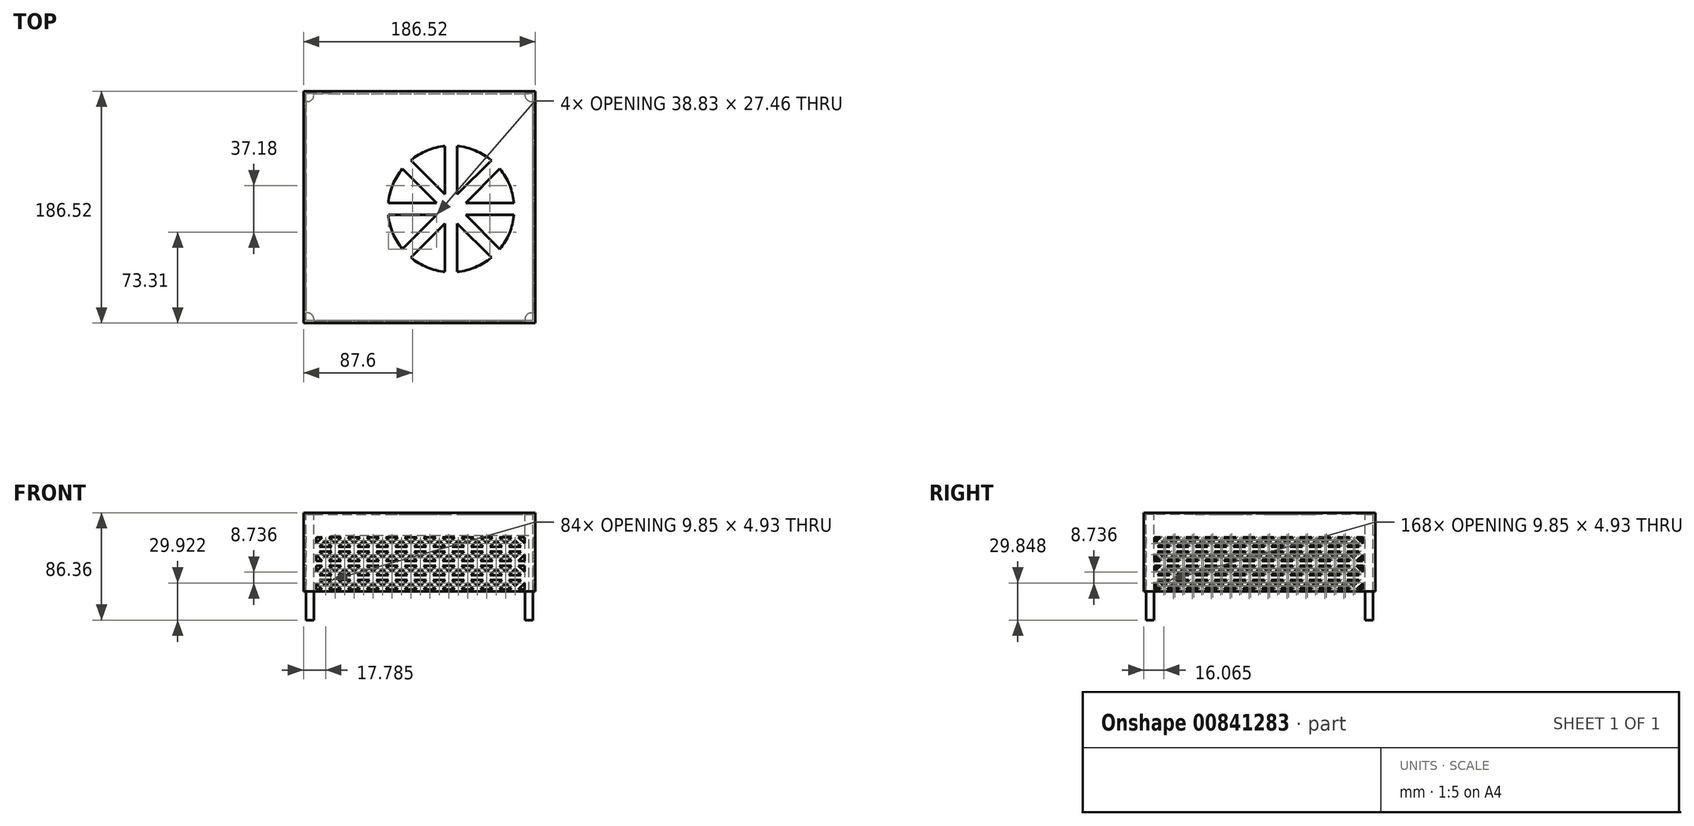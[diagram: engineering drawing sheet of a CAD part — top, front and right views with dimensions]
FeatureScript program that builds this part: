
annotation { "Feature Type Name" : "Feature", "Feature Type Description" : "" }
export const myFeature = defineFeature(function(context is Context, id is Id, definition is map)
    precondition{}
    {
        {
            var Q0;
            Q0=qCreatedBy(makeId("Top.planeOp"),FACE);
            var sketch = newSketch(context, id + "F0", { "sketchPlane" : qUnion([Q0])});
            skLineSegment(sketch, "E0.bottom", {"start": v(-6.35, 10.16) * mm, "end": v(163.65, 10.16) * mm});
            skLineSegment(sketch, "E0.top", {"start": v(-6.35, -159.84) * mm, "end": v(163.65, -159.84) * mm});
            skLineSegment(sketch, "E0.left", {"start": v(-6.35, 10.16) * mm, "end": v(-6.35, -159.84) * mm});
            skLineSegment(sketch, "E0.right", {"start": v(163.65, 10.16) * mm, "end": v(163.65, -159.84) * mm});
            skPoint(sketch, "E1", {"position": v(0, -154.94) * mm});
            skPoint(sketch, "E2", {"position": v(157.48, -22.86) * mm});
            skPoint(sketch, "E3", {"position": v(157.48, -154.94) * mm});
            skCircle(sketch, "E4", {"center": v(0, -154.94) * mm, "radius": 3.18 * mm});
            skCircle(sketch, "E5", {"center": v(0, 0) * mm, "radius": 3.18 * mm});
            skCircle(sketch, "E6", {"center": v(157.48, -22.86) * mm, "radius": 3.18 * mm});
            skCircle(sketch, "E7", {"center": v(157.48, -154.94) * mm, "radius": 3.18 * mm});
            skSolve(sketch);
        }
        {
            var Q0;
            Q0=qCreatedBy(makeId("Top.planeOp"),FACE);
            var sketch = newSketch(context, id + "F1", { "sketchPlane" : qUnion([Q0])});
            skLineSegment(sketch, "E8.0", {"start": v(-12.7, 16.51) * mm, "end": v(170, 16.51) * mm});
            skLineSegment(sketch, "E8.1", {"start": v(-12.7, 16.51) * mm, "end": v(-12.7, -166.2) * mm});
            skLineSegment(sketch, "E8.2", {"start": v(-12.7, -166.2) * mm, "end": v(170, -166.2) * mm});
            skLineSegment(sketch, "E8.3", {"start": v(170, 16.51) * mm, "end": v(170, -166.2) * mm});
            skLineSegment(sketch, "E9.0", {"start": v(-14.6, 18.42) * mm, "end": v(171.9, 18.42) * mm});
            skLineSegment(sketch, "E9.1", {"start": v(-14.6, 18.42) * mm, "end": v(-14.6, -168.1) * mm});
            skLineSegment(sketch, "E9.2", {"start": v(-14.6, -168.1) * mm, "end": v(171.9, -168.1) * mm});
            skLineSegment(sketch, "E9.3", {"start": v(171.9, 18.42) * mm, "end": v(171.9, -168.1) * mm});
            skSolve(sketch);
        }
        {
            var Q0;
            Q0=qSketchRegion(id+"F1",true);
            extrude(context, id + "F2", {"entities" : qUnion([Q0]), "depth" : 86.36 * mm, "offsetDistance" : 25.4 * mm});
        }
        {
            var Q0;
            Q0=qCreatedBy(makeId("Top.planeOp"),FACE);
            var sketch = newSketch(context, id + "F3", { "sketchPlane" : qUnion([Q0])});
            skLineSegment(sketch, "E10.bottom", {"start": v(135.08, -97.79) * mm, "end": v(135.08, 15.24) * mm, "construction": true});
            skLineSegment(sketch, "E10.top", {"start": v(79.2, -18.41) * mm, "end": v(79.2, 0) * mm, "construction": true});
            skLineSegment(sketch, "E10.left", {"start": v(135.08, 15.24) * mm, "end": v(79.2, 15.24) * mm, "construction": true});
            skLineSegment(sketch, "E10.right", {"start": v(135.08, -97.79) * mm, "end": v(79.2, -97.79) * mm, "construction": true});
            skCircle(sketch, "E11", {"center": v(131.27, 10.16) * mm, "radius": 1.27 * mm});
            skCircle(sketch, "E12", {"center": v(131.27, 10.16) * mm, "radius": 3.18 * mm});
            skLineSegment(sketch, "E13", {"start": v(79.2, 15.24) * mm, "end": v(71.07, 15.24) * mm, "construction": true});
            skLineSegment(sketch, "E14", {"start": v(71.07, 15.24) * mm, "end": v(71.07, 0) * mm, "construction": true});
            skLineSegment(sketch, "E15", {"start": v(71.07, 0) * mm, "end": v(79.2, 0) * mm, "construction": true});
            skLineSegment(sketch, "E16", {"start": v(79.2, -18.41) * mm, "end": v(71.07, -18.41) * mm, "construction": true});
            skLineSegment(sketch, "E17", {"start": v(71.07, -18.41) * mm, "end": v(71.07, -50.16) * mm, "construction": true});
            skLineSegment(sketch, "E18", {"start": v(71.07, -50.16) * mm, "end": v(79.2, -50.16) * mm, "construction": true});
            skCircle(sketch, "E19", {"center": v(83, -5.08) * mm, "radius": 3.18 * mm});
            skCircle(sketch, "E20", {"center": v(83, -5.08) * mm, "radius": 1.27 * mm});
            skLineSegment(sketch, "E21.trimOffspring", {"start": v(79.2, -97.79) * mm, "end": v(79.2, -50.16) * mm, "construction": true});
            skLineSegment(sketch, "E22.0", {"start": v(77.93, -17.14) * mm, "end": v(77.93, -1.27) * mm});
            skLineSegment(sketch, "E22.1", {"start": v(77.93, -17.14) * mm, "end": v(69.8, -17.14) * mm});
            skLineSegment(sketch, "E22.4", {"start": v(77.93, -99.06) * mm, "end": v(77.93, -52.7) * mm});
            skLineSegment(sketch, "E22.5", {"start": v(69.8, -1.27) * mm, "end": v(77.93, -1.27) * mm});
            skLineSegment(sketch, "E22.6", {"start": v(69.8, 16.51) * mm, "end": v(69.8, -1.27) * mm});
            skLineSegment(sketch, "E22.8", {"start": v(136.35, 16.51) * mm, "end": v(69.8, 16.51) * mm});
            skLineSegment(sketch, "E22.9", {"start": v(136.35, -99.06) * mm, "end": v(136.35, 16.51) * mm});
            skLineSegment(sketch, "E22.10", {"start": v(136.35, -99.06) * mm, "end": v(77.93, -99.06) * mm});
            skLineSegment(sketch, "E23.bottom", {"start": v(77.93, -99.06) * mm, "end": v(77.93, -91.44) * mm});
            skLineSegment(sketch, "E23.top", {"start": v(85.55, -99.06) * mm, "end": v(85.55, -91.44) * mm});
            skLineSegment(sketch, "E23.left", {"start": v(77.93, -99.06) * mm, "end": v(85.55, -99.06) * mm});
            skLineSegment(sketch, "E23.right", {"start": v(77.93, -91.44) * mm, "end": v(85.55, -91.44) * mm});
            skLineSegment(sketch, "E24.bottom", {"start": v(136.35, -99.06) * mm, "end": v(136.35, -91.44) * mm});
            skLineSegment(sketch, "E24.top", {"start": v(128.73, -99.06) * mm, "end": v(128.73, -91.44) * mm});
            skLineSegment(sketch, "E24.left", {"start": v(136.35, -99.06) * mm, "end": v(128.73, -99.06) * mm});
            skLineSegment(sketch, "E24.right", {"start": v(136.35, -91.44) * mm, "end": v(128.73, -91.44) * mm});
            skLineSegment(sketch, "E25.0", {"start": v(138.25, -100.96) * mm, "end": v(76.02, -100.96) * mm});
            skLineSegment(sketch, "E25.1", {"start": v(138.25, -100.96) * mm, "end": v(138.25, 18.42) * mm});
            skLineSegment(sketch, "E25.2", {"start": v(76.02, -100.96) * mm, "end": v(76.02, -57.78) * mm});
            skLineSegment(sketch, "E25.3", {"start": v(138.25, 18.42) * mm, "end": v(67.9, 18.42) * mm});
            skLineSegment(sketch, "E25.4", {"start": v(67.9, 18.42) * mm, "end": v(67.9, -3.17) * mm});
            skLineSegment(sketch, "E25.5", {"start": v(67.9, -3.17) * mm, "end": v(76.02, -3.17) * mm});
            skLineSegment(sketch, "E25.7", {"start": v(67.9, -15.24) * mm, "end": v(67.9, -24.76) * mm});
            skLineSegment(sketch, "E25.8", {"start": v(76.02, -15.24) * mm, "end": v(67.9, -15.24) * mm});
            skLineSegment(sketch, "E25.9", {"start": v(76.02, -15.24) * mm, "end": v(76.02, -3.17) * mm});
            skLineSegment(sketch, "E26", {"start": v(76.02, -57.78) * mm, "end": v(47.45, -57.78) * mm});
            skLineSegment(sketch, "E27", {"start": v(69.8, -17.14) * mm, "end": v(69.8, -27.94) * mm});
            skCircle(sketch, "E28", {"center": v(51.9, -53.34) * mm, "radius": 1.27 * mm});
            skLineSegment(sketch, "E29", {"start": v(54.43, -52.7) * mm, "end": v(54.43, -27.94) * mm});
            skLineSegment(sketch, "E30", {"start": v(54.43, -52.7) * mm, "end": v(77.93, -52.7) * mm});
            skLineSegment(sketch, "E31", {"start": v(54.43, -27.94) * mm, "end": v(69.8, -27.94) * mm});
            skCircle(sketch, "E32", {"center": v(51.9, -26.67) * mm, "radius": 1.27 * mm});
            skLineSegment(sketch, "E33", {"start": v(47.45, -57.78) * mm, "end": v(47.45, -24.76) * mm});
            skLineSegment(sketch, "E34", {"start": v(47.45, -24.76) * mm, "end": v(67.9, -24.76) * mm});
            skLineSegment(sketch, "E35", {"start": v(54.43, -52.7) * mm, "end": v(54.43, -57.78) * mm});
            skLineSegment(sketch, "E36", {"start": v(54.43, -27.94) * mm, "end": v(54.43, -24.76) * mm});
            skLineSegment(sketch, "E37", {"start": v(136.35, 16.51) * mm, "end": v(138.25, 16.51) * mm});
            skLineSegment(sketch, "E38", {"start": v(69.8, 16.51) * mm, "end": v(67.9, 16.51) * mm});
            skLineSegment(sketch, "E39", {"start": v(67.9, -52.7) * mm, "end": v(67.9, -57.78) * mm});
            skLineSegment(sketch, "E40", {"start": v(67.9, -24.76) * mm, "end": v(69.8, -24.76) * mm});
            skSolve(sketch);
        }
        {
            var Q0;
            Q0=qCreatedBy(makeId("Top.planeOp"),FACE);
            var sketch = newSketch(context, id + "F4", { "sketchPlane" : qUnion([Q0])});
            skLineSegment(sketch, "E41.bottom", {"start": v(5.66, -57.78) * mm, "end": v(76.02, -57.78) * mm});
            skLineSegment(sketch, "E41.top", {"start": v(5.66, -159.84) * mm, "end": v(76.02, -159.84) * mm});
            skLineSegment(sketch, "E41.left", {"start": v(5.66, -57.78) * mm, "end": v(5.66, -159.84) * mm});
            skLineSegment(sketch, "E41.right", {"start": v(76.02, -57.78) * mm, "end": v(76.02, -159.84) * mm});
            skLineSegment(sketch, "E42.0", {"start": v(3.12, -55.24) * mm, "end": v(47.45, -55.24) * mm});
            skLineSegment(sketch, "E42.1", {"start": v(3.12, -55.24) * mm, "end": v(3.12, -105.86) * mm});
            skLineSegment(sketch, "E42.2", {"start": v(3.12, -162.38) * mm, "end": v(10.36, -162.38) * mm});
            skLineSegment(sketch, "E42.3", {"start": v(78.56, -100.96) * mm, "end": v(78.56, -105.86) * mm});
            skLineSegment(sketch, "E43", {"start": v(47.45, -55.24) * mm, "end": v(47.45, -57.78) * mm});
            skLineSegment(sketch, "E44", {"start": v(76.02, -100.96) * mm, "end": v(78.56, -100.96) * mm});
            skLineSegment(sketch, "E45", {"start": v(10.36, -162.38) * mm, "end": v(10.36, -159.84) * mm});
            skLineSegment(sketch, "E46", {"start": v(40.84, -162.38) * mm, "end": v(40.84, -159.84) * mm, "construction": true});
            skLineSegment(sketch, "E47.MirrorCS", {"start": v(71.32, -162.38) * mm, "end": v(71.32, -159.84) * mm});
            skLineSegment(sketch, "E48.trimOffspring", {"start": v(71.32, -162.38) * mm, "end": v(78.56, -162.38) * mm});
            skArc(sketch, "E49", {"start": v(81.74, -112.21) * mm, "mid": v(84.91, -109.04) * mm, "end": v(81.74, -105.86) * mm});
            skLineSegment(sketch, "E50", {"start": v(81.74, -105.86) * mm, "end": v(81.74, -112.21) * mm, "construction": true});
            skLineSegment(sketch, "E51", {"start": v(81.74, -112.21) * mm, "end": v(78.56, -112.21) * mm});
            skLineSegment(sketch, "E52", {"start": v(81.74, -105.86) * mm, "end": v(78.56, -105.86) * mm});
            skLineSegment(sketch, "E53.trimOffspring", {"start": v(78.56, -112.21) * mm, "end": v(78.56, -162.38) * mm});
            skLineSegment(sketch, "E54.MirrorCS", {"start": v(-0.05, -105.86) * mm, "end": v(3.12, -105.86) * mm});
            skLineSegment(sketch, "E55.MirrorCS", {"start": v(-0.05, -112.21) * mm, "end": v(3.12, -112.21) * mm});
            skArc(sketch, "E56.MirrorCS", {"start": v(-0.05, -112.21) * mm, "mid": v(-3.23, -109.04) * mm, "end": v(-0.05, -105.86) * mm});
            skLineSegment(sketch, "E57.trimOffspring", {"start": v(3.12, -112.21) * mm, "end": v(3.12, -162.38) * mm});
            skCircle(sketch, "E58", {"center": v(81.74, -109.04) * mm, "radius": 1.27 * mm});
            skCircle(sketch, "E59", {"center": v(-0.05, -109.04) * mm, "radius": 1.27 * mm});
            skSolve(sketch);
        }
        {
            var Q0;
            Q0=qCreatedBy(makeId("Top.planeOp"),FACE);
            var sketch = newSketch(context, id + "F5", { "sketchPlane" : qUnion([Q0])});
            skLineSegment(sketch, "E60.bottom", {"start": v(-14.6, 18.42) * mm, "end": v(171.9, 18.42) * mm});
            skLineSegment(sketch, "E60.top", {"start": v(-14.6, -168.1) * mm, "end": v(171.9, -168.1) * mm});
            skLineSegment(sketch, "E60.left", {"start": v(-14.6, 18.42) * mm, "end": v(-14.6, -168.1) * mm});
            skLineSegment(sketch, "E60.right", {"start": v(171.9, 18.42) * mm, "end": v(171.9, -168.1) * mm});
            skSolve(sketch);
        }
        {
            var Q0;
            Q0=qSketchRegion(id+"F5",true);
            extrude(context, id + "F6", {"entities" : qUnion([Q0]), "operationType" : NewBodyOperationType.ADD, "oppositeDirection" : true, "depth" : 1.27 * mm, "offsetDistance" : 25.4 * mm});
        }
        {
            var Q0;
            Q0=qCreatedBy(makeId("Top.planeOp"),FACE);
            var sketch = newSketch(context, id + "F7", { "sketchPlane" : qUnion([Q0])});
            skLineSegment(sketch, "E61.bottom", {"start": v(77.93, -91.44) * mm, "end": v(85.55, -91.44) * mm});
            skLineSegment(sketch, "E61.top", {"start": v(77.93, -99.06) * mm, "end": v(85.55, -99.06) * mm});
            skLineSegment(sketch, "E61.left", {"start": v(77.93, -91.44) * mm, "end": v(77.93, -99.06) * mm});
            skLineSegment(sketch, "E61.right", {"start": v(85.55, -91.44) * mm, "end": v(85.55, -99.06) * mm});
            skLineSegment(sketch, "E62.bottom", {"start": v(128.73, -91.44) * mm, "end": v(136.35, -91.44) * mm});
            skLineSegment(sketch, "E62.top", {"start": v(128.73, -99.06) * mm, "end": v(136.35, -99.06) * mm});
            skLineSegment(sketch, "E62.left", {"start": v(128.73, -91.44) * mm, "end": v(128.73, -99.06) * mm});
            skLineSegment(sketch, "E62.right", {"start": v(136.35, -91.44) * mm, "end": v(136.35, -99.06) * mm});
            skCircle(sketch, "E63.0", {"center": v(83, -5.08) * mm, "radius": 3.18 * mm});
            skCircle(sketch, "E63.1", {"center": v(131.27, 10.16) * mm, "radius": 3.18 * mm});
            skCircle(sketch, "E64.0", {"center": v(83, -5.08) * mm, "radius": 1.27 * mm});
            skCircle(sketch, "E64.1", {"center": v(131.27, 10.16) * mm, "radius": 1.27 * mm});
            skLineSegment(sketch, "E65.bottom", {"start": v(47.45, -24.76) * mm, "end": v(54.43, -24.76) * mm});
            skLineSegment(sketch, "E65.top", {"start": v(47.45, -57.78) * mm, "end": v(54.43, -57.78) * mm});
            skLineSegment(sketch, "E65.left", {"start": v(47.45, -24.76) * mm, "end": v(47.45, -57.78) * mm});
            skLineSegment(sketch, "E65.right", {"start": v(54.43, -24.76) * mm, "end": v(54.43, -57.78) * mm});
            skCircle(sketch, "E66.1", {"center": v(51.9, -26.67) * mm, "radius": 1.27 * mm});
            skCircle(sketch, "E66.2", {"center": v(51.9, -53.34) * mm, "radius": 1.27 * mm});
            skSolve(sketch);
        }
        {
            var Q0;
            Q0=qSketchRegion(id+"F7",true);
            extrude(context, id + "F8", {"entities" : qUnion([Q0]), "operationType" : NewBodyOperationType.ADD, "depth" : 3.8 * mm, "offsetDistance" : 25.4 * mm});
        }
        {
            var Q0;
            Q0=qCreatedBy(makeId("Top.planeOp"),FACE);
            var sketch = newSketch(context, id + "F9", { "sketchPlane" : qUnion([Q0])});
            skLineSegment(sketch, "E67.0", {"start": v(67.9, -15.24) * mm, "end": v(67.9, -24.76) * mm});
            skLineSegment(sketch, "E67.1", {"start": v(67.9, -24.76) * mm, "end": v(69.8, -24.76) * mm});
            skLineSegment(sketch, "E67.2", {"start": v(69.8, -17.14) * mm, "end": v(69.8, -24.76) * mm});
            skLineSegment(sketch, "E67.3", {"start": v(76.02, -15.24) * mm, "end": v(67.9, -15.24) * mm});
            skLineSegment(sketch, "E67.4", {"start": v(77.93, -17.14) * mm, "end": v(69.8, -17.14) * mm});
            skLineSegment(sketch, "E67.5", {"start": v(77.93, -17.14) * mm, "end": v(77.93, -1.27) * mm});
            skLineSegment(sketch, "E67.6", {"start": v(76.02, -15.24) * mm, "end": v(76.02, -3.17) * mm});
            skLineSegment(sketch, "E67.7", {"start": v(69.8, -1.27) * mm, "end": v(77.93, -1.27) * mm});
            skLineSegment(sketch, "E67.8", {"start": v(67.9, -3.17) * mm, "end": v(76.02, -3.17) * mm});
            skLineSegment(sketch, "E67.9", {"start": v(67.9, 16.51) * mm, "end": v(67.9, -3.17) * mm});
            skLineSegment(sketch, "E67.10", {"start": v(69.8, 16.51) * mm, "end": v(69.8, -1.27) * mm});
            skLineSegment(sketch, "E67.13", {"start": v(136.35, -99.06) * mm, "end": v(136.35, 16.51) * mm});
            skLineSegment(sketch, "E67.14", {"start": v(138.25, -100.96) * mm, "end": v(138.25, 16.51) * mm});
            skLineSegment(sketch, "E67.15", {"start": v(136.35, -99.06) * mm, "end": v(77.93, -99.06) * mm});
            skLineSegment(sketch, "E67.16", {"start": v(138.25, -100.96) * mm, "end": v(78.56, -100.96) * mm});
            skLineSegment(sketch, "E67.17", {"start": v(78.56, -100.96) * mm, "end": v(78.56, -105.86) * mm});
            skLineSegment(sketch, "E67.18", {"start": v(81.74, -105.86) * mm, "end": v(78.56, -105.86) * mm});
            skArc(sketch, "E67.19", {"start": v(81.74, -112.21) * mm, "mid": v(84.91, -109.04) * mm, "end": v(81.74, -105.86) * mm});
            skLineSegment(sketch, "E67.20.1", {"start": v(76.02, -100.96) * mm, "end": v(76.02, -159.84) * mm});
            skLineSegment(sketch, "E67.20.2", {"start": v(76.02, -159.84) * mm, "end": v(71.32, -159.84) * mm});
            skLineSegment(sketch, "E67.20.3", {"start": v(71.32, -159.84) * mm, "end": v(71.32, -162.38) * mm});
            skLineSegment(sketch, "E67.20.4", {"start": v(71.32, -162.38) * mm, "end": v(78.56, -162.38) * mm});
            skLineSegment(sketch, "E67.20.5", {"start": v(78.56, -162.38) * mm, "end": v(78.56, -112.21) * mm});
            skLineSegment(sketch, "E67.20.6", {"start": v(78.56, -112.21) * mm, "end": v(81.74, -112.21) * mm});
            skArc(sketch, "E67.20.7", {"start": v(81.74, -112.21) * mm, "mid": v(84.91, -109.04) * mm, "end": v(81.74, -105.86) * mm});
            skLineSegment(sketch, "E67.20.8", {"start": v(81.74, -105.86) * mm, "end": v(78.56, -105.86) * mm});
            skLineSegment(sketch, "E67.20.9", {"start": v(78.56, -105.86) * mm, "end": v(78.56, -100.96) * mm});
            skLineSegment(sketch, "E67.21.0", {"start": v(47.45, -57.78) * mm, "end": v(47.45, -55.24) * mm});
            skLineSegment(sketch, "E67.21.1", {"start": v(47.45, -55.24) * mm, "end": v(3.12, -55.24) * mm});
            skLineSegment(sketch, "E67.21.2", {"start": v(3.12, -55.24) * mm, "end": v(3.12, -105.86) * mm});
            skLineSegment(sketch, "E67.21.3", {"start": v(3.12, -105.86) * mm, "end": v(-0.05, -105.86) * mm});
            skArc(sketch, "E67.21.4", {"start": v(-0.05, -105.86) * mm, "mid": v(-3.23, -109.04) * mm, "end": v(-0.05, -112.21) * mm});
            skLineSegment(sketch, "E67.21.5", {"start": v(-0.05, -112.21) * mm, "end": v(3.12, -112.21) * mm});
            skLineSegment(sketch, "E67.21.6", {"start": v(3.12, -112.21) * mm, "end": v(3.12, -162.38) * mm});
            skLineSegment(sketch, "E67.21.7", {"start": v(3.12, -162.38) * mm, "end": v(10.36, -162.38) * mm});
            skLineSegment(sketch, "E67.21.8", {"start": v(10.36, -162.38) * mm, "end": v(10.36, -159.84) * mm});
            skLineSegment(sketch, "E67.21.9", {"start": v(10.36, -159.84) * mm, "end": v(5.66, -159.84) * mm});
            skLineSegment(sketch, "E67.21.10", {"start": v(5.66, -159.84) * mm, "end": v(5.66, -57.78) * mm});
            skLineSegment(sketch, "E67.21.11", {"start": v(5.66, -57.78) * mm, "end": v(47.45, -57.78) * mm});
            skLineSegment(sketch, "E67.22", {"start": v(76.02, -100.96) * mm, "end": v(76.02, -57.78) * mm});
            skLineSegment(sketch, "E67.23", {"start": v(77.93, -99.06) * mm, "end": v(77.93, -52.7) * mm});
            skLineSegment(sketch, "E67.24", {"start": v(67.9, -52.7) * mm, "end": v(77.93, -52.7) * mm});
            skLineSegment(sketch, "E67.25", {"start": v(67.9, -52.7) * mm, "end": v(67.9, -57.78) * mm});
            skLineSegment(sketch, "E67.26", {"start": v(76.02, -57.78) * mm, "end": v(67.9, -57.78) * mm});
            skPoint(sketch, "E68.orphan", {"position": v(69.8, -27.94) * mm});
            skPoint(sketch, "E69.orphan", {"position": v(54.43, -52.7) * mm});
            skPoint(sketch, "E70.orphan", {"position": v(47.45, -57.78) * mm});
            skPoint(sketch, "E71.orphan", {"position": v(76.02, -100.96) * mm});
            skLineSegment(sketch, "E72.0", {"start": v(67.9, 16.51) * mm, "end": v(69.8, 16.51) * mm});
            skPoint(sketch, "E73.orphan", {"position": v(-12.7, 16.51) * mm});
            skPoint(sketch, "E74.orphan", {"position": v(170, 16.51) * mm});
            skPoint(sketch, "E75.orphan", {"position": v(138.25, 18.42) * mm});
            skPoint(sketch, "E76.orphan", {"position": v(67.9, 18.42) * mm});
            skLineSegment(sketch, "E77.trimOffspring", {"start": v(136.35, 16.51) * mm, "end": v(138.25, 16.51) * mm});
            skCircle(sketch, "E78.0", {"center": v(-0.05, -109.04) * mm, "radius": 1.27 * mm});
            skCircle(sketch, "E78.1", {"center": v(81.74, -109.04) * mm, "radius": 1.27 * mm});
            skSolve(sketch);
        }
        {
            var Q0;
            Q0=qSketchRegion(id+"F9",true);
            extrude(context, id + "F10", {"entities" : qUnion([Q0]), "operationType" : NewBodyOperationType.ADD, "depth" : 6.35 * mm, "offsetDistance" : 25.4 * mm});
        }
        {
            var Q0;
            Q0=makeQuery(id+"F6.boolean.opBoolean","MERGE",FACE,{"derivedFrom":[makeQuery(id+"F2.opExtrude","SWEPT_FACE",FACE,{"disambiguationData":[OSD([sQuery(id+"F1.wireOp",EDGE,"E9.0")])]}),makeQuery(id+"F6.opExtrude","SWEPT_FACE",FACE,{"disambiguationData":[OSD([sQuery(id+"F5.wireOp",EDGE,"E60.bottom")])]})]});
            var sketch = newSketch(context, id + "F11", { "sketchPlane" : qUnion([Q0])});
            skCircle(sketch, "E79", {"center": v(-119.2, 12.32) * mm, "radius": 5.08 * mm});
            skCircle(sketch, "E80", {"center": v(-102.56, 11.43) * mm, "radius": 5.4 * mm});
            skCircle(sketch, "E81", {"center": v(-88.09, 12.32) * mm, "radius": 3.18 * mm});
            skCircle(sketch, "E82", {"center": v(-75.9, 10.41) * mm, "radius": 3.81 * mm});
            skLineSegment(sketch, "E83", {"start": v(-54.43, 3.81) * mm, "end": v(-135.08, 3.81) * mm, "construction": true});
            skLineSegment(sketch, "E84", {"start": v(-135.08, 3.81) * mm, "end": v(-135.08, 0) * mm, "construction": true});
            skSolve(sketch);
        }
        {
            var Q0;
            Q0=qSketchRegion(id+"F11",true);
            extrude(context, id + "F12", {"entities" : qUnion([Q0]), "operationType" : NewBodyOperationType.REMOVE, "endBound" : BoundingType.UP_TO_NEXT, "oppositeDirection" : true, "depth" : 25.4 * mm, "offsetDistance" : 25.4 * mm});
        }
        {
            var Q0;
            Q0=makeQuery(id+"F2.opExtrude","SWEPT_FACE",FACE,{"disambiguationData":[OSD([sQuery(id+"F1.wireOp",EDGE,"E8.2")])]});
            var sketch = newSketch(context, id + "F13", { "sketchPlane" : qUnion([Q0])});
            skLineSegment(sketch, "E85.0", {"start": v(-10.36, 6.35) * mm, "end": v(-10.36, 0) * mm});
            skLineSegment(sketch, "E85.1", {"start": v(-71.32, 6.35) * mm, "end": v(-71.32, 0) * mm});
            skLineSegment(sketch, "E86", {"start": v(-10.36, 6.35) * mm, "end": v(-71.32, 6.35) * mm, "construction": true});
            skLineSegment(sketch, "E87", {"start": v(-10.36, 0) * mm, "end": v(-71.32, 0) * mm});
            skLineSegment(sketch, "E88", {"start": v(-10.36, 6.35) * mm, "end": v(-10.36, 19.05) * mm});
            skLineSegment(sketch, "E89", {"start": v(-10.36, 19.05) * mm, "end": v(-71.32, 19.05) * mm});
            skLineSegment(sketch, "E90", {"start": v(-71.32, 19.05) * mm, "end": v(-71.32, 6.35) * mm});
            skLineSegment(sketch, "E91", {"start": v(-16.71, 19.05) * mm, "end": v(-16.71, 0) * mm});
            skLineSegment(sketch, "E92", {"start": v(-17.47, 19.05) * mm, "end": v(-17.47, 0) * mm});
            skLineSegment(sketch, "E93.1.0.0", {"start": v(-28.14, 19.05) * mm, "end": v(-28.14, 0) * mm});
            skLineSegment(sketch, "E93.1.0.1", {"start": v(-28.9, 19.05) * mm, "end": v(-28.9, 0) * mm});
            skLineSegment(sketch, "E93.2.0.0", {"start": v(-39.57, 19.05) * mm, "end": v(-39.57, 0) * mm});
            skLineSegment(sketch, "E93.2.0.1", {"start": v(-40.33, 19.05) * mm, "end": v(-40.33, 0) * mm});
            skLineSegment(sketch, "E93.3.0.0", {"start": v(-51, 19.05) * mm, "end": v(-51, 0) * mm});
            skLineSegment(sketch, "E93.3.0.1", {"start": v(-51.76, 19.05) * mm, "end": v(-51.76, 0) * mm});
            skLineSegment(sketch, "E93.4.0.0", {"start": v(-62.43, 19.05) * mm, "end": v(-62.43, 0) * mm});
            skLineSegment(sketch, "E93.4.0.1", {"start": v(-63.2, 19.05) * mm, "end": v(-63.2, 0) * mm});
            skLineSegment(sketch, "E93.direction1", {"start": v(-17.47, 0) * mm, "end": v(-28.9, 0) * mm, "construction": true});
            skSolve(sketch);
        }
        {
            var Q0;
            {var subQ4=sQuery(id+"F13.wireOp",EDGE,"E85.0");Q0=makeQuery(id+"F13.imprint","IMPRINT",FACE,{"disambiguationData":[TD([[makeQuery(id+"F13.imprint","IMPRINT",EDGE,{"derivedFrom":subQ4}),-1.0]])]});}
            var Q1;
            {var subQ0=sQuery(id+"F13.wireOp",EDGE,"E92");Q1=makeQuery(id+"F13.imprint","IMPRINT",FACE,{"disambiguationData":[TD([[makeQuery(id+"F13.imprint","IMPRINT",EDGE,{"derivedFrom":subQ0}),-1.0]])]});}
            var Q2;
            {var subQ0=sQuery(id+"F13.wireOp",EDGE,"E93.1.0.1");Q2=makeQuery(id+"F13.imprint","IMPRINT",FACE,{"disambiguationData":[TD([[makeQuery(id+"F13.imprint","IMPRINT",EDGE,{"derivedFrom":subQ0}),-1.0]])]});}
            var Q3;
            {var subQ0=sQuery(id+"F13.wireOp",EDGE,"E93.2.0.1");Q3=makeQuery(id+"F13.imprint","IMPRINT",FACE,{"disambiguationData":[TD([[makeQuery(id+"F13.imprint","IMPRINT",EDGE,{"derivedFrom":subQ0}),-1.0]])]});}
            var Q4;
            {var subQ0=sQuery(id+"F13.wireOp",EDGE,"E93.3.0.1");Q4=makeQuery(id+"F13.imprint","IMPRINT",FACE,{"disambiguationData":[TD([[makeQuery(id+"F13.imprint","IMPRINT",EDGE,{"derivedFrom":subQ0}),-1.0]])]});}
            var Q5;
            {var subQ4=sQuery(id+"F13.wireOp",EDGE,"E85.1");Q5=makeQuery(id+"F13.imprint","IMPRINT",FACE,{"disambiguationData":[TD([[makeQuery(id+"F13.imprint","IMPRINT",EDGE,{"derivedFrom":subQ4}),1.0]])]});}
            extrude(context, id + "F14", {"entities" : qUnion([Q0, Q1, Q2, Q3, Q4, Q5]), "operationType" : NewBodyOperationType.REMOVE, "oppositeDirection" : true, "depth" : 2.54 * mm, "offsetDistance" : 25.4 * mm});
        }
        {
            var Q0;
            Q0=makeQuery(id+"F6.boolean.opBoolean","MERGE",FACE,{"derivedFrom":[makeQuery(id+"F2.opExtrude","SWEPT_FACE",FACE,{"disambiguationData":[OSD([sQuery(id+"F1.wireOp",EDGE,"E9.3")])]}),makeQuery(id+"F6.opExtrude","SWEPT_FACE",FACE,{"disambiguationData":[OSD([sQuery(id+"F5.wireOp",EDGE,"E60.right")])]})]});
            var sketch = newSketch(context, id + "F15", { "sketchPlane" : qUnion([Q0])});
            skLineSegment(sketch, "E94.bottom", {"start": v(-149.86, 8.9) * mm, "end": v(-25.4, 8.9) * mm, "construction": true});
            skLineSegment(sketch, "E94.top", {"start": v(-149.86, 21.59) * mm, "end": v(-25.4, 21.59) * mm, "construction": true});
            skLineSegment(sketch, "E94.left", {"start": v(-149.86, 8.9) * mm, "end": v(-149.86, 21.6) * mm, "construction": true});
            skLineSegment(sketch, "E94.right", {"start": v(-25.4, 8.9) * mm, "end": v(-25.4, 21.59) * mm, "construction": true});
            skLineSegment(sketch, "E95", {"start": v(-111.76, 21.6) * mm, "end": v(-111.76, 8.9) * mm, "construction": true});
            skLineSegment(sketch, "E96.bottom", {"start": v(-117.47, 19.37) * mm, "end": v(-133.98, 19.37) * mm});
            skLineSegment(sketch, "E96.top", {"start": v(-117.47, 11.11) * mm, "end": v(-133.98, 11.11) * mm});
            skLineSegment(sketch, "E96.left", {"start": v(-117.47, 19.37) * mm, "end": v(-117.47, 11.11) * mm});
            skLineSegment(sketch, "E96.right", {"start": v(-133.98, 19.37) * mm, "end": v(-133.98, 11.11) * mm});
            skPoint(sketch, "E96.middle", {"position": v(-125.73, 15.24) * mm});
            skPoint(sketch, "E97", {"position": v(-111.76, 15.24) * mm});
            skCircle(sketch, "E98", {"center": v(-141.6, 15.24) * mm, "radius": 1.9 * mm});
            skPoint(sketch, "E98.centerSnap0", {"position": v(-133.98, 15.24) * mm});
            skLineSegment(sketch, "E99.MirrorCS", {"start": v(-106.04, 19.37) * mm, "end": v(-106.04, 11.11) * mm});
            skLineSegment(sketch, "E100.MirrorCS", {"start": v(-106.04, 19.37) * mm, "end": v(-89.53, 19.37) * mm});
            skLineSegment(sketch, "E101.MirrorCS", {"start": v(-89.53, 19.37) * mm, "end": v(-89.53, 11.11) * mm});
            skPoint(sketch, "E102.MirrorP", {"position": v(-89.53, 15.24) * mm});
            skCircle(sketch, "E103.MirrorC", {"center": v(-81.91, 15.24) * mm, "radius": 1.9 * mm});
            skPoint(sketch, "E104.MirrorP", {"position": v(-97.79, 15.24) * mm});
            skLineSegment(sketch, "E105.MirrorCS", {"start": v(-106.04, 11.11) * mm, "end": v(-89.53, 11.11) * mm});
            skLineSegment(sketch, "E106", {"start": v(-54.6, 21.6) * mm, "end": v(-54.6, 8.9) * mm, "construction": true});
            skLineSegment(sketch, "E107.bottom", {"start": v(-46.35, 19.37) * mm, "end": v(-62.86, 19.37) * mm});
            skLineSegment(sketch, "E107.top", {"start": v(-46.35, 11.11) * mm, "end": v(-62.86, 11.11) * mm});
            skLineSegment(sketch, "E107.left", {"start": v(-46.35, 19.37) * mm, "end": v(-46.35, 11.11) * mm});
            skLineSegment(sketch, "E107.right", {"start": v(-62.86, 19.37) * mm, "end": v(-62.86, 11.11) * mm});
            skPoint(sketch, "E107.middle", {"position": v(-54.6, 15.24) * mm});
            skCircle(sketch, "E108", {"center": v(-69.22, 15.24) * mm, "radius": 1.9 * mm});
            skCircle(sketch, "E109.MirrorC", {"center": v(-40, 15.24) * mm, "radius": 1.9 * mm});
            skLineSegment(sketch, "E110", {"start": v(-75.56, 21.59) * mm, "end": v(-75.56, 8.9) * mm, "construction": true});
            skSolve(sketch);
        }
        {
            var Q0;
            Q0=qSketchRegion(id+"F15",true);
            extrude(context, id + "F16", {"entities" : qUnion([Q0]), "operationType" : NewBodyOperationType.REMOVE, "endBound" : BoundingType.UP_TO_NEXT, "oppositeDirection" : true, "depth" : 25.4 * mm, "offsetDistance" : 25.4 * mm});
        }
        {
            var Q0;
            Q0=sQuery(id+"F15.wireOp",EDGE,"E110");
            cPoint(context, id + "F17", {"entities" : qUnion([Q0]), "parameter" : 0.5});
        }
        {
            var Q0;
            Q0=qCreatedBy(makeId("Front.planeOp"),FACE);
            var Q1;
            Q1=qCreatedBy(id+"F17",VERTEX);
            cPlane(context, id + "F18", {"entities" : qUnion([Q0, Q1]), "cplaneType" : CPlaneType.PLANE_POINT, "offset" : 25.4 * mm, "width" : 152.4 * mm, "height" : 152.4 * mm});
        }
        {
            var Q0;
            Q0=qCreatedBy(id+"F18.planeOp",FACE);
            var sketch = newSketch(context, id + "F19", { "sketchPlane" : qUnion([Q0])});
            skLineSegment(sketch, "E111", {"start": v(170, 21.6) * mm, "end": v(157.3, 0) * mm});
            skLineSegment(sketch, "E112", {"start": v(157.3, 0) * mm, "end": v(170, 0) * mm});
            skLineSegment(sketch, "E113", {"start": v(170, 0) * mm, "end": v(170, 21.59) * mm});
            skSolve(sketch);
        }
        {
            var Q0;
            Q0=qSketchRegion(id+"F19",true);
            extrude(context, id + "F20", {"entities" : qUnion([Q0]), "operationType" : NewBodyOperationType.ADD, "endBound" : BoundingType.SYMMETRIC, "depth" : 1.9 * mm, "offsetDistance" : 25.4 * mm});
        }
        {
            var Q0;
            Q0=qCreatedBy(makeId("Top.planeOp"),FACE);
            var sketch = newSketch(context, id + "F21", { "sketchPlane" : qUnion([Q0])});
            skCircle(sketch, "E114.0", {"center": v(0, 0) * mm, "radius": 3.18 * mm});
            skCircle(sketch, "E114.1", {"center": v(157.48, -22.86) * mm, "radius": 3.18 * mm});
            skCircle(sketch, "E114.2", {"center": v(157.48, -154.94) * mm, "radius": 3.18 * mm});
            skCircle(sketch, "E114.3", {"center": v(0, -154.94) * mm, "radius": 3.18 * mm});
            skCircle(sketch, "E115", {"center": v(0, 0) * mm, "radius": 1.27 * mm});
            skCircle(sketch, "E116", {"center": v(157.48, -22.86) * mm, "radius": 1.27 * mm});
            skCircle(sketch, "E117", {"center": v(157.48, -154.94) * mm, "radius": 1.27 * mm});
            skCircle(sketch, "E118", {"center": v(0, -154.94) * mm, "radius": 1.27 * mm});
            skLineSegment(sketch, "E119", {"start": v(160.39, -153.67) * mm, "end": v(170, -153.67) * mm});
            skLineSegment(sketch, "E120.0", {"start": v(170, -21.59) * mm, "end": v(170, -24.13) * mm});
            skLineSegment(sketch, "E120.1", {"start": v(-1.27, -166.2) * mm, "end": v(1.27, -166.2) * mm});
            skLineSegment(sketch, "E120.2", {"start": v(-1.27, 16.51) * mm, "end": v(1.27, 16.51) * mm});
            skLineSegment(sketch, "E120.3", {"start": v(-12.7, 1.27) * mm, "end": v(-12.7, -1.27) * mm});
            skLineSegment(sketch, "E121", {"start": v(156.21, -157.85) * mm, "end": v(156.21, -166.2) * mm});
            skLineSegment(sketch, "E122", {"start": v(158.75, -157.85) * mm, "end": v(158.75, -166.2) * mm});
            skPoint(sketch, "E123.orphan", {"position": v(157.48, -153.67) * mm});
            skLineSegment(sketch, "E124.trimOffspring", {"start": v(160.39, -156.2) * mm, "end": v(170, -156.2) * mm});
            skPoint(sketch, "E125.start.orphan", {"position": v(157.48, -156.2) * mm});
            skPoint(sketch, "E126.orphan", {"position": v(158.75, -154.94) * mm});
            skPoint(sketch, "E127.orphan", {"position": v(156.21, -154.94) * mm});
            skLineSegment(sketch, "E128", {"start": v(-2.9, -153.67) * mm, "end": v(-12.7, -153.67) * mm});
            skLineSegment(sketch, "E129", {"start": v(1.27, -157.85) * mm, "end": v(1.27, -166.2) * mm});
            skPoint(sketch, "E130.orphan", {"position": v(0, -153.67) * mm});
            skLineSegment(sketch, "E131.trimOffspring", {"start": v(-2.9, -156.2) * mm, "end": v(-12.7, -156.2) * mm});
            skLineSegment(sketch, "E132.trimOffspring", {"start": v(-1.27, -157.85) * mm, "end": v(-1.27, -166.2) * mm});
            skPoint(sketch, "E133.start.orphan", {"position": v(0, -156.2) * mm});
            skPoint(sketch, "E134.start.orphan", {"position": v(-1.27, -154.94) * mm});
            skPoint(sketch, "E135.orphan", {"position": v(1.27, -154.94) * mm});
            skLineSegment(sketch, "E136", {"start": v(1.27, 2.9) * mm, "end": v(1.27, 16.51) * mm});
            skLineSegment(sketch, "E137", {"start": v(-1.27, 2.9) * mm, "end": v(-1.27, 16.51) * mm});
            skLineSegment(sketch, "E138", {"start": v(-2.9, -1.27) * mm, "end": v(-12.7, -1.27) * mm});
            skLineSegment(sketch, "E139", {"start": v(-2.9, 1.27) * mm, "end": v(-12.7, 1.27) * mm});
            skPoint(sketch, "E140.orphan", {"position": v(0, 1.27) * mm});
            skPoint(sketch, "E141.orphan", {"position": v(-1.27, 0) * mm});
            skPoint(sketch, "E142.orphan", {"position": v(1.27, 0) * mm});
            skPoint(sketch, "E143.orphan", {"position": v(0, -1.27) * mm});
            skLineSegment(sketch, "E144", {"start": v(160.39, -21.59) * mm, "end": v(170, -21.59) * mm});
            skLineSegment(sketch, "E145", {"start": v(160.39, -24.13) * mm, "end": v(170, -24.13) * mm});
            skPoint(sketch, "E146.orphan", {"position": v(157.48, -21.59) * mm});
            skPoint(sketch, "E147.orphan", {"position": v(157.48, -24.13) * mm});
            skPoint(sketch, "E148.orphan", {"position": v(-12.7, 16.51) * mm});
            skLineSegment(sketch, "E149.trimOffspring", {"start": v(-12.7, -153.67) * mm, "end": v(-12.7, -156.2) * mm});
            skPoint(sketch, "E150.orphan", {"position": v(-12.7, -166.2) * mm});
            skLineSegment(sketch, "E151.trimOffspring", {"start": v(156.21, -166.2) * mm, "end": v(158.75, -166.2) * mm});
            skPoint(sketch, "E152.orphan", {"position": v(170, -166.2) * mm});
            skLineSegment(sketch, "E153.trimOffspring", {"start": v(170, -153.67) * mm, "end": v(170, -156.2) * mm});
            skPoint(sketch, "E154.orphan", {"position": v(170, 16.51) * mm});
            skSolve(sketch);
        }
        {
            var Q0;
            Q0=makeQuery(id+"F21.imprint","IMPRINT",FACE,{"disambiguationData":[TD([[makeQuery(id+"F21.imprint","IMPRINT",EDGE,{"derivedFrom":sQuery(id+"F21.wireOp",EDGE,"E120.2")}),-1.0]])]});
            var Q1;
            Q1=makeQuery(id+"F21.imprint","IMPRINT",FACE,{"disambiguationData":[TD([[makeQuery(id+"F21.imprint","IMPRINT",EDGE,{"derivedFrom":sQuery(id+"F21.wireOp",EDGE,"E120.3")}),1.0]])]});
            var Q2;
            Q2=makeQuery(id+"F21.imprint","IMPRINT",FACE,{"disambiguationData":[TD([[makeQuery(id+"F21.imprint","IMPRINT",EDGE,{"derivedFrom":sQuery(id+"F21.wireOp",EDGE,"E115")}),1.0]])]});
            var Q3;
            Q3=makeQuery(id+"F21.imprint","IMPRINT",FACE,{"disambiguationData":[TD([[makeQuery(id+"F21.imprint","IMPRINT",EDGE,{"derivedFrom":sQuery(id+"F21.wireOp",EDGE,"E116")}),1.0]])]});
            var Q4;
            Q4=makeQuery(id+"F21.imprint","IMPRINT",FACE,{"disambiguationData":[TD([[makeQuery(id+"F21.imprint","IMPRINT",EDGE,{"derivedFrom":sQuery(id+"F21.wireOp",EDGE,"E120.0")}),-1.0]])]});
            var Q5;
            Q5=makeQuery(id+"F21.imprint","IMPRINT",FACE,{"disambiguationData":[TD([[makeQuery(id+"F21.imprint","IMPRINT",EDGE,{"derivedFrom":sQuery(id+"F21.wireOp",EDGE,"E117")}),1.0]])]});
            var Q6;
            {var subQ0=sQuery(id+"F21.wireOp",EDGE,"E119");Q6=makeQuery(id+"F21.imprint","IMPRINT",FACE,{"disambiguationData":[TD([[makeQuery(id+"F21.imprint","IMPRINT",EDGE,{"derivedFrom":subQ0}),-1.0]])]});}
            var Q7;
            {var subQ0=sQuery(id+"F21.wireOp",EDGE,"E121");Q7=makeQuery(id+"F21.imprint","IMPRINT",FACE,{"disambiguationData":[TD([[makeQuery(id+"F21.imprint","IMPRINT",EDGE,{"derivedFrom":subQ0}),1.0]])]});}
            var Q8;
            {var subQ0=sQuery(id+"F21.wireOp",EDGE,"E128");Q8=makeQuery(id+"F21.imprint","IMPRINT",FACE,{"disambiguationData":[TD([[makeQuery(id+"F21.imprint","IMPRINT",EDGE,{"derivedFrom":subQ0}),1.0]])]});}
            var Q9;
            Q9=makeQuery(id+"F21.imprint","IMPRINT",FACE,{"disambiguationData":[TD([[makeQuery(id+"F21.imprint","IMPRINT",EDGE,{"derivedFrom":sQuery(id+"F21.wireOp",EDGE,"E118")}),1.0]])]});
            var Q10;
            Q10=makeQuery(id+"F21.imprint","IMPRINT",FACE,{"disambiguationData":[TD([[makeQuery(id+"F21.imprint","IMPRINT",EDGE,{"derivedFrom":sQuery(id+"F21.wireOp",EDGE,"E120.1")}),1.0]])]});
            extrude(context, id + "F22", {"entities" : qUnion([Q0, Q1, Q2, Q3, Q4, Q5, Q6, Q7, Q8, Q9, Q10]), "operationType" : NewBodyOperationType.ADD, "depth" : 12.7 * mm, "offsetDistance" : 25.4 * mm});
        }
        {
            var Q0;
            Q0=makeQuery(id+"F21.imprint","IMPRINT",FACE,{"disambiguationData":[TD([[makeQuery(id+"F21.imprint","IMPRINT",EDGE,{"derivedFrom":sQuery(id+"F21.wireOp",EDGE,"E115")}),-1.0]])]});
            var Q1;
            Q1=makeQuery(id+"F21.imprint","IMPRINT",FACE,{"disambiguationData":[TD([[makeQuery(id+"F21.imprint","IMPRINT",EDGE,{"derivedFrom":sQuery(id+"F21.wireOp",EDGE,"E116")}),-1.0]])]});
            var Q2;
            Q2=makeQuery(id+"F21.imprint","IMPRINT",FACE,{"disambiguationData":[TD([[makeQuery(id+"F21.imprint","IMPRINT",EDGE,{"derivedFrom":sQuery(id+"F21.wireOp",EDGE,"E118")}),-1.0]])]});
            var Q3;
            Q3=makeQuery(id+"F21.imprint","IMPRINT",FACE,{"disambiguationData":[TD([[makeQuery(id+"F21.imprint","IMPRINT",EDGE,{"derivedFrom":sQuery(id+"F21.wireOp",EDGE,"E117")}),-1.0]])]});
            extrude(context, id + "F23", {"entities" : qUnion([Q0, Q1, Q2, Q3]), "operationType" : NewBodyOperationType.ADD, "depth" : 25.4 * mm, "offsetDistance" : 25.4 * mm});
        }
        {
            var Q0;
            Q0=qCreatedBy(makeId("Front.planeOp"),FACE);
            var sketch = newSketch(context, id + "F24", { "sketchPlane" : qUnion([Q0])});
            skLineSegment(sketch, "E155.bottom", {"start": v(166.9, 68.25) * mm, "end": v(7.52, 68.25) * mm});
            skLineSegment(sketch, "E155.top", {"start": v(166.9, 23.16) * mm, "end": v(7.52, 23.16) * mm});
            skLineSegment(sketch, "E155.left", {"start": v(166.9, 68.25) * mm, "end": v(166.9, 23.16) * mm});
            skLineSegment(sketch, "E155.right", {"start": v(7.52, 68.25) * mm, "end": v(7.52, 23.16) * mm});
            skLineSegment(sketch, "E156", {"start": v(156.74, 68.25) * mm, "end": v(156.74, 23.16) * mm});
            skLineSegment(sketch, "E157", {"start": v(155.98, 68.25) * mm, "end": v(155.98, 23.16) * mm});
            skLineSegment(sketch, "E158.1.0.0", {"start": v(144.04, 68.25) * mm, "end": v(144.04, 23.16) * mm});
            skLineSegment(sketch, "E158.1.0.1", {"start": v(143.28, 68.25) * mm, "end": v(143.28, 23.16) * mm});
            skLineSegment(sketch, "E158.2.0.0", {"start": v(131.34, 68.25) * mm, "end": v(131.34, 23.16) * mm});
            skLineSegment(sketch, "E158.2.0.1", {"start": v(130.58, 68.25) * mm, "end": v(130.58, 23.16) * mm});
            skLineSegment(sketch, "E158.3.0.0", {"start": v(118.64, 68.25) * mm, "end": v(118.64, 23.16) * mm});
            skLineSegment(sketch, "E158.3.0.1", {"start": v(117.88, 68.25) * mm, "end": v(117.88, 23.16) * mm});
            skLineSegment(sketch, "E158.4.0.0", {"start": v(105.94, 68.25) * mm, "end": v(105.94, 23.16) * mm});
            skLineSegment(sketch, "E158.4.0.1", {"start": v(105.18, 68.25) * mm, "end": v(105.18, 23.16) * mm});
            skLineSegment(sketch, "E158.5.0.0", {"start": v(93.24, 68.25) * mm, "end": v(93.24, 23.16) * mm});
            skLineSegment(sketch, "E158.5.0.1", {"start": v(92.48, 68.25) * mm, "end": v(92.48, 23.16) * mm});
            skLineSegment(sketch, "E158.6.0.0", {"start": v(80.54, 68.25) * mm, "end": v(80.54, 23.16) * mm});
            skLineSegment(sketch, "E158.6.0.1", {"start": v(79.78, 68.25) * mm, "end": v(79.78, 23.16) * mm});
            skLineSegment(sketch, "E158.7.0.0", {"start": v(67.84, 68.25) * mm, "end": v(67.84, 23.16) * mm});
            skLineSegment(sketch, "E158.7.0.1", {"start": v(67.08, 68.25) * mm, "end": v(67.08, 23.16) * mm});
            skLineSegment(sketch, "E158.8.0.0", {"start": v(55.14, 68.25) * mm, "end": v(55.14, 23.16) * mm});
            skLineSegment(sketch, "E158.8.0.1", {"start": v(54.38, 68.25) * mm, "end": v(54.38, 23.16) * mm});
            skLineSegment(sketch, "E158.9.0.0", {"start": v(42.44, 68.25) * mm, "end": v(42.44, 23.16) * mm});
            skLineSegment(sketch, "E158.9.0.1", {"start": v(41.68, 68.25) * mm, "end": v(41.68, 23.16) * mm});
            skLineSegment(sketch, "E158.10.0.0", {"start": v(29.74, 68.25) * mm, "end": v(29.74, 23.16) * mm});
            skLineSegment(sketch, "E158.10.0.1", {"start": v(28.98, 68.25) * mm, "end": v(28.98, 23.16) * mm});
            skLineSegment(sketch, "E158.11.0.0", {"start": v(17.04, 68.25) * mm, "end": v(17.04, 23.16) * mm});
            skLineSegment(sketch, "E158.11.0.1", {"start": v(16.28, 68.25) * mm, "end": v(16.28, 23.16) * mm});
            skLineSegment(sketch, "E158.direction1", {"start": v(156.74, 23.16) * mm, "end": v(144.04, 23.16) * mm, "construction": true});
            skSolve(sketch);
        }
        {
            var Q0;
            {var subQ0=sQuery(id+"F24.wireOp",EDGE,"E155.right");Q0=makeQuery(id+"F24.imprint","IMPRINT",FACE,{"disambiguationData":[TD([[makeQuery(id+"F24.imprint","IMPRINT",EDGE,{"derivedFrom":subQ0}),1.0]])]});}
            var Q1;
            {var subQ0=sQuery(id+"F24.wireOp",EDGE,"E158.10.0.1");Q1=makeQuery(id+"F24.imprint","IMPRINT",FACE,{"disambiguationData":[TD([[makeQuery(id+"F24.imprint","IMPRINT",EDGE,{"derivedFrom":subQ0}),-1.0]])]});}
            var Q2;
            {var subQ0=sQuery(id+"F24.wireOp",EDGE,"E158.9.0.1");Q2=makeQuery(id+"F24.imprint","IMPRINT",FACE,{"disambiguationData":[TD([[makeQuery(id+"F24.imprint","IMPRINT",EDGE,{"derivedFrom":subQ0}),-1.0]])]});}
            var Q3;
            {var subQ0=sQuery(id+"F24.wireOp",EDGE,"E158.8.0.1");Q3=makeQuery(id+"F24.imprint","IMPRINT",FACE,{"disambiguationData":[TD([[makeQuery(id+"F24.imprint","IMPRINT",EDGE,{"derivedFrom":subQ0}),-1.0]])]});}
            var Q4;
            {var subQ0=sQuery(id+"F24.wireOp",EDGE,"E158.7.0.1");Q4=makeQuery(id+"F24.imprint","IMPRINT",FACE,{"disambiguationData":[TD([[makeQuery(id+"F24.imprint","IMPRINT",EDGE,{"derivedFrom":subQ0}),-1.0]])]});}
            var Q5;
            {var subQ0=sQuery(id+"F24.wireOp",EDGE,"E158.6.0.1");Q5=makeQuery(id+"F24.imprint","IMPRINT",FACE,{"disambiguationData":[TD([[makeQuery(id+"F24.imprint","IMPRINT",EDGE,{"derivedFrom":subQ0}),-1.0]])]});}
            var Q6;
            {var subQ0=sQuery(id+"F24.wireOp",EDGE,"E158.5.0.1");Q6=makeQuery(id+"F24.imprint","IMPRINT",FACE,{"disambiguationData":[TD([[makeQuery(id+"F24.imprint","IMPRINT",EDGE,{"derivedFrom":subQ0}),-1.0]])]});}
            var Q7;
            {var subQ0=sQuery(id+"F24.wireOp",EDGE,"E158.4.0.1");Q7=makeQuery(id+"F24.imprint","IMPRINT",FACE,{"disambiguationData":[TD([[makeQuery(id+"F24.imprint","IMPRINT",EDGE,{"derivedFrom":subQ0}),-1.0]])]});}
            var Q8;
            {var subQ0=sQuery(id+"F24.wireOp",EDGE,"E158.3.0.1");Q8=makeQuery(id+"F24.imprint","IMPRINT",FACE,{"disambiguationData":[TD([[makeQuery(id+"F24.imprint","IMPRINT",EDGE,{"derivedFrom":subQ0}),-1.0]])]});}
            var Q9;
            {var subQ0=sQuery(id+"F24.wireOp",EDGE,"E158.2.0.1");Q9=makeQuery(id+"F24.imprint","IMPRINT",FACE,{"disambiguationData":[TD([[makeQuery(id+"F24.imprint","IMPRINT",EDGE,{"derivedFrom":subQ0}),-1.0]])]});}
            var Q10;
            {var subQ0=sQuery(id+"F24.wireOp",EDGE,"E158.1.0.1");Q10=makeQuery(id+"F24.imprint","IMPRINT",FACE,{"disambiguationData":[TD([[makeQuery(id+"F24.imprint","IMPRINT",EDGE,{"derivedFrom":subQ0}),-1.0]])]});}
            var Q11;
            {var subQ0=sQuery(id+"F24.wireOp",EDGE,"E157");Q11=makeQuery(id+"F24.imprint","IMPRINT",FACE,{"disambiguationData":[TD([[makeQuery(id+"F24.imprint","IMPRINT",EDGE,{"derivedFrom":subQ0}),-1.0]])]});}
            var Q12;
            {var subQ0=sQuery(id+"F24.wireOp",EDGE,"E155.left");Q12=makeQuery(id+"F24.imprint","IMPRINT",FACE,{"disambiguationData":[TD([[makeQuery(id+"F24.imprint","IMPRINT",EDGE,{"derivedFrom":subQ0}),-1.0]])]});}
            extrude(context, id + "F25", {"entities" : qUnion([Q0, Q1, Q2, Q3, Q4, Q5, Q6, Q7, Q8, Q9, Q10, Q11, Q12]), "operationType" : NewBodyOperationType.REMOVE, "oppositeDirection" : true, "depth" : 25.4 * mm, "offsetDistance" : 25.4 * mm});
        }
        {
            var Q0;
            Q0=makeQuery(id+"F2.opExtrude","SWEPT_FACE",FACE,{"disambiguationData":[OSD([sQuery(id+"F1.wireOp",EDGE,"E8.0")])]});
            var sketch = newSketch(context, id + "F26", { "sketchPlane" : qUnion([Q0])});
            skLineSegment(sketch, "E159", {"start": v(3.18, 1.9) * mm, "end": v(3.18, 9.52) * mm, "construction": true});
            skLineSegment(sketch, "E160", {"start": v(18.42, 9.52) * mm, "end": v(13.49, 9.52) * mm});
            skLineSegment(sketch, "E161", {"start": v(3.17, 1.9) * mm, "end": v(10.8, 9.53) * mm, "construction": true});
            skLineSegment(sketch, "E162", {"start": v(10.8, 9.52) * mm, "end": v(18.42, 1.9) * mm, "construction": true});
            skLineSegment(sketch, "E163", {"start": v(3.18, 1.9) * mm, "end": v(18.42, 1.9) * mm, "construction": true});
            skLineSegment(sketch, "E164.0", {"start": v(10.8, 6.83) * mm, "end": v(15.72, 1.9) * mm});
            skLineSegment(sketch, "E164.1", {"start": v(5.87, 1.9) * mm, "end": v(10.8, 6.83) * mm});
            skLineSegment(sketch, "E165.0", {"start": v(13.49, 9.53) * mm, "end": v(18.42, 4.6) * mm});
            skLineSegment(sketch, "E165.1", {"start": v(3.18, 4.6) * mm, "end": v(8.1, 9.53) * mm});
            skLineSegment(sketch, "E166.trimOffspring", {"start": v(8.1, 9.52) * mm, "end": v(3.17, 9.52) * mm});
            skLineSegment(sketch, "E167", {"start": v(8.1, 9.52) * mm, "end": v(13.49, 9.53) * mm, "construction": true});
            skLineSegment(sketch, "E168", {"start": v(18.42, 1.9) * mm, "end": v(18.42, 4.6) * mm, "construction": true});
            skLineSegment(sketch, "E169", {"start": v(18.42, 4.6) * mm, "end": v(18.42, 9.52) * mm, "construction": true});
            skLineSegment(sketch, "E170", {"start": v(10.8, 9.52) * mm, "end": v(10.8, 1.9) * mm, "construction": true});
            skLineSegment(sketch, "E171", {"start": v(3.17, 11.43) * mm, "end": v(18.42, 11.43) * mm, "construction": true});
            skLineSegment(sketch, "E172", {"start": v(3.18, 0) * mm, "end": v(18.42, 0) * mm, "construction": true});
            skLineSegment(sketch, "E173", {"start": v(18.42, 11.43) * mm, "end": v(18.42, 9.52) * mm, "construction": true});
            skLineSegment(sketch, "E174", {"start": v(18.42, 0) * mm, "end": v(18.42, 1.9) * mm, "construction": true});
            skLineSegment(sketch, "E175", {"start": v(13.26, 4.37) * mm, "end": v(14.6, 5.71) * mm, "construction": true});
            skLineSegment(sketch, "E176", {"start": v(5.87, 1.9) * mm, "end": v(15.72, 1.9) * mm});
            skLineSegment(sketch, "E177", {"start": v(3.18, 4.6) * mm, "end": v(3.18, 9.52) * mm});
            skLineSegment(sketch, "E178.MirrorCS", {"start": v(33.66, 4.6) * mm, "end": v(33.66, 9.52) * mm, "construction": true});
            skLineSegment(sketch, "E179.MirrorCS", {"start": v(28.73, 9.52) * mm, "end": v(33.66, 9.52) * mm});
            skLineSegment(sketch, "E180.MirrorCS", {"start": v(33.66, 4.6) * mm, "end": v(28.73, 9.53) * mm});
            skLineSegment(sketch, "E181.MirrorCS", {"start": v(30.96, 1.9) * mm, "end": v(21.1, 1.9) * mm});
            skLineSegment(sketch, "E182.MirrorCS", {"start": v(30.96, 1.9) * mm, "end": v(26.04, 6.83) * mm});
            skLineSegment(sketch, "E183.MirrorCS", {"start": v(26.04, 6.83) * mm, "end": v(21.1, 1.9) * mm});
            skLineSegment(sketch, "E184.MirrorCS", {"start": v(18.42, 9.52) * mm, "end": v(23.34, 9.52) * mm});
            skLineSegment(sketch, "E185.MirrorCS", {"start": v(23.34, 9.53) * mm, "end": v(18.41, 4.6) * mm});
            skLineSegment(sketch, "E186.MirrorCS", {"start": v(38.58, 9.53) * mm, "end": v(33.66, 9.52) * mm});
            skLineSegment(sketch, "E187.MirrorCS", {"start": v(33.65, 4.6) * mm, "end": v(38.58, 9.53) * mm});
            skLineSegment(sketch, "E188.MirrorCS", {"start": v(36.35, 1.9) * mm, "end": v(46.2, 1.9) * mm});
            skLineSegment(sketch, "E189.MirrorCS", {"start": v(36.35, 1.9) * mm, "end": v(41.27, 6.83) * mm});
            skLineSegment(sketch, "E190.MirrorCS", {"start": v(41.28, 6.83) * mm, "end": v(46.2, 1.9) * mm});
            skLineSegment(sketch, "E191.MirrorCS", {"start": v(43.97, 9.53) * mm, "end": v(48.9, 4.6) * mm});
            skLineSegment(sketch, "E192.MirrorCS", {"start": v(48.9, 9.53) * mm, "end": v(43.97, 9.53) * mm});
            skLineSegment(sketch, "E193", {"start": v(48.9, 9.53) * mm, "end": v(48.9, 4.6) * mm, "construction": true});
            skLineSegment(sketch, "E194.MirrorCS", {"start": v(3.18, 18.26) * mm, "end": v(3.18, 13.34) * mm});
            skLineSegment(sketch, "E195.MirrorCS", {"start": v(8.1, 13.34) * mm, "end": v(3.17, 13.34) * mm});
            skLineSegment(sketch, "E196.MirrorCS", {"start": v(3.17, 18.26) * mm, "end": v(8.1, 13.33) * mm});
            skLineSegment(sketch, "E197.MirrorCS", {"start": v(5.87, 20.95) * mm, "end": v(10.8, 16.03) * mm});
            skLineSegment(sketch, "E198.MirrorCS", {"start": v(10.8, 16.03) * mm, "end": v(15.72, 20.96) * mm});
            skLineSegment(sketch, "E199.MirrorCS", {"start": v(5.87, 20.95) * mm, "end": v(15.72, 20.96) * mm});
            skLineSegment(sketch, "E200.MirrorCS", {"start": v(13.49, 13.33) * mm, "end": v(18.41, 18.26) * mm});
            skLineSegment(sketch, "E201.MirrorCS", {"start": v(18.41, 13.34) * mm, "end": v(13.49, 13.34) * mm});
            skLineSegment(sketch, "E202.MirrorCS", {"start": v(18.41, 13.34) * mm, "end": v(23.34, 13.34) * mm});
            skLineSegment(sketch, "E203.MirrorCS", {"start": v(23.34, 13.33) * mm, "end": v(18.41, 18.26) * mm});
            skLineSegment(sketch, "E204.MirrorCS", {"start": v(26.04, 16.03) * mm, "end": v(21.1, 20.95) * mm});
            skLineSegment(sketch, "E205.MirrorCS", {"start": v(30.96, 20.96) * mm, "end": v(21.1, 20.96) * mm});
            skLineSegment(sketch, "E206.MirrorCS", {"start": v(30.96, 20.95) * mm, "end": v(26.04, 16.03) * mm});
            skLineSegment(sketch, "E207.MirrorCS", {"start": v(33.66, 18.26) * mm, "end": v(28.73, 13.33) * mm});
            skLineSegment(sketch, "E208.MirrorCS", {"start": v(28.73, 13.34) * mm, "end": v(33.66, 13.34) * mm});
            skLineSegment(sketch, "E209.MirrorCS", {"start": v(38.58, 13.34) * mm, "end": v(33.66, 13.34) * mm});
            skLineSegment(sketch, "E210.MirrorCS", {"start": v(33.65, 18.26) * mm, "end": v(38.58, 13.33) * mm});
            skLineSegment(sketch, "E211.MirrorCS", {"start": v(41.28, 16.03) * mm, "end": v(46.2, 20.95) * mm});
            skLineSegment(sketch, "E212.MirrorCS", {"start": v(36.35, 20.95) * mm, "end": v(41.27, 16.03) * mm});
            skLineSegment(sketch, "E213.MirrorCS", {"start": v(36.35, 20.96) * mm, "end": v(46.2, 20.96) * mm});
            skLineSegment(sketch, "E214.MirrorCS", {"start": v(43.97, 13.33) * mm, "end": v(48.9, 18.26) * mm});
            skLineSegment(sketch, "E215.MirrorCS", {"start": v(48.9, 13.34) * mm, "end": v(43.97, 13.34) * mm});
            skLineSegment(sketch, "E216.MirrorCS", {"start": v(48.9, 13.33) * mm, "end": v(48.9, 18.26) * mm, "construction": true});
            skLineSegment(sketch, "E217.MirrorCS", {"start": v(53.82, 9.53) * mm, "end": v(48.9, 4.6) * mm});
            skLineSegment(sketch, "E218.MirrorCS", {"start": v(48.9, 9.53) * mm, "end": v(53.82, 9.53) * mm});
            skLineSegment(sketch, "E219.MirrorCS", {"start": v(48.9, 13.34) * mm, "end": v(53.82, 13.34) * mm});
            skLineSegment(sketch, "E220.MirrorCS", {"start": v(53.82, 13.33) * mm, "end": v(48.9, 18.26) * mm});
            skLineSegment(sketch, "E221.MirrorCS", {"start": v(56.52, 16.03) * mm, "end": v(51.59, 20.96) * mm});
            skLineSegment(sketch, "E222.MirrorCS", {"start": v(61.44, 20.96) * mm, "end": v(51.59, 20.96) * mm});
            skLineSegment(sketch, "E223.MirrorCS", {"start": v(61.44, 20.95) * mm, "end": v(56.52, 16.03) * mm});
            skLineSegment(sketch, "E224.MirrorCS", {"start": v(64.14, 18.26) * mm, "end": v(59.2, 13.33) * mm});
            skLineSegment(sketch, "E225.MirrorCS", {"start": v(59.2, 13.34) * mm, "end": v(64.14, 13.34) * mm});
            skLineSegment(sketch, "E226.MirrorCS", {"start": v(59.2, 9.53) * mm, "end": v(64.14, 9.53) * mm});
            skLineSegment(sketch, "E227.MirrorCS", {"start": v(64.14, 4.6) * mm, "end": v(59.2, 9.53) * mm});
            skLineSegment(sketch, "E228.MirrorCS", {"start": v(56.52, 6.83) * mm, "end": v(51.59, 1.9) * mm});
            skLineSegment(sketch, "E229.MirrorCS", {"start": v(61.44, 1.9) * mm, "end": v(56.52, 6.83) * mm});
            skLineSegment(sketch, "E230.MirrorCS", {"start": v(61.44, 1.9) * mm, "end": v(51.59, 1.9) * mm});
            skLineSegment(sketch, "E231", {"start": v(64.14, 18.26) * mm, "end": v(64.14, 13.34) * mm});
            skLineSegment(sketch, "E232", {"start": v(64.14, 9.53) * mm, "end": v(64.14, 4.6) * mm});
            skLineSegment(sketch, "E233", {"start": v(101.2, 0) * mm, "end": v(101.2, 18.7) * mm, "construction": true});
            skLineSegment(sketch, "E234.MirrorCS", {"start": v(153.5, 9.52) * mm, "end": v(153.5, 4.6) * mm, "construction": true});
            skLineSegment(sketch, "E235.MirrorCS", {"start": v(153.5, 13.34) * mm, "end": v(153.5, 18.26) * mm, "construction": true});
            skLineSegment(sketch, "E236.MirrorCS", {"start": v(168.73, 4.6) * mm, "end": v(168.73, 9.53) * mm, "construction": true});
            skLineSegment(sketch, "E237.MirrorCS", {"start": v(138.25, 4.6) * mm, "end": v(143.18, 9.53) * mm});
            skLineSegment(sketch, "E238.MirrorCS", {"start": v(145.87, 16.03) * mm, "end": v(150.8, 20.95) * mm});
            skLineSegment(sketch, "E239.MirrorCS", {"start": v(138.25, 18.26) * mm, "end": v(138.25, 13.33) * mm});
            skLineSegment(sketch, "E240.MirrorCS", {"start": v(168.73, 18.26) * mm, "end": v(163.8, 13.34) * mm});
            skLineSegment(sketch, "E241.MirrorCS", {"start": v(143.18, 9.53) * mm, "end": v(138.25, 9.53) * mm});
            skLineSegment(sketch, "E242.MirrorCS", {"start": v(153.5, 9.53) * mm, "end": v(148.56, 9.53) * mm});
            skLineSegment(sketch, "E243.MirrorCS", {"start": v(153.5, 13.34) * mm, "end": v(148.56, 13.34) * mm});
            skLineSegment(sketch, "E244.MirrorCS", {"start": v(138.25, 9.53) * mm, "end": v(138.25, 4.6) * mm});
            skLineSegment(sketch, "E245.MirrorCS", {"start": v(158.42, 13.34) * mm, "end": v(153.5, 18.26) * mm});
            skLineSegment(sketch, "E246.MirrorCS", {"start": v(148.56, 9.53) * mm, "end": v(153.5, 4.6) * mm});
            skLineSegment(sketch, "E247.MirrorCS", {"start": v(163.8, 9.53) * mm, "end": v(168.73, 9.53) * mm});
            skLineSegment(sketch, "E248.MirrorCS", {"start": v(163.8, 13.34) * mm, "end": v(168.73, 13.34) * mm});
            skLineSegment(sketch, "E249.MirrorCS", {"start": v(138.25, 18.26) * mm, "end": v(143.18, 13.34) * mm});
            skLineSegment(sketch, "E250.MirrorCS", {"start": v(143.18, 13.34) * mm, "end": v(138.25, 13.34) * mm});
            skLineSegment(sketch, "E251.MirrorCS", {"start": v(148.56, 13.34) * mm, "end": v(153.5, 18.26) * mm});
            skLineSegment(sketch, "E252.MirrorCS", {"start": v(153.5, 9.53) * mm, "end": v(158.42, 9.53) * mm});
            skLineSegment(sketch, "E253.MirrorCS", {"start": v(153.5, 13.34) * mm, "end": v(158.42, 13.34) * mm});
            skLineSegment(sketch, "E254.MirrorCS", {"start": v(140.94, 20.96) * mm, "end": v(145.87, 16.03) * mm});
            skLineSegment(sketch, "E255.MirrorCS", {"start": v(161.11, 16.03) * mm, "end": v(156.18, 20.96) * mm});
            skLineSegment(sketch, "E256.MirrorCS", {"start": v(161.11, 6.83) * mm, "end": v(156.18, 1.9) * mm});
            skLineSegment(sketch, "E257.MirrorCS", {"start": v(145.87, 6.83) * mm, "end": v(150.8, 1.9) * mm});
            skLineSegment(sketch, "E258.MirrorCS", {"start": v(166.04, 1.9) * mm, "end": v(156.18, 1.9) * mm});
            skLineSegment(sketch, "E259.MirrorCS", {"start": v(140.94, 1.9) * mm, "end": v(145.87, 6.83) * mm});
            skLineSegment(sketch, "E260.MirrorCS", {"start": v(140.94, 20.96) * mm, "end": v(150.8, 20.96) * mm});
            skLineSegment(sketch, "E261.MirrorCS", {"start": v(158.42, 9.53) * mm, "end": v(153.5, 4.6) * mm});
            skLineSegment(sketch, "E262.MirrorCS", {"start": v(166.04, 20.96) * mm, "end": v(156.18, 20.96) * mm});
            skLineSegment(sketch, "E263.MirrorCS", {"start": v(168.73, 4.6) * mm, "end": v(163.8, 9.53) * mm});
            skLineSegment(sketch, "E264.MirrorCS", {"start": v(140.94, 1.9) * mm, "end": v(150.8, 1.9) * mm});
            skLineSegment(sketch, "E265.MirrorCS", {"start": v(166.04, 1.9) * mm, "end": v(161.11, 6.83) * mm});
            skLineSegment(sketch, "E266.MirrorCS", {"start": v(166.04, 20.96) * mm, "end": v(161.11, 16.03) * mm});
            skLineSegment(sketch, "E267", {"start": v(161.11, 16.03) * mm, "end": v(161.11, 20.96) * mm});
            skLineSegment(sketch, "E268", {"start": v(168.73, 9.53) * mm, "end": v(168.73, 4.6) * mm});
            skLineSegment(sketch, "E269", {"start": v(168.73, 13.33) * mm, "end": v(168.73, 18.26) * mm});
            skPoint(sketch, "E270.MirrorCS.end.orphan", {"position": v(173.66, 13.33) * mm});
            skPoint(sketch, "E270.MirrorCS.start.orphan", {"position": v(168.73, 18.26) * mm});
            skPoint(sketch, "E271.MirrorCS.end.orphan", {"position": v(168.73, 9.53) * mm});
            skPoint(sketch, "E272.MirrorCS.end.orphan", {"position": v(173.66, 9.53) * mm});
            skLineSegment(sketch, "E273", {"start": v(161.11, 6.83) * mm, "end": v(161.11, 1.9) * mm});
            skSolve(sketch);
        }
        {
            var Q0;
            Q0=qSketchRegion(id+"F26",true);
            extrude(context, id + "F27", {"entities" : qUnion([Q0]), "operationType" : NewBodyOperationType.REMOVE, "endBound" : BoundingType.UP_TO_NEXT, "oppositeDirection" : true, "depth" : 25.4 * mm, "offsetDistance" : 25.4 * mm});
        }
        {
            var Q0;
            Q0=makeQuery(id+"F6.boolean.opBoolean","MERGE",FACE,{"derivedFrom":[makeQuery(id+"F2.opExtrude","SWEPT_FACE",FACE,{"disambiguationData":[OSD([sQuery(id+"F1.wireOp",EDGE,"E9.2")])]}),makeQuery(id+"F6.opExtrude","SWEPT_FACE",FACE,{"disambiguationData":[OSD([sQuery(id+"F5.wireOp",EDGE,"E60.top")])]})]});
            var sketch = newSketch(context, id + "F28", { "sketchPlane" : qUnion([Q0])});
            skLineSegment(sketch, "E274.3", {"start": v(3.17, 18.26) * mm, "end": v(8.1, 13.33) * mm});
            skLineSegment(sketch, "E274.4", {"start": v(3.18, 18.26) * mm, "end": v(3.18, 13.33) * mm, "construction": true});
            skLineSegment(sketch, "E274.5", {"start": v(8.1, 13.34) * mm, "end": v(3.18, 13.34) * mm});
            skLineSegment(sketch, "E274.12", {"start": v(5.87, 1.9) * mm, "end": v(15.72, 1.9) * mm});
            skLineSegment(sketch, "E275.MirrorCS", {"start": v(0.48, 20.95) * mm, "end": v(-4.44, 16.03) * mm});
            skLineSegment(sketch, "E276.MirrorCS", {"start": v(-1.75, 13.34) * mm, "end": v(3.17, 13.34) * mm});
            skLineSegment(sketch, "E277.MirrorCS", {"start": v(3.18, 18.26) * mm, "end": v(-1.75, 13.33) * mm});
            skLineSegment(sketch, "E278", {"start": v(-4.44, 16.03) * mm, "end": v(-4.44, 20.95) * mm});
            skLineSegment(sketch, "E279", {"start": v(-4.44, 20.95) * mm, "end": v(0.48, 20.95) * mm});
            skLineSegment(sketch, "E280.0.1.0", {"start": v(3.17, 41.12) * mm, "end": v(8.1, 36.2) * mm});
            skLineSegment(sketch, "E280.0.1.1", {"start": v(8.1, 36.2) * mm, "end": v(3.18, 36.2) * mm});
            skLineSegment(sketch, "E280.0.1.2", {"start": v(3.18, 41.12) * mm, "end": v(-1.75, 36.2) * mm});
            skLineSegment(sketch, "E280.0.1.3", {"start": v(-1.75, 36.2) * mm, "end": v(3.18, 36.2) * mm});
            skLineSegment(sketch, "E280.0.1.4", {"start": v(-1.75, 32.38) * mm, "end": v(3.17, 32.38) * mm});
            skLineSegment(sketch, "E280.0.1.5", {"start": v(3.18, 27.46) * mm, "end": v(-1.75, 32.39) * mm});
            skLineSegment(sketch, "E280.0.1.6", {"start": v(8.1, 32.38) * mm, "end": v(3.17, 32.38) * mm});
            skLineSegment(sketch, "E280.0.1.7", {"start": v(3.18, 27.46) * mm, "end": v(8.1, 32.39) * mm});
            skLineSegment(sketch, "E280.0.1.8", {"start": v(5.87, 24.77) * mm, "end": v(10.8, 29.7) * mm});
            skLineSegment(sketch, "E280.0.1.9", {"start": v(10.8, 29.7) * mm, "end": v(15.72, 24.76) * mm});
            skLineSegment(sketch, "E280.0.1.10", {"start": v(5.87, 24.76) * mm, "end": v(15.72, 24.76) * mm});
            skLineSegment(sketch, "E280.0.1.11", {"start": v(5.87, 43.81) * mm, "end": v(10.8, 38.89) * mm});
            skLineSegment(sketch, "E280.0.1.12", {"start": v(5.87, 43.81) * mm, "end": v(15.72, 43.81) * mm});
            skLineSegment(sketch, "E280.0.1.13", {"start": v(10.8, 38.89) * mm, "end": v(15.72, 43.81) * mm});
            skLineSegment(sketch, "E280.0.2.0", {"start": v(3.17, 63.98) * mm, "end": v(8.1, 59.05) * mm});
            skLineSegment(sketch, "E280.0.2.1", {"start": v(8.1, 59.05) * mm, "end": v(3.18, 59.05) * mm});
            skLineSegment(sketch, "E280.0.2.2", {"start": v(3.17, 63.98) * mm, "end": v(-1.75, 59.05) * mm});
            skLineSegment(sketch, "E280.0.2.3", {"start": v(-1.75, 59.05) * mm, "end": v(3.18, 59.05) * mm});
            skLineSegment(sketch, "E280.0.2.4", {"start": v(-1.75, 55.24) * mm, "end": v(3.17, 55.24) * mm});
            skLineSegment(sketch, "E280.0.2.5", {"start": v(3.18, 50.32) * mm, "end": v(-1.75, 55.24) * mm});
            skLineSegment(sketch, "E280.0.2.6", {"start": v(8.1, 55.24) * mm, "end": v(3.17, 55.24) * mm});
            skLineSegment(sketch, "E280.0.2.7", {"start": v(3.18, 50.32) * mm, "end": v(8.1, 55.25) * mm});
            skLineSegment(sketch, "E280.0.2.8", {"start": v(5.87, 47.62) * mm, "end": v(10.8, 52.55) * mm});
            skLineSegment(sketch, "E280.0.2.9", {"start": v(10.8, 52.55) * mm, "end": v(15.72, 47.62) * mm});
            skLineSegment(sketch, "E280.0.2.10", {"start": v(5.87, 47.62) * mm, "end": v(15.72, 47.62) * mm});
            skLineSegment(sketch, "E280.0.2.11", {"start": v(5.87, 66.67) * mm, "end": v(10.8, 61.75) * mm});
            skLineSegment(sketch, "E280.0.2.12", {"start": v(5.87, 66.67) * mm, "end": v(15.72, 66.67) * mm});
            skLineSegment(sketch, "E280.0.2.13", {"start": v(10.8, 61.75) * mm, "end": v(15.72, 66.67) * mm});
            skLineSegment(sketch, "E280.1.1.0", {"start": v(18.41, 41.12) * mm, "end": v(23.34, 36.2) * mm});
            skLineSegment(sketch, "E280.1.1.1", {"start": v(23.34, 36.2) * mm, "end": v(18.41, 36.2) * mm});
            skLineSegment(sketch, "E280.1.1.2", {"start": v(18.41, 41.12) * mm, "end": v(13.49, 36.2) * mm});
            skLineSegment(sketch, "E280.1.1.3", {"start": v(13.49, 36.2) * mm, "end": v(18.41, 36.2) * mm});
            skLineSegment(sketch, "E280.1.1.4", {"start": v(13.49, 32.38) * mm, "end": v(18.41, 32.38) * mm});
            skLineSegment(sketch, "E280.1.1.5", {"start": v(18.41, 27.46) * mm, "end": v(13.49, 32.39) * mm});
            skLineSegment(sketch, "E280.1.1.6", {"start": v(23.34, 32.38) * mm, "end": v(18.41, 32.38) * mm});
            skLineSegment(sketch, "E280.1.1.7", {"start": v(18.41, 27.46) * mm, "end": v(23.34, 32.39) * mm});
            skLineSegment(sketch, "E280.1.1.8", {"start": v(21.1, 24.77) * mm, "end": v(26.03, 29.7) * mm});
            skLineSegment(sketch, "E280.1.1.9", {"start": v(26.03, 29.7) * mm, "end": v(30.96, 24.76) * mm});
            skLineSegment(sketch, "E280.1.1.10", {"start": v(21.1, 24.76) * mm, "end": v(30.96, 24.76) * mm});
            skLineSegment(sketch, "E280.1.1.11", {"start": v(21.1, 43.81) * mm, "end": v(26.03, 38.89) * mm});
            skLineSegment(sketch, "E280.1.1.12", {"start": v(21.1, 43.81) * mm, "end": v(30.96, 43.81) * mm});
            skLineSegment(sketch, "E280.1.1.13", {"start": v(26.03, 38.89) * mm, "end": v(30.96, 43.81) * mm});
            skLineSegment(sketch, "E280.1.2.0", {"start": v(18.41, 63.98) * mm, "end": v(23.34, 59.05) * mm});
            skLineSegment(sketch, "E280.1.2.1", {"start": v(23.34, 59.05) * mm, "end": v(18.41, 59.05) * mm});
            skLineSegment(sketch, "E280.1.2.2", {"start": v(18.41, 63.98) * mm, "end": v(13.49, 59.05) * mm});
            skLineSegment(sketch, "E280.1.2.3", {"start": v(13.49, 59.05) * mm, "end": v(18.41, 59.05) * mm});
            skLineSegment(sketch, "E280.1.2.4", {"start": v(13.49, 55.24) * mm, "end": v(18.41, 55.24) * mm});
            skLineSegment(sketch, "E280.1.2.5", {"start": v(18.41, 50.32) * mm, "end": v(13.49, 55.24) * mm});
            skLineSegment(sketch, "E280.1.2.6", {"start": v(23.34, 55.24) * mm, "end": v(18.41, 55.24) * mm});
            skLineSegment(sketch, "E280.1.2.7", {"start": v(18.41, 50.32) * mm, "end": v(23.34, 55.25) * mm});
            skLineSegment(sketch, "E280.1.2.8", {"start": v(21.1, 47.62) * mm, "end": v(26.03, 52.55) * mm});
            skLineSegment(sketch, "E280.1.2.9", {"start": v(26.03, 52.55) * mm, "end": v(30.96, 47.62) * mm});
            skLineSegment(sketch, "E280.1.2.10", {"start": v(21.1, 47.62) * mm, "end": v(30.96, 47.62) * mm});
            skLineSegment(sketch, "E280.1.2.11", {"start": v(21.1, 66.67) * mm, "end": v(26.03, 61.75) * mm});
            skLineSegment(sketch, "E280.1.2.12", {"start": v(21.1, 66.67) * mm, "end": v(30.96, 66.67) * mm});
            skLineSegment(sketch, "E280.1.2.13", {"start": v(26.03, 61.75) * mm, "end": v(30.96, 66.67) * mm});
            skLineSegment(sketch, "E280.2.1.0", {"start": v(33.65, 41.12) * mm, "end": v(38.58, 36.2) * mm});
            skLineSegment(sketch, "E280.2.1.1", {"start": v(38.58, 36.2) * mm, "end": v(33.65, 36.2) * mm});
            skLineSegment(sketch, "E280.2.1.2", {"start": v(33.65, 41.12) * mm, "end": v(28.73, 36.2) * mm});
            skLineSegment(sketch, "E280.2.1.3", {"start": v(28.73, 36.2) * mm, "end": v(33.65, 36.2) * mm});
            skLineSegment(sketch, "E280.2.1.4", {"start": v(28.73, 32.38) * mm, "end": v(33.65, 32.38) * mm});
            skLineSegment(sketch, "E280.2.1.5", {"start": v(33.65, 27.46) * mm, "end": v(28.73, 32.39) * mm});
            skLineSegment(sketch, "E280.2.1.6", {"start": v(38.58, 32.38) * mm, "end": v(33.65, 32.38) * mm});
            skLineSegment(sketch, "E280.2.1.7", {"start": v(33.65, 27.46) * mm, "end": v(38.58, 32.39) * mm});
            skLineSegment(sketch, "E280.2.1.8", {"start": v(36.35, 24.77) * mm, "end": v(41.27, 29.7) * mm});
            skLineSegment(sketch, "E280.2.1.9", {"start": v(41.27, 29.7) * mm, "end": v(46.2, 24.76) * mm});
            skLineSegment(sketch, "E280.2.1.10", {"start": v(36.35, 24.76) * mm, "end": v(46.2, 24.76) * mm});
            skLineSegment(sketch, "E280.2.1.11", {"start": v(36.35, 43.81) * mm, "end": v(41.27, 38.89) * mm});
            skLineSegment(sketch, "E280.2.1.12", {"start": v(36.35, 43.81) * mm, "end": v(46.2, 43.81) * mm});
            skLineSegment(sketch, "E280.2.1.13", {"start": v(41.27, 38.89) * mm, "end": v(46.2, 43.81) * mm});
            skLineSegment(sketch, "E280.2.2.0", {"start": v(33.65, 63.98) * mm, "end": v(38.58, 59.05) * mm});
            skLineSegment(sketch, "E280.2.2.1", {"start": v(38.58, 59.05) * mm, "end": v(33.65, 59.05) * mm});
            skLineSegment(sketch, "E280.2.2.2", {"start": v(33.65, 63.98) * mm, "end": v(28.73, 59.05) * mm});
            skLineSegment(sketch, "E280.2.2.3", {"start": v(28.73, 59.05) * mm, "end": v(33.65, 59.05) * mm});
            skLineSegment(sketch, "E280.2.2.4", {"start": v(28.73, 55.24) * mm, "end": v(33.65, 55.24) * mm});
            skLineSegment(sketch, "E280.2.2.5", {"start": v(33.65, 50.32) * mm, "end": v(28.73, 55.24) * mm});
            skLineSegment(sketch, "E280.2.2.6", {"start": v(38.58, 55.24) * mm, "end": v(33.65, 55.24) * mm});
            skLineSegment(sketch, "E280.2.2.7", {"start": v(33.65, 50.32) * mm, "end": v(38.58, 55.25) * mm});
            skLineSegment(sketch, "E280.2.2.8", {"start": v(36.35, 47.62) * mm, "end": v(41.27, 52.55) * mm});
            skLineSegment(sketch, "E280.2.2.9", {"start": v(41.27, 52.55) * mm, "end": v(46.2, 47.62) * mm});
            skLineSegment(sketch, "E280.2.2.10", {"start": v(36.35, 47.62) * mm, "end": v(46.2, 47.62) * mm});
            skLineSegment(sketch, "E280.2.2.11", {"start": v(36.35, 66.67) * mm, "end": v(41.27, 61.75) * mm});
            skLineSegment(sketch, "E280.2.2.12", {"start": v(36.35, 66.67) * mm, "end": v(46.2, 66.67) * mm});
            skLineSegment(sketch, "E280.2.2.13", {"start": v(41.27, 61.75) * mm, "end": v(46.2, 66.67) * mm});
            skLineSegment(sketch, "E280.3.1.0", {"start": v(48.9, 41.12) * mm, "end": v(53.82, 36.2) * mm});
            skLineSegment(sketch, "E280.3.1.1", {"start": v(53.82, 36.2) * mm, "end": v(48.9, 36.2) * mm});
            skLineSegment(sketch, "E280.3.1.2", {"start": v(48.9, 41.12) * mm, "end": v(43.97, 36.2) * mm});
            skLineSegment(sketch, "E280.3.1.3", {"start": v(43.97, 36.2) * mm, "end": v(48.9, 36.2) * mm});
            skLineSegment(sketch, "E280.3.1.4", {"start": v(43.97, 32.38) * mm, "end": v(48.9, 32.38) * mm});
            skLineSegment(sketch, "E280.3.1.5", {"start": v(48.9, 27.46) * mm, "end": v(43.97, 32.39) * mm});
            skLineSegment(sketch, "E280.3.1.6", {"start": v(53.82, 32.38) * mm, "end": v(48.9, 32.38) * mm});
            skLineSegment(sketch, "E280.3.1.7", {"start": v(48.9, 27.46) * mm, "end": v(53.82, 32.39) * mm});
            skLineSegment(sketch, "E280.3.1.8", {"start": v(51.59, 24.77) * mm, "end": v(56.51, 29.7) * mm});
            skLineSegment(sketch, "E280.3.1.9", {"start": v(56.51, 29.7) * mm, "end": v(61.44, 24.76) * mm});
            skLineSegment(sketch, "E280.3.1.10", {"start": v(51.59, 24.76) * mm, "end": v(61.44, 24.76) * mm});
            skLineSegment(sketch, "E280.3.1.11", {"start": v(51.59, 43.81) * mm, "end": v(56.51, 38.89) * mm});
            skLineSegment(sketch, "E280.3.1.12", {"start": v(51.59, 43.81) * mm, "end": v(61.44, 43.81) * mm});
            skLineSegment(sketch, "E280.3.1.13", {"start": v(56.51, 38.89) * mm, "end": v(61.44, 43.81) * mm});
            skLineSegment(sketch, "E280.3.2.0", {"start": v(48.9, 63.98) * mm, "end": v(53.82, 59.05) * mm});
            skLineSegment(sketch, "E280.3.2.1", {"start": v(53.82, 59.05) * mm, "end": v(48.9, 59.05) * mm});
            skLineSegment(sketch, "E280.3.2.2", {"start": v(48.9, 63.98) * mm, "end": v(43.97, 59.05) * mm});
            skLineSegment(sketch, "E280.3.2.3", {"start": v(43.97, 59.05) * mm, "end": v(48.9, 59.05) * mm});
            skLineSegment(sketch, "E280.3.2.4", {"start": v(43.97, 55.24) * mm, "end": v(48.9, 55.24) * mm});
            skLineSegment(sketch, "E280.3.2.5", {"start": v(48.9, 50.32) * mm, "end": v(43.97, 55.24) * mm});
            skLineSegment(sketch, "E280.3.2.6", {"start": v(53.82, 55.24) * mm, "end": v(48.9, 55.24) * mm});
            skLineSegment(sketch, "E280.3.2.7", {"start": v(48.9, 50.32) * mm, "end": v(53.82, 55.24) * mm});
            skLineSegment(sketch, "E280.3.2.8", {"start": v(51.59, 47.62) * mm, "end": v(56.51, 52.55) * mm});
            skLineSegment(sketch, "E280.3.2.9", {"start": v(56.51, 52.55) * mm, "end": v(61.44, 47.62) * mm});
            skLineSegment(sketch, "E280.3.2.10", {"start": v(51.59, 47.62) * mm, "end": v(61.44, 47.62) * mm});
            skLineSegment(sketch, "E280.3.2.11", {"start": v(51.59, 66.67) * mm, "end": v(56.51, 61.75) * mm});
            skLineSegment(sketch, "E280.3.2.12", {"start": v(51.59, 66.67) * mm, "end": v(61.44, 66.67) * mm});
            skLineSegment(sketch, "E280.3.2.13", {"start": v(56.51, 61.75) * mm, "end": v(61.44, 66.67) * mm});
            skLineSegment(sketch, "E280.4.1.0", {"start": v(64.13, 41.12) * mm, "end": v(69.06, 36.2) * mm});
            skLineSegment(sketch, "E280.4.1.1", {"start": v(69.06, 36.2) * mm, "end": v(64.13, 36.2) * mm});
            skLineSegment(sketch, "E280.4.1.2", {"start": v(64.13, 41.12) * mm, "end": v(59.2, 36.2) * mm});
            skLineSegment(sketch, "E280.4.1.3", {"start": v(59.2, 36.2) * mm, "end": v(64.13, 36.2) * mm});
            skLineSegment(sketch, "E280.4.1.4", {"start": v(59.2, 32.38) * mm, "end": v(64.13, 32.38) * mm});
            skLineSegment(sketch, "E280.4.1.5", {"start": v(64.13, 27.46) * mm, "end": v(59.2, 32.39) * mm});
            skLineSegment(sketch, "E280.4.1.6", {"start": v(69.06, 32.38) * mm, "end": v(64.13, 32.38) * mm});
            skLineSegment(sketch, "E280.4.1.7", {"start": v(64.13, 27.46) * mm, "end": v(69.06, 32.39) * mm});
            skLineSegment(sketch, "E280.4.1.8", {"start": v(66.83, 24.77) * mm, "end": v(71.75, 29.7) * mm});
            skLineSegment(sketch, "E280.4.1.9", {"start": v(71.75, 29.7) * mm, "end": v(76.68, 24.76) * mm});
            skLineSegment(sketch, "E280.4.1.10", {"start": v(66.83, 24.76) * mm, "end": v(76.68, 24.76) * mm});
            skLineSegment(sketch, "E280.4.1.11", {"start": v(66.83, 43.81) * mm, "end": v(71.75, 38.89) * mm});
            skLineSegment(sketch, "E280.4.1.12", {"start": v(66.83, 43.81) * mm, "end": v(76.68, 43.81) * mm});
            skLineSegment(sketch, "E280.4.1.13", {"start": v(71.75, 38.89) * mm, "end": v(76.68, 43.81) * mm});
            skLineSegment(sketch, "E280.4.2.0", {"start": v(64.13, 63.98) * mm, "end": v(69.06, 59.05) * mm});
            skLineSegment(sketch, "E280.4.2.1", {"start": v(69.06, 59.05) * mm, "end": v(64.13, 59.05) * mm});
            skLineSegment(sketch, "E280.4.2.2", {"start": v(64.13, 63.98) * mm, "end": v(59.2, 59.05) * mm});
            skLineSegment(sketch, "E280.4.2.3", {"start": v(59.2, 59.05) * mm, "end": v(64.13, 59.05) * mm});
            skLineSegment(sketch, "E280.4.2.4", {"start": v(59.2, 55.24) * mm, "end": v(64.13, 55.24) * mm});
            skLineSegment(sketch, "E280.4.2.5", {"start": v(64.13, 50.32) * mm, "end": v(59.2, 55.24) * mm});
            skLineSegment(sketch, "E280.4.2.6", {"start": v(69.06, 55.24) * mm, "end": v(64.13, 55.24) * mm});
            skLineSegment(sketch, "E280.4.2.7", {"start": v(64.13, 50.32) * mm, "end": v(69.06, 55.25) * mm});
            skLineSegment(sketch, "E280.4.2.8", {"start": v(66.83, 47.62) * mm, "end": v(71.75, 52.55) * mm});
            skLineSegment(sketch, "E280.4.2.9", {"start": v(71.75, 52.55) * mm, "end": v(76.68, 47.62) * mm});
            skLineSegment(sketch, "E280.4.2.10", {"start": v(66.83, 47.62) * mm, "end": v(76.68, 47.62) * mm});
            skLineSegment(sketch, "E280.4.2.11", {"start": v(66.83, 66.67) * mm, "end": v(71.75, 61.75) * mm});
            skLineSegment(sketch, "E280.4.2.12", {"start": v(66.83, 66.67) * mm, "end": v(76.68, 66.67) * mm});
            skLineSegment(sketch, "E280.4.2.13", {"start": v(71.75, 61.75) * mm, "end": v(76.68, 66.67) * mm});
            skLineSegment(sketch, "E280.5.0.0", {"start": v(79.37, 18.26) * mm, "end": v(84.3, 13.33) * mm});
            skLineSegment(sketch, "E280.5.0.1", {"start": v(84.3, 13.34) * mm, "end": v(79.38, 13.34) * mm});
            skLineSegment(sketch, "E280.5.0.2", {"start": v(79.38, 18.26) * mm, "end": v(74.45, 13.33) * mm});
            skLineSegment(sketch, "E280.5.0.3", {"start": v(74.45, 13.34) * mm, "end": v(79.38, 13.34) * mm});
            skLineSegment(sketch, "E280.5.0.4", {"start": v(74.45, 9.52) * mm, "end": v(79.38, 9.52) * mm});
            skLineSegment(sketch, "E280.5.0.5", {"start": v(79.37, 4.6) * mm, "end": v(74.45, 9.53) * mm});
            skLineSegment(sketch, "E280.5.0.6", {"start": v(84.3, 9.52) * mm, "end": v(79.38, 9.52) * mm});
            skLineSegment(sketch, "E280.5.0.7", {"start": v(79.38, 4.6) * mm, "end": v(84.3, 9.53) * mm});
            skLineSegment(sketch, "E280.5.0.8", {"start": v(82.07, 1.9) * mm, "end": v(87, 6.83) * mm});
            skLineSegment(sketch, "E280.5.0.9", {"start": v(87, 6.83) * mm, "end": v(91.92, 1.9) * mm});
            skLineSegment(sketch, "E280.5.0.10", {"start": v(82.07, 1.9) * mm, "end": v(91.92, 1.9) * mm});
            skLineSegment(sketch, "E280.5.0.11", {"start": v(82.07, 20.95) * mm, "end": v(87, 16.03) * mm});
            skLineSegment(sketch, "E280.5.0.12", {"start": v(82.07, 20.95) * mm, "end": v(91.92, 20.96) * mm});
            skLineSegment(sketch, "E280.5.0.13", {"start": v(87, 16.03) * mm, "end": v(91.92, 20.96) * mm});
            skLineSegment(sketch, "E280.5.1.0", {"start": v(79.37, 41.12) * mm, "end": v(84.3, 36.2) * mm});
            skLineSegment(sketch, "E280.5.1.1", {"start": v(84.3, 36.2) * mm, "end": v(79.37, 36.2) * mm});
            skLineSegment(sketch, "E280.5.1.2", {"start": v(79.37, 41.12) * mm, "end": v(74.45, 36.2) * mm});
            skLineSegment(sketch, "E280.5.1.3", {"start": v(74.45, 36.2) * mm, "end": v(79.37, 36.2) * mm});
            skLineSegment(sketch, "E280.5.1.4", {"start": v(74.45, 32.38) * mm, "end": v(79.37, 32.38) * mm});
            skLineSegment(sketch, "E280.5.1.5", {"start": v(79.37, 27.46) * mm, "end": v(74.45, 32.39) * mm});
            skLineSegment(sketch, "E280.5.1.6", {"start": v(84.3, 32.38) * mm, "end": v(79.37, 32.38) * mm});
            skLineSegment(sketch, "E280.5.1.7", {"start": v(79.37, 27.46) * mm, "end": v(84.3, 32.39) * mm});
            skLineSegment(sketch, "E280.5.1.8", {"start": v(82.07, 24.77) * mm, "end": v(87, 29.7) * mm});
            skLineSegment(sketch, "E280.5.1.9", {"start": v(87, 29.7) * mm, "end": v(91.92, 24.76) * mm});
            skLineSegment(sketch, "E280.5.1.10", {"start": v(82.07, 24.76) * mm, "end": v(91.92, 24.76) * mm});
            skLineSegment(sketch, "E280.5.1.11", {"start": v(82.07, 43.81) * mm, "end": v(87, 38.89) * mm});
            skLineSegment(sketch, "E280.5.1.12", {"start": v(82.07, 43.81) * mm, "end": v(91.92, 43.81) * mm});
            skLineSegment(sketch, "E280.5.1.13", {"start": v(87, 38.89) * mm, "end": v(91.92, 43.81) * mm});
            skLineSegment(sketch, "E280.5.2.0", {"start": v(79.37, 63.98) * mm, "end": v(84.3, 59.05) * mm});
            skLineSegment(sketch, "E280.5.2.1", {"start": v(84.3, 59.05) * mm, "end": v(79.37, 59.05) * mm});
            skLineSegment(sketch, "E280.5.2.2", {"start": v(79.37, 63.98) * mm, "end": v(74.45, 59.05) * mm});
            skLineSegment(sketch, "E280.5.2.3", {"start": v(74.45, 59.05) * mm, "end": v(79.37, 59.05) * mm});
            skLineSegment(sketch, "E280.5.2.4", {"start": v(74.45, 55.24) * mm, "end": v(79.37, 55.24) * mm});
            skLineSegment(sketch, "E280.5.2.5", {"start": v(79.37, 50.32) * mm, "end": v(74.45, 55.24) * mm});
            skLineSegment(sketch, "E280.5.2.6", {"start": v(84.3, 55.24) * mm, "end": v(79.37, 55.24) * mm});
            skLineSegment(sketch, "E280.5.2.7", {"start": v(79.37, 50.32) * mm, "end": v(84.3, 55.25) * mm});
            skLineSegment(sketch, "E280.5.2.8", {"start": v(82.07, 47.62) * mm, "end": v(87, 52.55) * mm});
            skLineSegment(sketch, "E280.5.2.9", {"start": v(87, 52.55) * mm, "end": v(91.92, 47.62) * mm});
            skLineSegment(sketch, "E280.5.2.10", {"start": v(82.07, 47.62) * mm, "end": v(91.92, 47.62) * mm});
            skLineSegment(sketch, "E280.5.2.11", {"start": v(82.07, 66.67) * mm, "end": v(87, 61.75) * mm});
            skLineSegment(sketch, "E280.5.2.12", {"start": v(82.07, 66.67) * mm, "end": v(91.92, 66.67) * mm});
            skLineSegment(sketch, "E280.5.2.13", {"start": v(87, 61.75) * mm, "end": v(91.92, 66.67) * mm});
            skLineSegment(sketch, "E280.6.0.0", {"start": v(94.61, 18.26) * mm, "end": v(99.54, 13.33) * mm});
            skLineSegment(sketch, "E280.6.0.1", {"start": v(99.54, 13.34) * mm, "end": v(94.61, 13.34) * mm});
            skLineSegment(sketch, "E280.6.0.2", {"start": v(94.62, 18.26) * mm, "end": v(89.69, 13.33) * mm});
            skLineSegment(sketch, "E280.6.0.3", {"start": v(89.69, 13.34) * mm, "end": v(94.61, 13.34) * mm});
            skLineSegment(sketch, "E280.6.0.4", {"start": v(89.69, 9.52) * mm, "end": v(94.61, 9.52) * mm});
            skLineSegment(sketch, "E280.6.0.5", {"start": v(94.61, 4.6) * mm, "end": v(89.69, 9.53) * mm});
            skLineSegment(sketch, "E280.6.0.6", {"start": v(99.54, 9.52) * mm, "end": v(94.61, 9.52) * mm});
            skLineSegment(sketch, "E280.6.0.7", {"start": v(94.62, 4.6) * mm, "end": v(99.54, 9.53) * mm});
            skLineSegment(sketch, "E280.6.0.8", {"start": v(97.3, 1.9) * mm, "end": v(102.23, 6.83) * mm});
            skLineSegment(sketch, "E280.6.0.9", {"start": v(102.23, 6.83) * mm, "end": v(107.16, 1.9) * mm});
            skLineSegment(sketch, "E280.6.0.10", {"start": v(97.3, 1.9) * mm, "end": v(107.16, 1.9) * mm});
            skLineSegment(sketch, "E280.6.0.11", {"start": v(97.3, 20.95) * mm, "end": v(102.23, 16.03) * mm});
            skLineSegment(sketch, "E280.6.0.12", {"start": v(97.3, 20.95) * mm, "end": v(107.16, 20.96) * mm});
            skLineSegment(sketch, "E280.6.0.13", {"start": v(102.23, 16.03) * mm, "end": v(107.16, 20.96) * mm});
            skLineSegment(sketch, "E280.6.1.0", {"start": v(94.61, 41.12) * mm, "end": v(99.54, 36.2) * mm});
            skLineSegment(sketch, "E280.6.1.1", {"start": v(99.54, 36.2) * mm, "end": v(94.61, 36.2) * mm});
            skLineSegment(sketch, "E280.6.1.2", {"start": v(94.61, 41.12) * mm, "end": v(89.69, 36.2) * mm});
            skLineSegment(sketch, "E280.6.1.3", {"start": v(89.69, 36.2) * mm, "end": v(94.61, 36.2) * mm});
            skLineSegment(sketch, "E280.6.1.4", {"start": v(89.69, 32.38) * mm, "end": v(94.61, 32.38) * mm});
            skLineSegment(sketch, "E280.6.1.5", {"start": v(94.61, 27.46) * mm, "end": v(89.69, 32.38) * mm});
            skLineSegment(sketch, "E280.6.1.6", {"start": v(99.54, 32.38) * mm, "end": v(94.61, 32.38) * mm});
            skLineSegment(sketch, "E280.6.1.7", {"start": v(94.61, 27.46) * mm, "end": v(99.54, 32.39) * mm});
            skLineSegment(sketch, "E280.6.1.8", {"start": v(97.3, 24.77) * mm, "end": v(102.23, 29.7) * mm});
            skLineSegment(sketch, "E280.6.1.9", {"start": v(102.23, 29.7) * mm, "end": v(107.16, 24.76) * mm});
            skLineSegment(sketch, "E280.6.1.10", {"start": v(97.3, 24.76) * mm, "end": v(107.16, 24.76) * mm});
            skLineSegment(sketch, "E280.6.1.11", {"start": v(97.3, 43.81) * mm, "end": v(102.23, 38.89) * mm});
            skLineSegment(sketch, "E280.6.1.12", {"start": v(97.3, 43.81) * mm, "end": v(107.16, 43.81) * mm});
            skLineSegment(sketch, "E280.6.1.13", {"start": v(102.23, 38.89) * mm, "end": v(107.16, 43.81) * mm});
            skLineSegment(sketch, "E280.6.2.0", {"start": v(94.61, 63.98) * mm, "end": v(99.54, 59.05) * mm});
            skLineSegment(sketch, "E280.6.2.1", {"start": v(99.54, 59.05) * mm, "end": v(94.61, 59.05) * mm});
            skLineSegment(sketch, "E280.6.2.2", {"start": v(94.61, 63.98) * mm, "end": v(89.69, 59.05) * mm});
            skLineSegment(sketch, "E280.6.2.3", {"start": v(89.69, 59.05) * mm, "end": v(94.61, 59.05) * mm});
            skLineSegment(sketch, "E280.6.2.4", {"start": v(89.69, 55.24) * mm, "end": v(94.61, 55.24) * mm});
            skLineSegment(sketch, "E280.6.2.5", {"start": v(94.61, 50.32) * mm, "end": v(89.69, 55.24) * mm});
            skLineSegment(sketch, "E280.6.2.6", {"start": v(99.54, 55.24) * mm, "end": v(94.61, 55.24) * mm});
            skLineSegment(sketch, "E280.6.2.7", {"start": v(94.61, 50.32) * mm, "end": v(99.54, 55.25) * mm});
            skLineSegment(sketch, "E280.6.2.8", {"start": v(97.3, 47.62) * mm, "end": v(102.23, 52.55) * mm});
            skLineSegment(sketch, "E280.6.2.9", {"start": v(102.23, 52.55) * mm, "end": v(107.16, 47.62) * mm});
            skLineSegment(sketch, "E280.6.2.10", {"start": v(97.3, 47.62) * mm, "end": v(107.16, 47.62) * mm});
            skLineSegment(sketch, "E280.6.2.11", {"start": v(97.3, 66.67) * mm, "end": v(102.23, 61.75) * mm});
            skLineSegment(sketch, "E280.6.2.12", {"start": v(97.3, 66.67) * mm, "end": v(107.16, 66.67) * mm});
            skLineSegment(sketch, "E280.6.2.13", {"start": v(102.23, 61.75) * mm, "end": v(107.16, 66.67) * mm});
            skLineSegment(sketch, "E280.7.0.0", {"start": v(109.85, 18.26) * mm, "end": v(114.78, 13.33) * mm});
            skLineSegment(sketch, "E280.7.0.1", {"start": v(114.78, 13.34) * mm, "end": v(109.85, 13.34) * mm});
            skLineSegment(sketch, "E280.7.0.2", {"start": v(109.86, 18.26) * mm, "end": v(104.93, 13.33) * mm});
            skLineSegment(sketch, "E280.7.0.3", {"start": v(104.93, 13.34) * mm, "end": v(109.85, 13.34) * mm});
            skLineSegment(sketch, "E280.7.0.4", {"start": v(104.93, 9.52) * mm, "end": v(109.85, 9.52) * mm});
            skLineSegment(sketch, "E280.7.0.5", {"start": v(109.85, 4.6) * mm, "end": v(104.93, 9.53) * mm});
            skLineSegment(sketch, "E280.7.0.6", {"start": v(114.78, 9.52) * mm, "end": v(109.85, 9.52) * mm});
            skLineSegment(sketch, "E280.7.0.7", {"start": v(109.86, 4.6) * mm, "end": v(114.78, 9.53) * mm});
            skLineSegment(sketch, "E280.7.0.8", {"start": v(112.55, 1.9) * mm, "end": v(117.48, 6.83) * mm});
            skLineSegment(sketch, "E280.7.0.9", {"start": v(117.47, 6.83) * mm, "end": v(122.4, 1.9) * mm});
            skLineSegment(sketch, "E280.7.0.10", {"start": v(112.55, 1.9) * mm, "end": v(122.4, 1.9) * mm});
            skLineSegment(sketch, "E280.7.0.11", {"start": v(112.55, 20.95) * mm, "end": v(117.47, 16.03) * mm});
            skLineSegment(sketch, "E280.7.0.12", {"start": v(112.55, 20.95) * mm, "end": v(122.4, 20.96) * mm});
            skLineSegment(sketch, "E280.7.0.13", {"start": v(117.47, 16.03) * mm, "end": v(122.4, 20.96) * mm});
            skLineSegment(sketch, "E280.7.1.0", {"start": v(109.85, 41.12) * mm, "end": v(114.78, 36.2) * mm});
            skLineSegment(sketch, "E280.7.1.1", {"start": v(114.78, 36.2) * mm, "end": v(109.85, 36.2) * mm});
            skLineSegment(sketch, "E280.7.1.2", {"start": v(109.85, 41.12) * mm, "end": v(104.93, 36.2) * mm});
            skLineSegment(sketch, "E280.7.1.3", {"start": v(104.93, 36.2) * mm, "end": v(109.85, 36.2) * mm});
            skLineSegment(sketch, "E280.7.1.4", {"start": v(104.93, 32.38) * mm, "end": v(109.85, 32.38) * mm});
            skLineSegment(sketch, "E280.7.1.5", {"start": v(109.85, 27.46) * mm, "end": v(104.93, 32.39) * mm});
            skLineSegment(sketch, "E280.7.1.6", {"start": v(114.78, 32.38) * mm, "end": v(109.85, 32.38) * mm});
            skLineSegment(sketch, "E280.7.1.7", {"start": v(109.85, 27.46) * mm, "end": v(114.78, 32.39) * mm});
            skLineSegment(sketch, "E280.7.1.8", {"start": v(112.55, 24.77) * mm, "end": v(117.47, 29.7) * mm});
            skLineSegment(sketch, "E280.7.1.9", {"start": v(117.47, 29.7) * mm, "end": v(122.4, 24.76) * mm});
            skLineSegment(sketch, "E280.7.1.10", {"start": v(112.55, 24.76) * mm, "end": v(122.4, 24.76) * mm});
            skLineSegment(sketch, "E280.7.1.11", {"start": v(112.55, 43.81) * mm, "end": v(117.47, 38.89) * mm});
            skLineSegment(sketch, "E280.7.1.12", {"start": v(112.55, 43.81) * mm, "end": v(122.4, 43.81) * mm});
            skLineSegment(sketch, "E280.7.1.13", {"start": v(117.47, 38.89) * mm, "end": v(122.4, 43.81) * mm});
            skLineSegment(sketch, "E280.7.2.0", {"start": v(109.85, 63.98) * mm, "end": v(114.78, 59.05) * mm});
            skLineSegment(sketch, "E280.7.2.1", {"start": v(114.78, 59.05) * mm, "end": v(109.85, 59.05) * mm});
            skLineSegment(sketch, "E280.7.2.2", {"start": v(109.85, 63.98) * mm, "end": v(104.93, 59.05) * mm});
            skLineSegment(sketch, "E280.7.2.3", {"start": v(104.93, 59.05) * mm, "end": v(109.85, 59.05) * mm});
            skLineSegment(sketch, "E280.7.2.4", {"start": v(104.93, 55.24) * mm, "end": v(109.85, 55.24) * mm});
            skLineSegment(sketch, "E280.7.2.5", {"start": v(109.85, 50.32) * mm, "end": v(104.93, 55.24) * mm});
            skLineSegment(sketch, "E280.7.2.6", {"start": v(114.78, 55.24) * mm, "end": v(109.85, 55.24) * mm});
            skLineSegment(sketch, "E280.7.2.7", {"start": v(109.85, 50.32) * mm, "end": v(114.78, 55.24) * mm});
            skLineSegment(sketch, "E280.7.2.8", {"start": v(112.55, 47.62) * mm, "end": v(117.47, 52.55) * mm});
            skLineSegment(sketch, "E280.7.2.9", {"start": v(117.47, 52.55) * mm, "end": v(122.4, 47.62) * mm});
            skLineSegment(sketch, "E280.7.2.10", {"start": v(112.55, 47.62) * mm, "end": v(122.4, 47.62) * mm});
            skLineSegment(sketch, "E280.7.2.11", {"start": v(112.55, 66.67) * mm, "end": v(117.47, 61.75) * mm});
            skLineSegment(sketch, "E280.7.2.12", {"start": v(112.55, 66.67) * mm, "end": v(122.4, 66.67) * mm});
            skLineSegment(sketch, "E280.7.2.13", {"start": v(117.47, 61.75) * mm, "end": v(122.4, 66.67) * mm});
            skLineSegment(sketch, "E280.8.0.0", {"start": v(125.1, 18.26) * mm, "end": v(130.02, 13.33) * mm});
            skLineSegment(sketch, "E280.8.0.1", {"start": v(130.02, 13.34) * mm, "end": v(125.1, 13.34) * mm});
            skLineSegment(sketch, "E280.8.0.2", {"start": v(125.1, 18.26) * mm, "end": v(120.17, 13.33) * mm});
            skLineSegment(sketch, "E280.8.0.3", {"start": v(120.17, 13.34) * mm, "end": v(125.1, 13.34) * mm});
            skLineSegment(sketch, "E280.8.0.4", {"start": v(120.17, 9.52) * mm, "end": v(125.1, 9.52) * mm});
            skLineSegment(sketch, "E280.8.0.5", {"start": v(125.1, 4.6) * mm, "end": v(120.17, 9.53) * mm});
            skLineSegment(sketch, "E280.8.0.6", {"start": v(130.02, 9.52) * mm, "end": v(125.1, 9.52) * mm});
            skLineSegment(sketch, "E280.8.0.7", {"start": v(125.1, 4.6) * mm, "end": v(130.02, 9.53) * mm});
            skLineSegment(sketch, "E280.8.0.8", {"start": v(127.79, 1.9) * mm, "end": v(132.72, 6.83) * mm});
            skLineSegment(sketch, "E280.8.0.9", {"start": v(132.72, 6.83) * mm, "end": v(137.64, 1.9) * mm});
            skLineSegment(sketch, "E280.8.0.10", {"start": v(127.79, 1.9) * mm, "end": v(137.64, 1.9) * mm});
            skLineSegment(sketch, "E280.8.0.11", {"start": v(127.79, 20.95) * mm, "end": v(132.71, 16.03) * mm});
            skLineSegment(sketch, "E280.8.0.12", {"start": v(127.79, 20.95) * mm, "end": v(137.64, 20.96) * mm});
            skLineSegment(sketch, "E280.8.0.13", {"start": v(132.71, 16.03) * mm, "end": v(137.64, 20.96) * mm});
            skLineSegment(sketch, "E280.8.1.0", {"start": v(125.1, 41.12) * mm, "end": v(130.02, 36.2) * mm});
            skLineSegment(sketch, "E280.8.1.1", {"start": v(130.02, 36.2) * mm, "end": v(125.1, 36.2) * mm});
            skLineSegment(sketch, "E280.8.1.2", {"start": v(125.1, 41.12) * mm, "end": v(120.17, 36.2) * mm});
            skLineSegment(sketch, "E280.8.1.3", {"start": v(120.17, 36.2) * mm, "end": v(125.1, 36.2) * mm});
            skLineSegment(sketch, "E280.8.1.4", {"start": v(120.17, 32.38) * mm, "end": v(125.1, 32.38) * mm});
            skLineSegment(sketch, "E280.8.1.5", {"start": v(125.1, 27.46) * mm, "end": v(120.17, 32.39) * mm});
            skLineSegment(sketch, "E280.8.1.6", {"start": v(130.02, 32.38) * mm, "end": v(125.1, 32.38) * mm});
            skLineSegment(sketch, "E280.8.1.7", {"start": v(125.1, 27.46) * mm, "end": v(130.02, 32.39) * mm});
            skLineSegment(sketch, "E280.8.1.8", {"start": v(127.79, 24.77) * mm, "end": v(132.71, 29.7) * mm});
            skLineSegment(sketch, "E280.8.1.9", {"start": v(132.71, 29.7) * mm, "end": v(137.64, 24.76) * mm});
            skLineSegment(sketch, "E280.8.1.10", {"start": v(127.79, 24.76) * mm, "end": v(137.64, 24.76) * mm});
            skLineSegment(sketch, "E280.8.1.11", {"start": v(127.79, 43.81) * mm, "end": v(132.71, 38.89) * mm});
            skLineSegment(sketch, "E280.8.1.12", {"start": v(127.79, 43.81) * mm, "end": v(137.64, 43.81) * mm});
            skLineSegment(sketch, "E280.8.1.13", {"start": v(132.71, 38.89) * mm, "end": v(137.64, 43.82) * mm});
            skLineSegment(sketch, "E280.8.2.0", {"start": v(125.1, 63.98) * mm, "end": v(130.02, 59.05) * mm});
            skLineSegment(sketch, "E280.8.2.1", {"start": v(130.02, 59.05) * mm, "end": v(125.1, 59.05) * mm});
            skLineSegment(sketch, "E280.8.2.2", {"start": v(125.1, 63.98) * mm, "end": v(120.17, 59.05) * mm});
            skLineSegment(sketch, "E280.8.2.3", {"start": v(120.17, 59.05) * mm, "end": v(125.1, 59.05) * mm});
            skLineSegment(sketch, "E280.8.2.4", {"start": v(120.17, 55.24) * mm, "end": v(125.1, 55.24) * mm});
            skLineSegment(sketch, "E280.8.2.5", {"start": v(125.1, 50.32) * mm, "end": v(120.17, 55.25) * mm});
            skLineSegment(sketch, "E280.8.2.6", {"start": v(130.02, 55.24) * mm, "end": v(125.1, 55.24) * mm});
            skLineSegment(sketch, "E280.8.2.7", {"start": v(125.1, 50.32) * mm, "end": v(130.02, 55.24) * mm});
            skLineSegment(sketch, "E280.8.2.8", {"start": v(127.79, 47.62) * mm, "end": v(132.71, 52.55) * mm});
            skLineSegment(sketch, "E280.8.2.9", {"start": v(132.71, 52.55) * mm, "end": v(137.64, 47.62) * mm});
            skLineSegment(sketch, "E280.8.2.10", {"start": v(127.79, 47.62) * mm, "end": v(137.64, 47.62) * mm});
            skLineSegment(sketch, "E280.8.2.11", {"start": v(127.79, 66.67) * mm, "end": v(132.71, 61.75) * mm});
            skLineSegment(sketch, "E280.8.2.12", {"start": v(127.79, 66.67) * mm, "end": v(137.64, 66.67) * mm});
            skLineSegment(sketch, "E280.8.2.13", {"start": v(132.71, 61.75) * mm, "end": v(137.64, 66.67) * mm});
            skLineSegment(sketch, "E280.9.0.0", {"start": v(140.33, 18.26) * mm, "end": v(145.26, 13.33) * mm});
            skLineSegment(sketch, "E280.9.0.1", {"start": v(145.26, 13.34) * mm, "end": v(140.34, 13.34) * mm});
            skLineSegment(sketch, "E280.9.0.2", {"start": v(140.34, 18.26) * mm, "end": v(135.4, 13.33) * mm});
            skLineSegment(sketch, "E280.9.0.3", {"start": v(135.4, 13.34) * mm, "end": v(140.34, 13.34) * mm});
            skLineSegment(sketch, "E280.9.0.4", {"start": v(135.4, 9.52) * mm, "end": v(140.34, 9.52) * mm});
            skLineSegment(sketch, "E280.9.0.5", {"start": v(140.33, 4.6) * mm, "end": v(135.4, 9.53) * mm});
            skLineSegment(sketch, "E280.9.0.6", {"start": v(145.26, 9.52) * mm, "end": v(140.34, 9.52) * mm});
            skLineSegment(sketch, "E280.9.0.7", {"start": v(140.34, 4.6) * mm, "end": v(145.26, 9.53) * mm});
            skLineSegment(sketch, "E280.9.0.8", {"start": v(143.03, 1.9) * mm, "end": v(147.96, 6.83) * mm});
            skLineSegment(sketch, "E280.9.0.9", {"start": v(147.96, 6.83) * mm, "end": v(152.88, 1.9) * mm});
            skLineSegment(sketch, "E280.9.0.10", {"start": v(143.03, 1.9) * mm, "end": v(152.88, 1.9) * mm});
            skLineSegment(sketch, "E280.9.0.11", {"start": v(143.03, 20.95) * mm, "end": v(147.95, 16.03) * mm});
            skLineSegment(sketch, "E280.9.0.12", {"start": v(143.03, 20.95) * mm, "end": v(152.88, 20.96) * mm});
            skLineSegment(sketch, "E280.9.0.13", {"start": v(147.95, 16.03) * mm, "end": v(152.88, 20.96) * mm});
            skLineSegment(sketch, "E280.9.1.0", {"start": v(140.33, 41.12) * mm, "end": v(145.26, 36.2) * mm});
            skLineSegment(sketch, "E280.9.1.1", {"start": v(145.26, 36.2) * mm, "end": v(140.33, 36.2) * mm});
            skLineSegment(sketch, "E280.9.1.2", {"start": v(140.33, 41.12) * mm, "end": v(135.4, 36.2) * mm});
            skLineSegment(sketch, "E280.9.1.3", {"start": v(135.4, 36.2) * mm, "end": v(140.33, 36.2) * mm});
            skLineSegment(sketch, "E280.9.1.4", {"start": v(135.4, 32.38) * mm, "end": v(140.33, 32.38) * mm});
            skLineSegment(sketch, "E280.9.1.5", {"start": v(140.33, 27.46) * mm, "end": v(135.4, 32.39) * mm});
            skLineSegment(sketch, "E280.9.1.6", {"start": v(145.26, 32.38) * mm, "end": v(140.33, 32.38) * mm});
            skLineSegment(sketch, "E280.9.1.7", {"start": v(140.33, 27.46) * mm, "end": v(145.26, 32.38) * mm});
            skLineSegment(sketch, "E280.9.1.8", {"start": v(143.03, 24.77) * mm, "end": v(147.95, 29.7) * mm});
            skLineSegment(sketch, "E280.9.1.9", {"start": v(147.95, 29.7) * mm, "end": v(152.88, 24.76) * mm});
            skLineSegment(sketch, "E280.9.1.10", {"start": v(143.03, 24.76) * mm, "end": v(152.88, 24.76) * mm});
            skLineSegment(sketch, "E280.9.1.11", {"start": v(143.03, 43.81) * mm, "end": v(147.95, 38.89) * mm});
            skLineSegment(sketch, "E280.9.1.12", {"start": v(143.03, 43.81) * mm, "end": v(152.88, 43.81) * mm});
            skLineSegment(sketch, "E280.9.1.13", {"start": v(147.95, 38.89) * mm, "end": v(152.88, 43.81) * mm});
            skLineSegment(sketch, "E280.9.2.0", {"start": v(140.33, 63.98) * mm, "end": v(145.26, 59.05) * mm});
            skLineSegment(sketch, "E280.9.2.1", {"start": v(145.26, 59.05) * mm, "end": v(140.33, 59.05) * mm});
            skLineSegment(sketch, "E280.9.2.2", {"start": v(140.33, 63.98) * mm, "end": v(135.4, 59.05) * mm});
            skLineSegment(sketch, "E280.9.2.3", {"start": v(135.4, 59.05) * mm, "end": v(140.33, 59.05) * mm});
            skLineSegment(sketch, "E280.9.2.4", {"start": v(135.4, 55.24) * mm, "end": v(140.33, 55.24) * mm});
            skLineSegment(sketch, "E280.9.2.5", {"start": v(140.33, 50.32) * mm, "end": v(135.4, 55.25) * mm});
            skLineSegment(sketch, "E280.9.2.6", {"start": v(145.26, 55.24) * mm, "end": v(140.33, 55.24) * mm});
            skLineSegment(sketch, "E280.9.2.7", {"start": v(140.33, 50.32) * mm, "end": v(145.26, 55.24) * mm});
            skLineSegment(sketch, "E280.9.2.8", {"start": v(143.03, 47.62) * mm, "end": v(147.95, 52.55) * mm});
            skLineSegment(sketch, "E280.9.2.9", {"start": v(147.95, 52.55) * mm, "end": v(152.88, 47.62) * mm});
            skLineSegment(sketch, "E280.9.2.10", {"start": v(143.03, 47.62) * mm, "end": v(152.88, 47.62) * mm});
            skLineSegment(sketch, "E280.9.2.11", {"start": v(143.03, 66.67) * mm, "end": v(147.95, 61.75) * mm});
            skLineSegment(sketch, "E280.9.2.12", {"start": v(143.03, 66.67) * mm, "end": v(152.88, 66.67) * mm});
            skLineSegment(sketch, "E280.9.2.13", {"start": v(147.95, 61.75) * mm, "end": v(152.88, 66.67) * mm});
            skLineSegment(sketch, "E280.10.0.0", {"start": v(155.57, 18.26) * mm, "end": v(160.5, 13.33) * mm});
            skLineSegment(sketch, "E280.10.0.1", {"start": v(160.5, 13.34) * mm, "end": v(155.58, 13.34) * mm});
            skLineSegment(sketch, "E280.10.0.2", {"start": v(155.58, 18.26) * mm, "end": v(150.65, 13.33) * mm});
            skLineSegment(sketch, "E280.10.0.3", {"start": v(150.65, 13.34) * mm, "end": v(155.58, 13.34) * mm});
            skLineSegment(sketch, "E280.10.0.11", {"start": v(158.27, 20.95) * mm, "end": v(163.2, 16.03) * mm});
            skLineSegment(sketch, "E280.10.1.0", {"start": v(155.57, 41.12) * mm, "end": v(160.5, 36.2) * mm});
            skLineSegment(sketch, "E280.10.1.1", {"start": v(160.5, 36.2) * mm, "end": v(155.57, 36.2) * mm});
            skLineSegment(sketch, "E280.10.1.2", {"start": v(155.57, 41.12) * mm, "end": v(150.65, 36.2) * mm});
            skLineSegment(sketch, "E280.10.1.3", {"start": v(150.65, 36.2) * mm, "end": v(155.57, 36.2) * mm});
            skLineSegment(sketch, "E280.10.1.4", {"start": v(150.65, 32.38) * mm, "end": v(155.57, 32.38) * mm});
            skLineSegment(sketch, "E280.10.1.5", {"start": v(155.57, 27.46) * mm, "end": v(150.65, 32.39) * mm});
            skLineSegment(sketch, "E280.10.1.6", {"start": v(160.5, 32.38) * mm, "end": v(155.57, 32.38) * mm});
            skLineSegment(sketch, "E280.10.1.7", {"start": v(155.57, 27.46) * mm, "end": v(160.5, 32.39) * mm});
            skLineSegment(sketch, "E280.10.1.8", {"start": v(158.27, 24.77) * mm, "end": v(163.2, 29.7) * mm});
            skLineSegment(sketch, "E280.10.1.11", {"start": v(158.27, 43.81) * mm, "end": v(163.2, 38.89) * mm});
            skLineSegment(sketch, "E280.10.1.12", {"start": v(158.27, 43.81) * mm, "end": v(163.2, 43.81) * mm});
            skLineSegment(sketch, "E280.10.2.0", {"start": v(155.57, 63.98) * mm, "end": v(160.5, 59.05) * mm});
            skLineSegment(sketch, "E280.10.2.1", {"start": v(160.5, 59.05) * mm, "end": v(155.57, 59.05) * mm});
            skLineSegment(sketch, "E280.10.2.2", {"start": v(155.57, 63.98) * mm, "end": v(150.65, 59.05) * mm});
            skLineSegment(sketch, "E280.10.2.3", {"start": v(150.65, 59.05) * mm, "end": v(155.57, 59.05) * mm});
            skLineSegment(sketch, "E280.10.2.4", {"start": v(150.65, 55.24) * mm, "end": v(155.57, 55.24) * mm});
            skLineSegment(sketch, "E280.10.2.5", {"start": v(155.57, 50.32) * mm, "end": v(150.65, 55.25) * mm});
            skLineSegment(sketch, "E280.10.2.6", {"start": v(160.5, 55.24) * mm, "end": v(155.57, 55.24) * mm});
            skLineSegment(sketch, "E280.10.2.7", {"start": v(155.57, 50.32) * mm, "end": v(160.5, 55.24) * mm});
            skLineSegment(sketch, "E280.10.2.8", {"start": v(158.27, 47.63) * mm, "end": v(163.2, 52.55) * mm});
            skLineSegment(sketch, "E280.10.2.11", {"start": v(158.27, 66.67) * mm, "end": v(163.2, 61.75) * mm});
            skLineSegment(sketch, "E280.10.2.12", {"start": v(158.27, 66.67) * mm, "end": v(163.2, 66.67) * mm});
            skLineSegment(sketch, "E280.direction2", {"start": v(5.87, 1.9) * mm, "end": v(5.87, 24.77) * mm, "construction": true});
            skLineSegment(sketch, "E281", {"start": v(163.2, 52.55) * mm, "end": v(163.2, 47.62) * mm});
            skLineSegment(sketch, "E282", {"start": v(163.2, 43.81) * mm, "end": v(163.2, 38.89) * mm});
            skLineSegment(sketch, "E283", {"start": v(163.2, 61.75) * mm, "end": v(163.2, 66.67) * mm});
            skLineSegment(sketch, "E284", {"start": v(158.27, 47.62) * mm, "end": v(163.2, 47.62) * mm});
            skLineSegment(sketch, "E285", {"start": v(158.27, 24.77) * mm, "end": v(163.2, 24.77) * mm});
            skLineSegment(sketch, "E286", {"start": v(163.2, 24.77) * mm, "end": v(163.2, 29.7) * mm});
            skLineSegment(sketch, "E287", {"start": v(158.27, 20.95) * mm, "end": v(163.2, 20.95) * mm});
            skLineSegment(sketch, "E288", {"start": v(163.2, 20.95) * mm, "end": v(163.2, 16.03) * mm});
            skLineSegment(sketch, "E289.0.1.0", {"start": v(-4.44, 38.89) * mm, "end": v(-4.44, 43.81) * mm});
            skLineSegment(sketch, "E289.0.1.1", {"start": v(-4.44, 43.81) * mm, "end": v(0.48, 43.81) * mm});
            skLineSegment(sketch, "E289.0.1.2", {"start": v(0.48, 43.81) * mm, "end": v(-4.44, 38.89) * mm});
            skLineSegment(sketch, "E289.0.1.3", {"start": v(-4.44, 29.7) * mm, "end": v(-4.44, 24.77) * mm});
            skLineSegment(sketch, "E289.0.1.4", {"start": v(-4.45, 29.7) * mm, "end": v(0.48, 24.77) * mm});
            skLineSegment(sketch, "E289.0.1.5", {"start": v(0.48, 24.77) * mm, "end": v(-4.44, 24.77) * mm});
            skLineSegment(sketch, "E289.0.2.0", {"start": v(-4.44, 61.75) * mm, "end": v(-4.44, 66.67) * mm});
            skLineSegment(sketch, "E289.0.2.1", {"start": v(-4.44, 66.67) * mm, "end": v(0.48, 66.67) * mm});
            skLineSegment(sketch, "E289.0.2.2", {"start": v(0.48, 66.67) * mm, "end": v(-4.44, 61.75) * mm});
            skLineSegment(sketch, "E289.0.2.3", {"start": v(-4.44, 52.55) * mm, "end": v(-4.44, 47.63) * mm});
            skLineSegment(sketch, "E289.0.2.4", {"start": v(-4.45, 52.55) * mm, "end": v(0.48, 47.62) * mm});
            skLineSegment(sketch, "E289.0.2.5", {"start": v(0.48, 47.62) * mm, "end": v(-4.44, 47.62) * mm});
            skSolve(sketch);
        }
        {
            var Q0;
            Q0=qSketchRegion(id+"F28",true);
            extrude(context, id + "F29", {"entities" : qUnion([Q0]), "operationType" : NewBodyOperationType.REMOVE, "oppositeDirection" : true, "depth" : 2.54 * mm, "offsetDistance" : 25.4 * mm});
        }
        {
            var Q0;
            Q0=makeQuery(id+"F6.boolean.opBoolean","MERGE",FACE,{"derivedFrom":[makeQuery(id+"F2.opExtrude","SWEPT_FACE",FACE,{"disambiguationData":[OSD([sQuery(id+"F1.wireOp",EDGE,"E9.3")])]}),makeQuery(id+"F6.opExtrude","SWEPT_FACE",FACE,{"disambiguationData":[OSD([sQuery(id+"F5.wireOp",EDGE,"E60.right")])]})]});
            var sketch = newSketch(context, id + "F30", { "sketchPlane" : qUnion([Q0])});
            skLineSegment(sketch, "E290.0.2.0", {"start": v(-152.04, 63.9) * mm, "end": v(-147.1, 58.98) * mm});
            skLineSegment(sketch, "E290.0.2.2", {"start": v(-152.04, 63.9) * mm, "end": v(-156.96, 58.98) * mm});
            skLineSegment(sketch, "E290.0.2.3", {"start": v(-156.96, 58.98) * mm, "end": v(-147.1, 58.98) * mm});
            skLineSegment(sketch, "E290.0.2.4", {"start": v(-156.96, 55.17) * mm, "end": v(-147.1, 55.17) * mm});
            skLineSegment(sketch, "E290.0.2.5", {"start": v(-152.04, 50.24) * mm, "end": v(-156.96, 55.17) * mm});
            skLineSegment(sketch, "E290.0.2.7", {"start": v(-152.04, 50.24) * mm, "end": v(-147.1, 55.17) * mm});
            skLineSegment(sketch, "E290.0.2.8", {"start": v(-149.34, 47.55) * mm, "end": v(-144.42, 52.48) * mm});
            skLineSegment(sketch, "E290.0.2.9", {"start": v(-144.42, 52.48) * mm, "end": v(-139.49, 47.55) * mm});
            skLineSegment(sketch, "E290.0.2.10", {"start": v(-149.34, 47.55) * mm, "end": v(-139.49, 47.55) * mm});
            skLineSegment(sketch, "E290.0.2.11", {"start": v(-149.34, 66.6) * mm, "end": v(-144.42, 61.67) * mm});
            skLineSegment(sketch, "E290.0.2.12", {"start": v(-149.34, 66.6) * mm, "end": v(-139.49, 66.6) * mm});
            skLineSegment(sketch, "E290.0.2.13", {"start": v(-144.42, 61.67) * mm, "end": v(-139.49, 66.6) * mm});
            skLineSegment(sketch, "E290.1.2.0", {"start": v(-136.8, 63.9) * mm, "end": v(-131.87, 58.98) * mm});
            skLineSegment(sketch, "E290.1.2.2", {"start": v(-136.8, 63.9) * mm, "end": v(-141.72, 58.98) * mm});
            skLineSegment(sketch, "E290.1.2.3", {"start": v(-141.72, 58.98) * mm, "end": v(-131.87, 58.98) * mm});
            skLineSegment(sketch, "E290.1.2.4", {"start": v(-141.72, 55.17) * mm, "end": v(-131.87, 55.17) * mm});
            skLineSegment(sketch, "E290.1.2.5", {"start": v(-136.8, 50.24) * mm, "end": v(-141.72, 55.17) * mm});
            skLineSegment(sketch, "E290.1.2.7", {"start": v(-136.8, 50.24) * mm, "end": v(-131.87, 55.17) * mm});
            skLineSegment(sketch, "E290.1.2.8", {"start": v(-134.1, 47.55) * mm, "end": v(-129.18, 52.48) * mm});
            skLineSegment(sketch, "E290.1.2.9", {"start": v(-129.18, 52.48) * mm, "end": v(-124.25, 47.55) * mm});
            skLineSegment(sketch, "E290.1.2.10", {"start": v(-134.1, 47.55) * mm, "end": v(-124.25, 47.55) * mm});
            skLineSegment(sketch, "E290.1.2.11", {"start": v(-134.1, 66.6) * mm, "end": v(-129.18, 61.67) * mm});
            skLineSegment(sketch, "E290.1.2.12", {"start": v(-134.1, 66.6) * mm, "end": v(-124.25, 66.6) * mm});
            skLineSegment(sketch, "E290.1.2.13", {"start": v(-129.18, 61.67) * mm, "end": v(-124.25, 66.6) * mm});
            skLineSegment(sketch, "E290.2.2.0", {"start": v(-121.56, 63.9) * mm, "end": v(-116.63, 58.98) * mm});
            skLineSegment(sketch, "E290.2.2.2", {"start": v(-121.56, 63.9) * mm, "end": v(-126.48, 58.98) * mm});
            skLineSegment(sketch, "E290.2.2.3", {"start": v(-126.48, 58.98) * mm, "end": v(-116.63, 58.98) * mm});
            skLineSegment(sketch, "E290.2.2.4", {"start": v(-126.48, 55.17) * mm, "end": v(-116.63, 55.17) * mm});
            skLineSegment(sketch, "E290.2.2.5", {"start": v(-121.56, 50.24) * mm, "end": v(-126.48, 55.17) * mm});
            skLineSegment(sketch, "E290.2.2.7", {"start": v(-121.56, 50.24) * mm, "end": v(-116.63, 55.17) * mm});
            skLineSegment(sketch, "E290.2.2.8", {"start": v(-118.86, 47.55) * mm, "end": v(-113.94, 52.48) * mm});
            skLineSegment(sketch, "E290.2.2.9", {"start": v(-113.94, 52.48) * mm, "end": v(-109, 47.55) * mm});
            skLineSegment(sketch, "E290.2.2.10", {"start": v(-118.86, 47.55) * mm, "end": v(-109, 47.55) * mm});
            skLineSegment(sketch, "E290.2.2.11", {"start": v(-118.86, 66.6) * mm, "end": v(-113.94, 61.67) * mm});
            skLineSegment(sketch, "E290.2.2.12", {"start": v(-118.86, 66.6) * mm, "end": v(-109, 66.6) * mm});
            skLineSegment(sketch, "E290.2.2.13", {"start": v(-113.94, 61.67) * mm, "end": v(-109, 66.6) * mm});
            skLineSegment(sketch, "E290.3.2.0", {"start": v(-106.32, 63.9) * mm, "end": v(-101.39, 58.98) * mm});
            skLineSegment(sketch, "E290.3.2.2", {"start": v(-106.32, 63.9) * mm, "end": v(-111.24, 58.98) * mm});
            skLineSegment(sketch, "E290.3.2.3", {"start": v(-111.24, 58.98) * mm, "end": v(-101.39, 58.98) * mm});
            skLineSegment(sketch, "E290.3.2.4", {"start": v(-111.24, 55.17) * mm, "end": v(-101.39, 55.17) * mm});
            skLineSegment(sketch, "E290.3.2.5", {"start": v(-106.32, 50.24) * mm, "end": v(-111.24, 55.17) * mm});
            skLineSegment(sketch, "E290.3.2.7", {"start": v(-106.32, 50.24) * mm, "end": v(-101.39, 55.17) * mm});
            skLineSegment(sketch, "E290.3.2.8", {"start": v(-103.62, 47.55) * mm, "end": v(-98.7, 52.48) * mm});
            skLineSegment(sketch, "E290.3.2.9", {"start": v(-98.7, 52.48) * mm, "end": v(-93.77, 47.55) * mm});
            skLineSegment(sketch, "E290.3.2.10", {"start": v(-103.62, 47.55) * mm, "end": v(-93.77, 47.55) * mm});
            skLineSegment(sketch, "E290.3.2.11", {"start": v(-103.62, 66.6) * mm, "end": v(-98.7, 61.67) * mm});
            skLineSegment(sketch, "E290.3.2.12", {"start": v(-103.62, 66.6) * mm, "end": v(-93.77, 66.6) * mm});
            skLineSegment(sketch, "E290.3.2.13", {"start": v(-98.7, 61.67) * mm, "end": v(-93.77, 66.6) * mm});
            skLineSegment(sketch, "E290.4.2.0", {"start": v(-91.08, 63.9) * mm, "end": v(-86.15, 58.98) * mm});
            skLineSegment(sketch, "E290.4.2.2", {"start": v(-91.08, 63.9) * mm, "end": v(-96, 58.98) * mm});
            skLineSegment(sketch, "E290.4.2.3", {"start": v(-96, 58.98) * mm, "end": v(-86.15, 58.98) * mm});
            skLineSegment(sketch, "E290.4.2.4", {"start": v(-96, 55.17) * mm, "end": v(-86.15, 55.17) * mm});
            skLineSegment(sketch, "E290.4.2.5", {"start": v(-91.08, 50.24) * mm, "end": v(-96, 55.17) * mm});
            skLineSegment(sketch, "E290.4.2.7", {"start": v(-91.08, 50.24) * mm, "end": v(-86.15, 55.17) * mm});
            skLineSegment(sketch, "E290.4.2.8", {"start": v(-88.38, 47.55) * mm, "end": v(-83.46, 52.48) * mm});
            skLineSegment(sketch, "E290.4.2.9", {"start": v(-83.46, 52.48) * mm, "end": v(-78.53, 47.55) * mm});
            skLineSegment(sketch, "E290.4.2.10", {"start": v(-88.38, 47.55) * mm, "end": v(-78.53, 47.55) * mm});
            skLineSegment(sketch, "E290.4.2.11", {"start": v(-88.38, 66.6) * mm, "end": v(-83.46, 61.67) * mm});
            skLineSegment(sketch, "E290.4.2.12", {"start": v(-88.38, 66.6) * mm, "end": v(-78.53, 66.6) * mm});
            skLineSegment(sketch, "E290.4.2.13", {"start": v(-83.46, 61.67) * mm, "end": v(-78.53, 66.6) * mm});
            skLineSegment(sketch, "E290.5.2.0", {"start": v(-75.84, 63.9) * mm, "end": v(-70.9, 58.98) * mm});
            skLineSegment(sketch, "E290.5.2.2", {"start": v(-75.84, 63.9) * mm, "end": v(-80.76, 58.98) * mm});
            skLineSegment(sketch, "E290.5.2.3", {"start": v(-80.76, 58.98) * mm, "end": v(-70.9, 58.98) * mm});
            skLineSegment(sketch, "E290.5.2.4", {"start": v(-80.76, 55.17) * mm, "end": v(-70.9, 55.17) * mm});
            skLineSegment(sketch, "E290.5.2.5", {"start": v(-75.84, 50.24) * mm, "end": v(-80.76, 55.17) * mm});
            skLineSegment(sketch, "E290.5.2.7", {"start": v(-75.84, 50.24) * mm, "end": v(-70.9, 55.17) * mm});
            skLineSegment(sketch, "E290.5.2.8", {"start": v(-73.14, 47.55) * mm, "end": v(-68.22, 52.48) * mm});
            skLineSegment(sketch, "E290.5.2.9", {"start": v(-68.22, 52.48) * mm, "end": v(-63.29, 47.55) * mm});
            skLineSegment(sketch, "E290.5.2.10", {"start": v(-73.14, 47.55) * mm, "end": v(-63.29, 47.55) * mm});
            skLineSegment(sketch, "E290.5.2.11", {"start": v(-73.14, 66.6) * mm, "end": v(-68.22, 61.67) * mm});
            skLineSegment(sketch, "E290.5.2.12", {"start": v(-73.14, 66.6) * mm, "end": v(-63.29, 66.6) * mm});
            skLineSegment(sketch, "E290.5.2.13", {"start": v(-68.22, 61.67) * mm, "end": v(-63.29, 66.6) * mm});
            skLineSegment(sketch, "E290.6.2.0", {"start": v(-60.6, 63.9) * mm, "end": v(-55.67, 58.98) * mm});
            skLineSegment(sketch, "E290.6.2.2", {"start": v(-60.6, 63.9) * mm, "end": v(-65.52, 58.98) * mm});
            skLineSegment(sketch, "E290.6.2.3", {"start": v(-65.52, 58.98) * mm, "end": v(-55.67, 58.98) * mm});
            skLineSegment(sketch, "E290.6.2.4", {"start": v(-65.52, 55.17) * mm, "end": v(-55.67, 55.17) * mm});
            skLineSegment(sketch, "E290.6.2.5", {"start": v(-60.6, 50.24) * mm, "end": v(-65.52, 55.17) * mm});
            skLineSegment(sketch, "E290.6.2.7", {"start": v(-60.6, 50.24) * mm, "end": v(-55.67, 55.17) * mm});
            skLineSegment(sketch, "E290.6.2.8", {"start": v(-57.9, 47.55) * mm, "end": v(-52.98, 52.48) * mm});
            skLineSegment(sketch, "E290.6.2.9", {"start": v(-52.98, 52.48) * mm, "end": v(-48.05, 47.55) * mm});
            skLineSegment(sketch, "E290.6.2.10", {"start": v(-57.9, 47.55) * mm, "end": v(-48.05, 47.55) * mm});
            skLineSegment(sketch, "E290.6.2.11", {"start": v(-57.9, 66.6) * mm, "end": v(-52.98, 61.67) * mm});
            skLineSegment(sketch, "E290.6.2.12", {"start": v(-57.9, 66.6) * mm, "end": v(-48.05, 66.6) * mm});
            skLineSegment(sketch, "E290.6.2.13", {"start": v(-52.98, 61.67) * mm, "end": v(-48.05, 66.6) * mm});
            skLineSegment(sketch, "E290.7.2.0", {"start": v(-45.36, 63.9) * mm, "end": v(-40.43, 58.98) * mm});
            skLineSegment(sketch, "E290.7.2.2", {"start": v(-45.36, 63.9) * mm, "end": v(-50.28, 58.98) * mm});
            skLineSegment(sketch, "E290.7.2.3", {"start": v(-50.28, 58.98) * mm, "end": v(-40.43, 58.98) * mm});
            skLineSegment(sketch, "E290.7.2.4", {"start": v(-50.28, 55.17) * mm, "end": v(-40.43, 55.17) * mm});
            skLineSegment(sketch, "E290.7.2.5", {"start": v(-45.36, 50.24) * mm, "end": v(-50.28, 55.17) * mm});
            skLineSegment(sketch, "E290.7.2.7", {"start": v(-45.36, 50.24) * mm, "end": v(-40.43, 55.17) * mm});
            skLineSegment(sketch, "E290.7.2.8", {"start": v(-42.66, 47.55) * mm, "end": v(-37.74, 52.48) * mm});
            skLineSegment(sketch, "E290.7.2.9", {"start": v(-37.74, 52.48) * mm, "end": v(-32.8, 47.55) * mm});
            skLineSegment(sketch, "E290.7.2.10", {"start": v(-42.66, 47.55) * mm, "end": v(-32.8, 47.55) * mm});
            skLineSegment(sketch, "E290.7.2.11", {"start": v(-42.66, 66.6) * mm, "end": v(-37.74, 61.67) * mm});
            skLineSegment(sketch, "E290.7.2.12", {"start": v(-42.66, 66.6) * mm, "end": v(-32.8, 66.6) * mm});
            skLineSegment(sketch, "E290.7.2.13", {"start": v(-37.74, 61.67) * mm, "end": v(-32.8, 66.6) * mm});
            skLineSegment(sketch, "E290.8.2.0", {"start": v(-30.12, 63.9) * mm, "end": v(-25.19, 58.98) * mm});
            skLineSegment(sketch, "E290.8.2.2", {"start": v(-30.12, 63.9) * mm, "end": v(-35.04, 58.98) * mm});
            skLineSegment(sketch, "E290.8.2.3", {"start": v(-35.04, 58.98) * mm, "end": v(-25.19, 58.98) * mm});
            skLineSegment(sketch, "E290.8.2.4", {"start": v(-35.04, 55.17) * mm, "end": v(-25.19, 55.17) * mm});
            skLineSegment(sketch, "E290.8.2.5", {"start": v(-30.12, 50.24) * mm, "end": v(-35.04, 55.17) * mm});
            skLineSegment(sketch, "E290.8.2.7", {"start": v(-30.12, 50.24) * mm, "end": v(-25.19, 55.17) * mm});
            skLineSegment(sketch, "E290.8.2.8", {"start": v(-27.42, 47.55) * mm, "end": v(-22.5, 52.48) * mm});
            skLineSegment(sketch, "E290.8.2.9", {"start": v(-22.5, 52.48) * mm, "end": v(-17.57, 47.55) * mm});
            skLineSegment(sketch, "E290.8.2.10", {"start": v(-27.42, 47.55) * mm, "end": v(-17.57, 47.55) * mm});
            skLineSegment(sketch, "E290.8.2.11", {"start": v(-27.42, 66.6) * mm, "end": v(-22.5, 61.67) * mm});
            skLineSegment(sketch, "E290.8.2.12", {"start": v(-27.42, 66.6) * mm, "end": v(-17.57, 66.6) * mm});
            skLineSegment(sketch, "E290.8.2.13", {"start": v(-22.5, 61.67) * mm, "end": v(-17.57, 66.6) * mm});
            skLineSegment(sketch, "E290.9.2.0", {"start": v(-14.88, 63.9) * mm, "end": v(-9.95, 58.98) * mm});
            skLineSegment(sketch, "E290.9.2.2", {"start": v(-14.88, 63.9) * mm, "end": v(-19.8, 58.98) * mm});
            skLineSegment(sketch, "E290.9.2.3", {"start": v(-19.8, 58.98) * mm, "end": v(-9.95, 58.98) * mm});
            skLineSegment(sketch, "E290.9.2.4", {"start": v(-19.8, 55.17) * mm, "end": v(-9.95, 55.17) * mm});
            skLineSegment(sketch, "E290.9.2.5", {"start": v(-14.88, 50.24) * mm, "end": v(-19.8, 55.17) * mm});
            skLineSegment(sketch, "E290.9.2.7", {"start": v(-14.88, 50.24) * mm, "end": v(-9.95, 55.17) * mm});
            skLineSegment(sketch, "E290.9.2.8", {"start": v(-12.18, 47.55) * mm, "end": v(-7.26, 52.48) * mm});
            skLineSegment(sketch, "E290.9.2.9", {"start": v(-7.26, 52.48) * mm, "end": v(-2.33, 47.55) * mm});
            skLineSegment(sketch, "E290.9.2.10", {"start": v(-12.18, 47.55) * mm, "end": v(-2.33, 47.55) * mm});
            skLineSegment(sketch, "E290.9.2.11", {"start": v(-12.18, 66.6) * mm, "end": v(-7.26, 61.67) * mm});
            skLineSegment(sketch, "E290.9.2.12", {"start": v(-12.18, 66.6) * mm, "end": v(-2.33, 66.6) * mm});
            skLineSegment(sketch, "E290.9.2.13", {"start": v(-7.26, 61.67) * mm, "end": v(-2.33, 66.6) * mm});
            skLineSegment(sketch, "E290.10.2.0", {"start": v(0.36, 63.9) * mm, "end": v(5.3, 58.98) * mm});
            skLineSegment(sketch, "E290.10.2.2", {"start": v(0.36, 63.9) * mm, "end": v(-4.56, 58.98) * mm});
            skLineSegment(sketch, "E290.10.2.3", {"start": v(-4.56, 58.98) * mm, "end": v(5.3, 58.98) * mm});
            skLineSegment(sketch, "E290.10.2.4", {"start": v(-4.56, 55.17) * mm, "end": v(5.3, 55.17) * mm});
            skLineSegment(sketch, "E290.10.2.5", {"start": v(0.36, 50.24) * mm, "end": v(-4.56, 55.17) * mm});
            skLineSegment(sketch, "E290.10.2.7", {"start": v(0.36, 50.24) * mm, "end": v(5.3, 55.17) * mm});
            skLineSegment(sketch, "E290.10.2.8", {"start": v(3.06, 47.55) * mm, "end": v(7.98, 52.48) * mm});
            skLineSegment(sketch, "E290.10.2.11", {"start": v(3.06, 66.6) * mm, "end": v(7.98, 61.67) * mm});
            skLineSegment(sketch, "E290.10.2.12", {"start": v(3.06, 66.6) * mm, "end": v(7.98, 66.6) * mm});
            skLineSegment(sketch, "E291", {"start": v(7.98, 52.48) * mm, "end": v(7.98, 47.55) * mm});
            skLineSegment(sketch, "E292", {"start": v(7.98, 61.67) * mm, "end": v(7.98, 66.6) * mm});
            skLineSegment(sketch, "E293", {"start": v(3.06, 47.55) * mm, "end": v(7.98, 47.55) * mm});
            skLineSegment(sketch, "E294.0.2.0", {"start": v(-159.66, 61.67) * mm, "end": v(-159.66, 66.6) * mm});
            skLineSegment(sketch, "E294.0.2.1", {"start": v(-159.66, 66.6) * mm, "end": v(-154.73, 66.6) * mm});
            skLineSegment(sketch, "E294.0.2.2", {"start": v(-154.73, 66.6) * mm, "end": v(-159.66, 61.67) * mm});
            skLineSegment(sketch, "E294.0.2.3", {"start": v(-159.66, 52.48) * mm, "end": v(-159.66, 47.55) * mm});
            skLineSegment(sketch, "E294.0.2.4", {"start": v(-159.66, 52.48) * mm, "end": v(-154.73, 47.55) * mm});
            skLineSegment(sketch, "E294.0.2.5", {"start": v(-154.73, 47.55) * mm, "end": v(-159.66, 47.55) * mm});
            skLineSegment(sketch, "E295.0.1.0", {"start": v(-126.48, 36.12) * mm, "end": v(-116.63, 36.12) * mm});
            skLineSegment(sketch, "E295.0.1.1", {"start": v(-113.94, 29.62) * mm, "end": v(-109, 24.7) * mm});
            skLineSegment(sketch, "E295.0.1.2", {"start": v(3.06, 43.74) * mm, "end": v(7.98, 38.81) * mm});
            skLineSegment(sketch, "E295.0.1.3", {"start": v(-121.56, 27.38) * mm, "end": v(-116.63, 32.31) * mm});
            skLineSegment(sketch, "E295.0.1.4", {"start": v(-73.14, 43.74) * mm, "end": v(-63.29, 43.74) * mm});
            skLineSegment(sketch, "E295.0.1.5", {"start": v(-103.62, 24.7) * mm, "end": v(-93.77, 24.7) * mm});
            skLineSegment(sketch, "E295.0.1.6", {"start": v(-30.12, 27.38) * mm, "end": v(-25.19, 32.31) * mm});
            skLineSegment(sketch, "E295.0.1.7", {"start": v(-118.86, 24.7) * mm, "end": v(-113.94, 29.62) * mm});
            skLineSegment(sketch, "E295.0.1.8", {"start": v(-42.66, 43.74) * mm, "end": v(-32.8, 43.74) * mm});
            skLineSegment(sketch, "E295.0.1.9", {"start": v(-129.18, 29.62) * mm, "end": v(-124.25, 24.7) * mm});
            skLineSegment(sketch, "E295.0.1.10", {"start": v(0.36, 27.38) * mm, "end": v(5.3, 32.31) * mm});
            skLineSegment(sketch, "E295.0.1.11", {"start": v(-57.9, 43.74) * mm, "end": v(-52.98, 38.81) * mm});
            skLineSegment(sketch, "E295.0.1.12", {"start": v(-14.88, 27.38) * mm, "end": v(-9.95, 32.31) * mm});
            skLineSegment(sketch, "E295.0.1.13", {"start": v(-88.38, 43.74) * mm, "end": v(-78.53, 43.74) * mm});
            skLineSegment(sketch, "E295.0.1.14", {"start": v(-106.32, 41.05) * mm, "end": v(-101.39, 36.12) * mm});
            skLineSegment(sketch, "E295.0.1.15", {"start": v(-60.6, 41.05) * mm, "end": v(-65.52, 36.12) * mm});
            skLineSegment(sketch, "E295.0.1.16", {"start": v(-156.96, 36.12) * mm, "end": v(-147.1, 36.12) * mm});
            skLineSegment(sketch, "E295.0.1.17", {"start": v(-156.96, 32.31) * mm, "end": v(-147.1, 32.31) * mm});
            skLineSegment(sketch, "E295.0.1.18", {"start": v(-134.1, 24.7) * mm, "end": v(-124.25, 24.7) * mm});
            skLineSegment(sketch, "E295.0.1.19", {"start": v(-144.42, 29.62) * mm, "end": v(-139.49, 24.7) * mm});
            skLineSegment(sketch, "E295.0.1.20", {"start": v(-45.36, 27.38) * mm, "end": v(-40.43, 32.31) * mm});
            skLineSegment(sketch, "E295.0.1.21", {"start": v(-134.1, 43.74) * mm, "end": v(-124.25, 43.74) * mm});
            skLineSegment(sketch, "E295.0.1.22", {"start": v(-45.36, 41.05) * mm, "end": v(-50.28, 36.12) * mm});
            skLineSegment(sketch, "E295.0.1.23", {"start": v(0.36, 27.38) * mm, "end": v(-4.56, 32.31) * mm});
            skLineSegment(sketch, "E295.0.1.24", {"start": v(-103.62, 24.7) * mm, "end": v(-98.7, 29.62) * mm});
            skLineSegment(sketch, "E295.0.1.25", {"start": v(-121.56, 41.05) * mm, "end": v(-126.48, 36.12) * mm});
            skLineSegment(sketch, "E295.0.1.26", {"start": v(-106.32, 27.38) * mm, "end": v(-101.39, 32.31) * mm});
            skLineSegment(sketch, "E295.0.1.27", {"start": v(-35.04, 36.12) * mm, "end": v(-25.19, 36.12) * mm});
            skLineSegment(sketch, "E295.0.1.28", {"start": v(-22.5, 38.81) * mm, "end": v(-17.57, 43.74) * mm});
            skLineSegment(sketch, "E295.0.1.29", {"start": v(-60.6, 27.38) * mm, "end": v(-65.52, 32.31) * mm});
            skLineSegment(sketch, "E295.0.1.30", {"start": v(-30.12, 41.05) * mm, "end": v(-25.19, 36.12) * mm});
            skLineSegment(sketch, "E295.0.1.31", {"start": v(-118.86, 24.7) * mm, "end": v(-109, 24.7) * mm});
            skLineSegment(sketch, "E295.0.1.32", {"start": v(-88.38, 43.74) * mm, "end": v(-83.46, 38.81) * mm});
            skLineSegment(sketch, "E295.0.1.33", {"start": v(-19.8, 36.12) * mm, "end": v(-9.95, 36.12) * mm});
            skLineSegment(sketch, "E295.0.1.34", {"start": v(-106.32, 41.05) * mm, "end": v(-111.24, 36.12) * mm});
            skLineSegment(sketch, "E295.0.1.35", {"start": v(-134.1, 43.74) * mm, "end": v(-129.18, 38.81) * mm});
            skLineSegment(sketch, "E295.0.1.36", {"start": v(-91.08, 27.38) * mm, "end": v(-96, 32.31) * mm});
            skLineSegment(sketch, "E295.0.1.37", {"start": v(-103.62, 43.74) * mm, "end": v(-93.77, 43.74) * mm});
            skLineSegment(sketch, "E295.0.1.38", {"start": v(-75.84, 41.05) * mm, "end": v(-80.76, 36.12) * mm});
            skLineSegment(sketch, "E295.0.1.39", {"start": v(-111.24, 32.31) * mm, "end": v(-101.39, 32.31) * mm});
            skLineSegment(sketch, "E295.0.1.40", {"start": v(-65.52, 36.12) * mm, "end": v(-55.67, 36.12) * mm});
            skLineSegment(sketch, "E295.0.1.41", {"start": v(0.36, 41.05) * mm, "end": v(5.3, 36.12) * mm});
            skLineSegment(sketch, "E295.0.1.42", {"start": v(-19.8, 32.31) * mm, "end": v(-9.95, 32.31) * mm});
            skLineSegment(sketch, "E295.0.1.43", {"start": v(-45.36, 27.38) * mm, "end": v(-50.28, 32.31) * mm});
            skLineSegment(sketch, "E295.0.1.44", {"start": v(-27.42, 24.7) * mm, "end": v(-17.57, 24.7) * mm});
            skLineSegment(sketch, "E295.0.1.45", {"start": v(-57.9, 43.74) * mm, "end": v(-48.05, 43.74) * mm});
            skLineSegment(sketch, "E295.0.1.46", {"start": v(-52.98, 29.62) * mm, "end": v(-48.05, 24.7) * mm});
            skLineSegment(sketch, "E295.0.1.47", {"start": v(-80.76, 32.31) * mm, "end": v(-70.9, 32.31) * mm});
            skLineSegment(sketch, "E295.0.1.48", {"start": v(-14.88, 27.38) * mm, "end": v(-19.8, 32.31) * mm});
            skLineSegment(sketch, "E295.0.1.49", {"start": v(-12.18, 24.7) * mm, "end": v(-2.33, 24.7) * mm});
            skLineSegment(sketch, "E295.0.1.50", {"start": v(0.36, 41.05) * mm, "end": v(-4.56, 36.12) * mm});
            skLineSegment(sketch, "E295.0.1.51", {"start": v(-149.34, 43.74) * mm, "end": v(-144.42, 38.81) * mm});
            skLineSegment(sketch, "E295.0.1.52", {"start": v(-12.18, 43.74) * mm, "end": v(-7.26, 38.81) * mm});
            skLineSegment(sketch, "E295.0.1.53", {"start": v(-30.12, 27.38) * mm, "end": v(-35.04, 32.31) * mm});
            skLineSegment(sketch, "E295.0.1.54", {"start": v(-96, 36.12) * mm, "end": v(-86.15, 36.12) * mm});
            skLineSegment(sketch, "E295.0.1.55", {"start": v(-75.84, 27.38) * mm, "end": v(-70.9, 32.31) * mm});
            skLineSegment(sketch, "E295.0.1.56", {"start": v(-50.28, 32.31) * mm, "end": v(-40.43, 32.31) * mm});
            skLineSegment(sketch, "E295.0.1.57", {"start": v(-7.26, 29.62) * mm, "end": v(-2.33, 24.7) * mm});
            skLineSegment(sketch, "E295.0.1.58", {"start": v(-106.32, 27.38) * mm, "end": v(-111.24, 32.31) * mm});
            skLineSegment(sketch, "E295.0.1.59", {"start": v(-57.9, 24.7) * mm, "end": v(-48.05, 24.7) * mm});
            skLineSegment(sketch, "E295.0.1.60", {"start": v(-52.98, 38.81) * mm, "end": v(-48.05, 43.74) * mm});
            skLineSegment(sketch, "E295.0.1.61", {"start": v(-42.66, 24.7) * mm, "end": v(-32.8, 24.7) * mm});
            skLineSegment(sketch, "E295.0.1.62", {"start": v(-35.04, 32.31) * mm, "end": v(-25.19, 32.31) * mm});
            skLineSegment(sketch, "E295.0.1.63", {"start": v(-12.18, 43.74) * mm, "end": v(-2.33, 43.74) * mm});
            skLineSegment(sketch, "E295.0.1.64", {"start": v(-121.56, 41.05) * mm, "end": v(-116.63, 36.12) * mm});
            skLineSegment(sketch, "E295.0.1.65", {"start": v(-27.42, 24.7) * mm, "end": v(-22.5, 29.62) * mm});
            skLineSegment(sketch, "E295.0.1.66", {"start": v(-73.14, 24.7) * mm, "end": v(-68.22, 29.62) * mm});
            skLineSegment(sketch, "E295.0.1.67", {"start": v(-4.56, 36.12) * mm, "end": v(5.3, 36.12) * mm});
            skLineSegment(sketch, "E295.0.1.68", {"start": v(-83.46, 29.62) * mm, "end": v(-78.53, 24.7) * mm});
            skLineSegment(sketch, "E295.0.1.69", {"start": v(-73.14, 24.7) * mm, "end": v(-63.29, 24.7) * mm});
            skLineSegment(sketch, "E295.0.1.70", {"start": v(-42.66, 24.7) * mm, "end": v(-37.74, 29.62) * mm});
            skLineSegment(sketch, "E295.0.1.71", {"start": v(-27.42, 43.74) * mm, "end": v(-22.5, 38.81) * mm});
            skLineSegment(sketch, "E295.0.1.72", {"start": v(-30.12, 41.05) * mm, "end": v(-35.04, 36.12) * mm});
            skLineSegment(sketch, "E295.0.1.73", {"start": v(-45.36, 41.05) * mm, "end": v(-40.43, 36.12) * mm});
            skLineSegment(sketch, "E295.0.1.74", {"start": v(-91.08, 41.05) * mm, "end": v(-86.15, 36.12) * mm});
            skLineSegment(sketch, "E295.0.1.75", {"start": v(-149.34, 24.7) * mm, "end": v(-139.49, 24.7) * mm});
            skLineSegment(sketch, "E295.0.1.76", {"start": v(-14.88, 41.05) * mm, "end": v(-19.8, 36.12) * mm});
            skLineSegment(sketch, "E295.0.1.77", {"start": v(-98.7, 38.81) * mm, "end": v(-93.77, 43.74) * mm});
            skLineSegment(sketch, "E295.0.1.78", {"start": v(-88.38, 24.7) * mm, "end": v(-78.53, 24.7) * mm});
            skLineSegment(sketch, "E295.0.1.79", {"start": v(3.06, 24.7) * mm, "end": v(7.98, 29.62) * mm});
            skLineSegment(sketch, "E295.0.1.80", {"start": v(-73.14, 43.74) * mm, "end": v(-68.22, 38.81) * mm});
            skLineSegment(sketch, "E295.0.1.81", {"start": v(-152.04, 27.38) * mm, "end": v(-156.96, 32.31) * mm});
            skLineSegment(sketch, "E295.0.1.82", {"start": v(-149.34, 24.7) * mm, "end": v(-144.42, 29.62) * mm});
            skLineSegment(sketch, "E295.0.1.83", {"start": v(-42.66, 43.74) * mm, "end": v(-37.74, 38.81) * mm});
            skLineSegment(sketch, "E295.0.1.84", {"start": v(-118.86, 43.74) * mm, "end": v(-113.94, 38.81) * mm});
            skLineSegment(sketch, "E295.0.1.85", {"start": v(-4.56, 32.31) * mm, "end": v(5.3, 32.31) * mm});
            skLineSegment(sketch, "E295.0.1.86", {"start": v(-50.28, 36.12) * mm, "end": v(-40.43, 36.12) * mm});
            skLineSegment(sketch, "E295.0.1.87", {"start": v(-80.76, 36.12) * mm, "end": v(-70.9, 36.12) * mm});
            skLineSegment(sketch, "E295.0.1.88", {"start": v(-136.8, 41.05) * mm, "end": v(-131.87, 36.12) * mm});
            skLineSegment(sketch, "E295.0.1.89", {"start": v(-98.7, 29.62) * mm, "end": v(-93.77, 24.7) * mm});
            skLineSegment(sketch, "E295.0.1.90", {"start": v(-149.34, 43.74) * mm, "end": v(-139.49, 43.74) * mm});
            skLineSegment(sketch, "E295.0.1.91", {"start": v(-22.5, 29.62) * mm, "end": v(-17.57, 24.7) * mm});
            skLineSegment(sketch, "E295.0.1.92", {"start": v(-88.38, 24.7) * mm, "end": v(-83.46, 29.62) * mm});
            skLineSegment(sketch, "E295.0.1.93", {"start": v(-60.6, 27.38) * mm, "end": v(-55.67, 32.31) * mm});
            skLineSegment(sketch, "E295.0.1.94", {"start": v(-7.26, 38.81) * mm, "end": v(-2.33, 43.74) * mm});
            skLineSegment(sketch, "E295.0.1.95", {"start": v(-134.1, 24.7) * mm, "end": v(-129.18, 29.62) * mm});
            skLineSegment(sketch, "E295.0.1.96", {"start": v(-154.73, 43.74) * mm, "end": v(-159.66, 38.81) * mm});
            skLineSegment(sketch, "E295.0.1.97", {"start": v(-118.86, 43.74) * mm, "end": v(-109, 43.74) * mm});
            skLineSegment(sketch, "E295.0.1.98", {"start": v(-126.48, 32.31) * mm, "end": v(-116.63, 32.31) * mm});
            skLineSegment(sketch, "E295.0.1.99", {"start": v(-37.74, 29.62) * mm, "end": v(-32.8, 24.7) * mm});
            skLineSegment(sketch, "E295.0.1.100", {"start": v(-136.8, 41.05) * mm, "end": v(-141.72, 36.12) * mm});
            skLineSegment(sketch, "E295.0.1.101", {"start": v(-141.72, 36.12) * mm, "end": v(-131.87, 36.12) * mm});
            skLineSegment(sketch, "E295.0.1.102", {"start": v(-152.04, 27.38) * mm, "end": v(-147.1, 32.31) * mm});
            skLineSegment(sketch, "E295.0.1.103", {"start": v(-75.84, 41.05) * mm, "end": v(-70.9, 36.12) * mm});
            skLineSegment(sketch, "E295.0.1.104", {"start": v(-91.08, 27.38) * mm, "end": v(-86.15, 32.31) * mm});
            skLineSegment(sketch, "E295.0.1.105", {"start": v(-91.08, 41.05) * mm, "end": v(-96, 36.12) * mm});
            skLineSegment(sketch, "E295.0.1.106", {"start": v(-144.42, 38.81) * mm, "end": v(-139.49, 43.74) * mm});
            skLineSegment(sketch, "E295.0.1.107", {"start": v(-57.9, 24.7) * mm, "end": v(-52.98, 29.62) * mm});
            skLineSegment(sketch, "E295.0.1.108", {"start": v(-83.46, 38.81) * mm, "end": v(-78.53, 43.74) * mm});
            skLineSegment(sketch, "E295.0.1.109", {"start": v(-121.56, 27.38) * mm, "end": v(-126.48, 32.31) * mm});
            skLineSegment(sketch, "E295.0.1.110", {"start": v(-27.42, 43.74) * mm, "end": v(-17.57, 43.74) * mm});
            skLineSegment(sketch, "E295.0.1.111", {"start": v(-12.18, 24.7) * mm, "end": v(-7.26, 29.62) * mm});
            skLineSegment(sketch, "E295.0.1.112", {"start": v(-14.88, 41.05) * mm, "end": v(-9.95, 36.12) * mm});
            skLineSegment(sketch, "E295.0.1.113", {"start": v(-141.72, 32.31) * mm, "end": v(-131.87, 32.31) * mm});
            skLineSegment(sketch, "E295.0.1.114", {"start": v(-129.18, 38.81) * mm, "end": v(-124.25, 43.74) * mm});
            skLineSegment(sketch, "E295.0.1.115", {"start": v(-68.22, 29.62) * mm, "end": v(-63.29, 24.7) * mm});
            skLineSegment(sketch, "E295.0.1.116", {"start": v(-75.84, 27.38) * mm, "end": v(-80.76, 32.31) * mm});
            skLineSegment(sketch, "E295.0.1.117", {"start": v(-96, 32.31) * mm, "end": v(-86.15, 32.31) * mm});
            skLineSegment(sketch, "E295.0.1.118", {"start": v(-60.6, 41.05) * mm, "end": v(-55.67, 36.12) * mm});
            skLineSegment(sketch, "E295.0.1.119", {"start": v(-37.74, 38.81) * mm, "end": v(-32.8, 43.74) * mm});
            skLineSegment(sketch, "E295.0.1.120", {"start": v(-136.8, 27.38) * mm, "end": v(-141.72, 32.31) * mm});
            skLineSegment(sketch, "E295.0.1.121", {"start": v(-136.8, 27.38) * mm, "end": v(-131.87, 32.31) * mm});
            skLineSegment(sketch, "E295.0.1.122", {"start": v(-111.24, 36.12) * mm, "end": v(-101.39, 36.12) * mm});
            skLineSegment(sketch, "E295.0.1.123", {"start": v(-65.52, 32.31) * mm, "end": v(-55.67, 32.31) * mm});
            skLineSegment(sketch, "E295.0.1.124", {"start": v(-152.04, 41.05) * mm, "end": v(-147.1, 36.12) * mm});
            skLineSegment(sketch, "E295.0.1.125", {"start": v(-152.04, 41.05) * mm, "end": v(-156.96, 36.12) * mm});
            skLineSegment(sketch, "E295.0.1.126", {"start": v(-68.22, 38.81) * mm, "end": v(-63.29, 43.74) * mm});
            skLineSegment(sketch, "E295.0.1.127", {"start": v(-103.62, 43.74) * mm, "end": v(-98.7, 38.81) * mm});
            skLineSegment(sketch, "E295.0.1.128", {"start": v(-113.94, 38.81) * mm, "end": v(-109, 43.74) * mm});
            skLineSegment(sketch, "E295.0.1.129", {"start": v(-159.66, 29.62) * mm, "end": v(-154.73, 24.7) * mm});
            skLineSegment(sketch, "E295.0.1.130", {"start": v(-154.73, 24.7) * mm, "end": v(-159.66, 24.7) * mm});
            skLineSegment(sketch, "E295.0.1.131", {"start": v(7.98, 38.81) * mm, "end": v(7.98, 43.74) * mm});
            skLineSegment(sketch, "E295.0.1.132", {"start": v(7.98, 29.62) * mm, "end": v(7.98, 24.7) * mm});
            skLineSegment(sketch, "E295.0.1.133", {"start": v(3.06, 24.7) * mm, "end": v(7.98, 24.7) * mm});
            skLineSegment(sketch, "E295.0.1.134", {"start": v(-159.66, 29.62) * mm, "end": v(-159.66, 24.7) * mm});
            skLineSegment(sketch, "E295.0.1.135", {"start": v(3.06, 43.74) * mm, "end": v(7.98, 43.74) * mm});
            skLineSegment(sketch, "E295.0.1.136", {"start": v(-159.66, 43.74) * mm, "end": v(-154.73, 43.74) * mm});
            skLineSegment(sketch, "E295.0.1.137", {"start": v(-159.66, 38.81) * mm, "end": v(-159.66, 43.74) * mm});
            skLineSegment(sketch, "E295.0.2.1", {"start": v(-113.94, 6.76) * mm, "end": v(-109, 1.83) * mm});
            skLineSegment(sketch, "E295.0.2.2", {"start": v(3.06, 20.88) * mm, "end": v(7.98, 15.95) * mm});
            skLineSegment(sketch, "E295.0.2.5", {"start": v(-103.62, 1.83) * mm, "end": v(-93.77, 1.83) * mm});
            skLineSegment(sketch, "E295.0.2.7", {"start": v(-118.86, 1.83) * mm, "end": v(-113.94, 6.76) * mm});
            skLineSegment(sketch, "E295.0.2.9", {"start": v(-129.18, 6.76) * mm, "end": v(-124.25, 1.83) * mm});
            skLineSegment(sketch, "E295.0.2.10", {"start": v(0.36, 4.52) * mm, "end": v(5.3, 9.45) * mm});
            skLineSegment(sketch, "E295.0.2.12", {"start": v(-14.88, 4.52) * mm, "end": v(-9.95, 9.45) * mm});
            skLineSegment(sketch, "E295.0.2.18", {"start": v(-134.1, 1.83) * mm, "end": v(-124.25, 1.83) * mm});
            skLineSegment(sketch, "E295.0.2.19", {"start": v(-144.42, 6.76) * mm, "end": v(-139.49, 1.83) * mm});
            skLineSegment(sketch, "E295.0.2.23", {"start": v(0.36, 4.52) * mm, "end": v(-4.56, 9.45) * mm});
            skLineSegment(sketch, "E295.0.2.24", {"start": v(-103.62, 1.83) * mm, "end": v(-98.7, 6.76) * mm});
            skLineSegment(sketch, "E295.0.2.31", {"start": v(-118.86, 1.83) * mm, "end": v(-109, 1.83) * mm});
            skLineSegment(sketch, "E295.0.2.33", {"start": v(-14.88, 13.26) * mm, "end": v(-9.95, 13.26) * mm});
            skLineSegment(sketch, "E295.0.2.41", {"start": v(0.36, 18.19) * mm, "end": v(5.3, 13.26) * mm});
            skLineSegment(sketch, "E295.0.2.42", {"start": v(-14.88, 9.45) * mm, "end": v(-9.95, 9.45) * mm});
            skLineSegment(sketch, "E295.0.2.46", {"start": v(-52.98, 6.76) * mm, "end": v(-48.05, 1.83) * mm});
            skLineSegment(sketch, "E295.0.2.49", {"start": v(-12.18, 1.83) * mm, "end": v(-2.33, 1.83) * mm});
            skLineSegment(sketch, "E295.0.2.50", {"start": v(0.36, 18.19) * mm, "end": v(-4.56, 13.26) * mm});
            skLineSegment(sketch, "E295.0.2.52", {"start": v(-12.18, 20.88) * mm, "end": v(-7.26, 15.95) * mm});
            skLineSegment(sketch, "E295.0.2.57", {"start": v(-7.26, 6.76) * mm, "end": v(-2.33, 1.83) * mm});
            skLineSegment(sketch, "E295.0.2.59", {"start": v(-57.9, 1.83) * mm, "end": v(-48.05, 1.83) * mm});
            skLineSegment(sketch, "E295.0.2.61", {"start": v(-42.66, 1.83) * mm, "end": v(-32.8, 1.83) * mm});
            skLineSegment(sketch, "E295.0.2.63", {"start": v(-12.18, 20.88) * mm, "end": v(-2.33, 20.88) * mm});
            skLineSegment(sketch, "E295.0.2.66", {"start": v(-73.14, 1.83) * mm, "end": v(-68.22, 6.76) * mm});
            skLineSegment(sketch, "E295.0.2.67", {"start": v(-4.56, 13.26) * mm, "end": v(5.3, 13.26) * mm});
            skLineSegment(sketch, "E295.0.2.68", {"start": v(-83.46, 6.76) * mm, "end": v(-78.53, 1.83) * mm});
            skLineSegment(sketch, "E295.0.2.69", {"start": v(-73.14, 1.83) * mm, "end": v(-63.29, 1.83) * mm});
            skLineSegment(sketch, "E295.0.2.70", {"start": v(-42.66, 1.83) * mm, "end": v(-37.74, 6.76) * mm});
            skLineSegment(sketch, "E295.0.2.75", {"start": v(-149.34, 1.83) * mm, "end": v(-139.49, 1.83) * mm});
            skLineSegment(sketch, "E295.0.2.78", {"start": v(-88.38, 1.83) * mm, "end": v(-78.53, 1.83) * mm});
            skLineSegment(sketch, "E295.0.2.79", {"start": v(3.06, 1.83) * mm, "end": v(7.98, 6.76) * mm});
            skLineSegment(sketch, "E295.0.2.82", {"start": v(-149.34, 1.83) * mm, "end": v(-144.42, 6.76) * mm});
            skLineSegment(sketch, "E295.0.2.85", {"start": v(-4.56, 9.45) * mm, "end": v(5.3, 9.45) * mm});
            skLineSegment(sketch, "E295.0.2.89", {"start": v(-98.7, 6.76) * mm, "end": v(-93.77, 1.83) * mm});
            skLineSegment(sketch, "E295.0.2.92", {"start": v(-88.38, 1.83) * mm, "end": v(-83.46, 6.76) * mm});
            skLineSegment(sketch, "E295.0.2.94", {"start": v(-7.26, 15.95) * mm, "end": v(-2.33, 20.88) * mm});
            skLineSegment(sketch, "E295.0.2.95", {"start": v(-134.1, 1.83) * mm, "end": v(-129.18, 6.76) * mm});
            skLineSegment(sketch, "E295.0.2.99", {"start": v(-37.74, 6.76) * mm, "end": v(-32.8, 1.83) * mm});
            skLineSegment(sketch, "E295.0.2.107", {"start": v(-57.9, 1.83) * mm, "end": v(-52.98, 6.76) * mm});
            skLineSegment(sketch, "E295.0.2.111", {"start": v(-12.18, 1.83) * mm, "end": v(-7.26, 6.76) * mm});
            skLineSegment(sketch, "E295.0.2.112", {"start": v(-14.88, 18.19) * mm, "end": v(-9.95, 13.26) * mm});
            skLineSegment(sketch, "E295.0.2.115", {"start": v(-68.22, 6.76) * mm, "end": v(-63.29, 1.83) * mm});
            skLineSegment(sketch, "E295.0.2.131", {"start": v(7.98, 15.95) * mm, "end": v(7.98, 20.88) * mm});
            skLineSegment(sketch, "E295.0.2.132", {"start": v(7.98, 6.76) * mm, "end": v(7.98, 1.83) * mm});
            skLineSegment(sketch, "E295.0.2.133", {"start": v(3.06, 1.83) * mm, "end": v(7.98, 1.83) * mm});
            skLineSegment(sketch, "E295.0.2.135", {"start": v(3.06, 20.88) * mm, "end": v(7.98, 20.88) * mm});
            skLineSegment(sketch, "E295.direction1", {"start": v(-159.66, 47.55) * mm, "end": v(-134.26, 47.55) * mm, "construction": true});
            skLineSegment(sketch, "E295.direction2", {"start": v(-159.66, 47.55) * mm, "end": v(-159.66, 24.7) * mm, "construction": true});
            skLineSegment(sketch, "E296", {"start": v(-14.88, 18.19) * mm, "end": v(-14.88, 13.26) * mm});
            skLineSegment(sketch, "E297", {"start": v(-14.88, 9.45) * mm, "end": v(-14.88, 4.52) * mm});
            skSolve(sketch);
        }
        {
            var Q0;
            Q0=qSketchRegion(id+"F30",true);
            extrude(context, id + "F31", {"entities" : qUnion([Q0]), "operationType" : NewBodyOperationType.REMOVE, "oppositeDirection" : true, "depth" : 2.54 * mm, "offsetDistance" : 25.4 * mm});
        }
        {
            var Q0;
            Q0=makeQuery(id+"F6.boolean.opBoolean","MERGE",FACE,{"derivedFrom":[makeQuery(id+"F2.opExtrude","SWEPT_FACE",FACE,{"disambiguationData":[OSD([sQuery(id+"F1.wireOp",EDGE,"E9.1")])]}),makeQuery(id+"F6.opExtrude","SWEPT_FACE",FACE,{"disambiguationData":[OSD([sQuery(id+"F5.wireOp",EDGE,"E60.left")])]})]});
            var sketch = newSketch(context, id + "F32", { "sketchPlane" : qUnion([Q0])});
            skLineSegment(sketch, "E298.0.2.0", {"start": v(-1.8, 64.62) * mm, "end": v(3.13, 59.69) * mm});
            skLineSegment(sketch, "E298.0.2.2", {"start": v(-1.8, 64.62) * mm, "end": v(-6.73, 59.69) * mm});
            skLineSegment(sketch, "E298.0.2.3", {"start": v(-6.73, 59.69) * mm, "end": v(3.13, 59.69) * mm});
            skLineSegment(sketch, "E298.0.2.4", {"start": v(-6.73, 55.88) * mm, "end": v(3.13, 55.88) * mm});
            skLineSegment(sketch, "E298.0.2.5", {"start": v(-1.8, 50.95) * mm, "end": v(-6.73, 55.88) * mm});
            skLineSegment(sketch, "E298.0.2.7", {"start": v(-1.8, 50.95) * mm, "end": v(3.13, 55.88) * mm});
            skLineSegment(sketch, "E298.0.2.8", {"start": v(0.9, 48.26) * mm, "end": v(5.82, 53.19) * mm});
            skLineSegment(sketch, "E298.0.2.9", {"start": v(5.82, 53.19) * mm, "end": v(10.75, 48.26) * mm});
            skLineSegment(sketch, "E298.0.2.10", {"start": v(0.9, 48.26) * mm, "end": v(10.75, 48.26) * mm});
            skLineSegment(sketch, "E298.0.2.11", {"start": v(0.9, 67.3) * mm, "end": v(5.82, 62.38) * mm});
            skLineSegment(sketch, "E298.0.2.12", {"start": v(0.9, 67.3) * mm, "end": v(10.75, 67.3) * mm});
            skLineSegment(sketch, "E298.0.2.13", {"start": v(5.82, 62.38) * mm, "end": v(10.75, 67.3) * mm});
            skLineSegment(sketch, "E298.1.2.0", {"start": v(13.44, 64.62) * mm, "end": v(18.37, 59.69) * mm});
            skLineSegment(sketch, "E298.1.2.2", {"start": v(13.44, 64.62) * mm, "end": v(8.51, 59.69) * mm});
            skLineSegment(sketch, "E298.1.2.3", {"start": v(8.51, 59.69) * mm, "end": v(18.37, 59.69) * mm});
            skLineSegment(sketch, "E298.1.2.4", {"start": v(8.51, 55.88) * mm, "end": v(18.37, 55.88) * mm});
            skLineSegment(sketch, "E298.1.2.5", {"start": v(13.44, 50.95) * mm, "end": v(8.51, 55.88) * mm});
            skLineSegment(sketch, "E298.1.2.7", {"start": v(13.44, 50.95) * mm, "end": v(18.37, 55.88) * mm});
            skLineSegment(sketch, "E298.1.2.8", {"start": v(16.13, 48.26) * mm, "end": v(21.06, 53.19) * mm});
            skLineSegment(sketch, "E298.1.2.9", {"start": v(21.06, 53.19) * mm, "end": v(25.99, 48.26) * mm});
            skLineSegment(sketch, "E298.1.2.10", {"start": v(16.13, 48.26) * mm, "end": v(25.99, 48.26) * mm});
            skLineSegment(sketch, "E298.1.2.11", {"start": v(16.13, 67.3) * mm, "end": v(21.06, 62.38) * mm});
            skLineSegment(sketch, "E298.1.2.12", {"start": v(16.13, 67.3) * mm, "end": v(25.99, 67.3) * mm});
            skLineSegment(sketch, "E298.1.2.13", {"start": v(21.06, 62.38) * mm, "end": v(25.99, 67.3) * mm});
            skLineSegment(sketch, "E298.2.2.0", {"start": v(28.68, 64.62) * mm, "end": v(33.6, 59.69) * mm});
            skLineSegment(sketch, "E298.2.2.2", {"start": v(28.68, 64.62) * mm, "end": v(23.75, 59.69) * mm});
            skLineSegment(sketch, "E298.2.2.3", {"start": v(23.75, 59.69) * mm, "end": v(33.6, 59.69) * mm});
            skLineSegment(sketch, "E298.2.2.4", {"start": v(23.75, 55.88) * mm, "end": v(33.6, 55.88) * mm});
            skLineSegment(sketch, "E298.2.2.5", {"start": v(28.68, 50.95) * mm, "end": v(23.75, 55.88) * mm});
            skLineSegment(sketch, "E298.2.2.7", {"start": v(28.68, 50.95) * mm, "end": v(33.6, 55.88) * mm});
            skLineSegment(sketch, "E298.2.2.8", {"start": v(31.37, 48.26) * mm, "end": v(36.3, 53.19) * mm});
            skLineSegment(sketch, "E298.2.2.9", {"start": v(36.3, 53.19) * mm, "end": v(41.23, 48.26) * mm});
            skLineSegment(sketch, "E298.2.2.10", {"start": v(31.37, 48.26) * mm, "end": v(41.23, 48.26) * mm});
            skLineSegment(sketch, "E298.2.2.11", {"start": v(31.37, 67.3) * mm, "end": v(36.3, 62.38) * mm});
            skLineSegment(sketch, "E298.2.2.12", {"start": v(31.37, 67.3) * mm, "end": v(41.23, 67.3) * mm});
            skLineSegment(sketch, "E298.2.2.13", {"start": v(36.3, 62.38) * mm, "end": v(41.23, 67.3) * mm});
            skLineSegment(sketch, "E298.3.2.0", {"start": v(43.92, 64.62) * mm, "end": v(48.85, 59.69) * mm});
            skLineSegment(sketch, "E298.3.2.2", {"start": v(43.92, 64.62) * mm, "end": v(39, 59.69) * mm});
            skLineSegment(sketch, "E298.3.2.3", {"start": v(39, 59.69) * mm, "end": v(48.85, 59.69) * mm});
            skLineSegment(sketch, "E298.3.2.4", {"start": v(39, 55.88) * mm, "end": v(48.85, 55.88) * mm});
            skLineSegment(sketch, "E298.3.2.5", {"start": v(43.92, 50.95) * mm, "end": v(39, 55.88) * mm});
            skLineSegment(sketch, "E298.3.2.7", {"start": v(43.92, 50.95) * mm, "end": v(48.85, 55.88) * mm});
            skLineSegment(sketch, "E298.3.2.8", {"start": v(46.61, 48.26) * mm, "end": v(51.54, 53.19) * mm});
            skLineSegment(sketch, "E298.3.2.9", {"start": v(51.54, 53.19) * mm, "end": v(56.47, 48.26) * mm});
            skLineSegment(sketch, "E298.3.2.10", {"start": v(46.61, 48.26) * mm, "end": v(56.47, 48.26) * mm});
            skLineSegment(sketch, "E298.3.2.11", {"start": v(46.61, 67.3) * mm, "end": v(51.54, 62.38) * mm});
            skLineSegment(sketch, "E298.3.2.12", {"start": v(46.61, 67.3) * mm, "end": v(56.47, 67.3) * mm});
            skLineSegment(sketch, "E298.3.2.13", {"start": v(51.54, 62.38) * mm, "end": v(56.47, 67.3) * mm});
            skLineSegment(sketch, "E298.4.2.0", {"start": v(59.16, 64.62) * mm, "end": v(64.09, 59.69) * mm});
            skLineSegment(sketch, "E298.4.2.2", {"start": v(59.16, 64.62) * mm, "end": v(54.23, 59.69) * mm});
            skLineSegment(sketch, "E298.4.2.3", {"start": v(54.23, 59.69) * mm, "end": v(64.09, 59.69) * mm});
            skLineSegment(sketch, "E298.4.2.4", {"start": v(54.23, 55.88) * mm, "end": v(64.09, 55.88) * mm});
            skLineSegment(sketch, "E298.4.2.5", {"start": v(59.16, 50.95) * mm, "end": v(54.23, 55.88) * mm});
            skLineSegment(sketch, "E298.4.2.7", {"start": v(59.16, 50.95) * mm, "end": v(64.09, 55.88) * mm});
            skLineSegment(sketch, "E298.4.2.8", {"start": v(61.85, 48.26) * mm, "end": v(66.78, 53.19) * mm});
            skLineSegment(sketch, "E298.4.2.9", {"start": v(66.78, 53.19) * mm, "end": v(71.7, 48.26) * mm});
            skLineSegment(sketch, "E298.4.2.10", {"start": v(61.85, 48.26) * mm, "end": v(71.7, 48.26) * mm});
            skLineSegment(sketch, "E298.4.2.11", {"start": v(61.85, 67.3) * mm, "end": v(66.78, 62.38) * mm});
            skLineSegment(sketch, "E298.4.2.12", {"start": v(61.85, 67.3) * mm, "end": v(71.7, 67.3) * mm});
            skLineSegment(sketch, "E298.4.2.13", {"start": v(66.78, 62.38) * mm, "end": v(71.7, 67.3) * mm});
            skLineSegment(sketch, "E298.5.2.0", {"start": v(74.4, 64.62) * mm, "end": v(79.33, 59.69) * mm});
            skLineSegment(sketch, "E298.5.2.2", {"start": v(74.4, 64.62) * mm, "end": v(69.47, 59.69) * mm});
            skLineSegment(sketch, "E298.5.2.3", {"start": v(69.47, 59.69) * mm, "end": v(79.33, 59.69) * mm});
            skLineSegment(sketch, "E298.5.2.4", {"start": v(69.47, 55.88) * mm, "end": v(79.33, 55.88) * mm});
            skLineSegment(sketch, "E298.5.2.5", {"start": v(74.4, 50.95) * mm, "end": v(69.47, 55.88) * mm});
            skLineSegment(sketch, "E298.5.2.7", {"start": v(74.4, 50.95) * mm, "end": v(79.33, 55.88) * mm});
            skLineSegment(sketch, "E298.5.2.8", {"start": v(77.1, 48.26) * mm, "end": v(82.02, 53.19) * mm});
            skLineSegment(sketch, "E298.5.2.9", {"start": v(82.02, 53.19) * mm, "end": v(86.95, 48.26) * mm});
            skLineSegment(sketch, "E298.5.2.10", {"start": v(77.1, 48.26) * mm, "end": v(86.95, 48.26) * mm});
            skLineSegment(sketch, "E298.5.2.11", {"start": v(77.1, 67.3) * mm, "end": v(82.02, 62.38) * mm});
            skLineSegment(sketch, "E298.5.2.12", {"start": v(77.1, 67.3) * mm, "end": v(86.95, 67.3) * mm});
            skLineSegment(sketch, "E298.5.2.13", {"start": v(82.02, 62.38) * mm, "end": v(86.95, 67.3) * mm});
            skLineSegment(sketch, "E298.6.2.0", {"start": v(89.64, 64.62) * mm, "end": v(94.57, 59.69) * mm});
            skLineSegment(sketch, "E298.6.2.2", {"start": v(89.64, 64.62) * mm, "end": v(84.71, 59.69) * mm});
            skLineSegment(sketch, "E298.6.2.3", {"start": v(84.71, 59.69) * mm, "end": v(94.57, 59.69) * mm});
            skLineSegment(sketch, "E298.6.2.4", {"start": v(84.71, 55.88) * mm, "end": v(94.57, 55.88) * mm});
            skLineSegment(sketch, "E298.6.2.5", {"start": v(89.64, 50.95) * mm, "end": v(84.71, 55.88) * mm});
            skLineSegment(sketch, "E298.6.2.7", {"start": v(89.64, 50.95) * mm, "end": v(94.57, 55.88) * mm});
            skLineSegment(sketch, "E298.6.2.8", {"start": v(92.33, 48.26) * mm, "end": v(97.26, 53.19) * mm});
            skLineSegment(sketch, "E298.6.2.9", {"start": v(97.26, 53.19) * mm, "end": v(102.19, 48.26) * mm});
            skLineSegment(sketch, "E298.6.2.10", {"start": v(92.33, 48.26) * mm, "end": v(102.19, 48.26) * mm});
            skLineSegment(sketch, "E298.6.2.11", {"start": v(92.33, 67.3) * mm, "end": v(97.26, 62.38) * mm});
            skLineSegment(sketch, "E298.6.2.12", {"start": v(92.33, 67.3) * mm, "end": v(102.19, 67.3) * mm});
            skLineSegment(sketch, "E298.6.2.13", {"start": v(97.26, 62.38) * mm, "end": v(102.19, 67.3) * mm});
            skLineSegment(sketch, "E298.7.2.0", {"start": v(104.88, 64.62) * mm, "end": v(109.8, 59.69) * mm});
            skLineSegment(sketch, "E298.7.2.2", {"start": v(104.88, 64.62) * mm, "end": v(99.95, 59.69) * mm});
            skLineSegment(sketch, "E298.7.2.3", {"start": v(99.95, 59.69) * mm, "end": v(109.8, 59.69) * mm});
            skLineSegment(sketch, "E298.7.2.4", {"start": v(99.95, 55.88) * mm, "end": v(109.8, 55.88) * mm});
            skLineSegment(sketch, "E298.7.2.5", {"start": v(104.88, 50.95) * mm, "end": v(99.95, 55.88) * mm});
            skLineSegment(sketch, "E298.7.2.7", {"start": v(104.88, 50.95) * mm, "end": v(109.8, 55.88) * mm});
            skLineSegment(sketch, "E298.7.2.8", {"start": v(107.57, 48.26) * mm, "end": v(112.5, 53.19) * mm});
            skLineSegment(sketch, "E298.7.2.9", {"start": v(112.5, 53.19) * mm, "end": v(117.43, 48.26) * mm});
            skLineSegment(sketch, "E298.7.2.10", {"start": v(107.57, 48.26) * mm, "end": v(117.43, 48.26) * mm});
            skLineSegment(sketch, "E298.7.2.11", {"start": v(107.57, 67.3) * mm, "end": v(112.5, 62.38) * mm});
            skLineSegment(sketch, "E298.7.2.12", {"start": v(107.57, 67.3) * mm, "end": v(117.43, 67.3) * mm});
            skLineSegment(sketch, "E298.7.2.13", {"start": v(112.5, 62.38) * mm, "end": v(117.43, 67.3) * mm});
            skLineSegment(sketch, "E298.8.2.0", {"start": v(120.12, 64.62) * mm, "end": v(125.05, 59.69) * mm});
            skLineSegment(sketch, "E298.8.2.2", {"start": v(120.12, 64.62) * mm, "end": v(115.2, 59.69) * mm});
            skLineSegment(sketch, "E298.8.2.3", {"start": v(115.2, 59.69) * mm, "end": v(125.05, 59.69) * mm});
            skLineSegment(sketch, "E298.8.2.4", {"start": v(115.2, 55.88) * mm, "end": v(125.05, 55.88) * mm});
            skLineSegment(sketch, "E298.8.2.5", {"start": v(120.12, 50.95) * mm, "end": v(115.2, 55.88) * mm});
            skLineSegment(sketch, "E298.8.2.7", {"start": v(120.12, 50.95) * mm, "end": v(125.05, 55.88) * mm});
            skLineSegment(sketch, "E298.8.2.8", {"start": v(122.81, 48.26) * mm, "end": v(127.74, 53.19) * mm});
            skLineSegment(sketch, "E298.8.2.9", {"start": v(127.74, 53.19) * mm, "end": v(132.67, 48.26) * mm});
            skLineSegment(sketch, "E298.8.2.10", {"start": v(122.81, 48.26) * mm, "end": v(132.67, 48.26) * mm});
            skLineSegment(sketch, "E298.8.2.11", {"start": v(122.81, 67.3) * mm, "end": v(127.74, 62.38) * mm});
            skLineSegment(sketch, "E298.8.2.12", {"start": v(122.81, 67.3) * mm, "end": v(132.67, 67.3) * mm});
            skLineSegment(sketch, "E298.8.2.13", {"start": v(127.74, 62.38) * mm, "end": v(132.67, 67.3) * mm});
            skLineSegment(sketch, "E298.9.2.0", {"start": v(135.36, 64.62) * mm, "end": v(140.29, 59.69) * mm});
            skLineSegment(sketch, "E298.9.2.2", {"start": v(135.36, 64.62) * mm, "end": v(130.43, 59.69) * mm});
            skLineSegment(sketch, "E298.9.2.3", {"start": v(130.43, 59.69) * mm, "end": v(140.29, 59.69) * mm});
            skLineSegment(sketch, "E298.9.2.4", {"start": v(130.43, 55.88) * mm, "end": v(140.29, 55.88) * mm});
            skLineSegment(sketch, "E298.9.2.5", {"start": v(135.36, 50.95) * mm, "end": v(130.43, 55.88) * mm});
            skLineSegment(sketch, "E298.9.2.7", {"start": v(135.36, 50.95) * mm, "end": v(140.29, 55.88) * mm});
            skLineSegment(sketch, "E298.9.2.8", {"start": v(138.05, 48.26) * mm, "end": v(142.98, 53.19) * mm});
            skLineSegment(sketch, "E298.9.2.9", {"start": v(142.98, 53.19) * mm, "end": v(147.9, 48.26) * mm});
            skLineSegment(sketch, "E298.9.2.10", {"start": v(138.05, 48.26) * mm, "end": v(147.9, 48.26) * mm});
            skLineSegment(sketch, "E298.9.2.11", {"start": v(138.05, 67.3) * mm, "end": v(142.98, 62.38) * mm});
            skLineSegment(sketch, "E298.9.2.12", {"start": v(138.05, 67.3) * mm, "end": v(147.9, 67.3) * mm});
            skLineSegment(sketch, "E298.9.2.13", {"start": v(142.98, 62.38) * mm, "end": v(147.9, 67.3) * mm});
            skLineSegment(sketch, "E298.10.2.0", {"start": v(150.6, 64.62) * mm, "end": v(155.53, 59.69) * mm});
            skLineSegment(sketch, "E298.10.2.2", {"start": v(150.6, 64.62) * mm, "end": v(145.67, 59.69) * mm});
            skLineSegment(sketch, "E298.10.2.3", {"start": v(145.67, 59.69) * mm, "end": v(155.53, 59.69) * mm});
            skLineSegment(sketch, "E298.10.2.4", {"start": v(145.67, 55.88) * mm, "end": v(155.53, 55.88) * mm});
            skLineSegment(sketch, "E298.10.2.5", {"start": v(150.6, 50.95) * mm, "end": v(145.67, 55.88) * mm});
            skLineSegment(sketch, "E298.10.2.7", {"start": v(150.6, 50.95) * mm, "end": v(155.53, 55.88) * mm});
            skLineSegment(sketch, "E298.10.2.8", {"start": v(153.3, 48.26) * mm, "end": v(158.22, 53.19) * mm});
            skLineSegment(sketch, "E298.10.2.11", {"start": v(153.3, 67.3) * mm, "end": v(158.22, 62.38) * mm});
            skLineSegment(sketch, "E298.10.2.12", {"start": v(153.3, 67.3) * mm, "end": v(158.22, 67.3) * mm});
            skLineSegment(sketch, "E299", {"start": v(158.22, 53.19) * mm, "end": v(158.22, 48.26) * mm});
            skLineSegment(sketch, "E300", {"start": v(158.22, 62.38) * mm, "end": v(158.22, 67.3) * mm});
            skLineSegment(sketch, "E301", {"start": v(153.3, 48.26) * mm, "end": v(158.22, 48.26) * mm});
            skLineSegment(sketch, "E302.0.2.0", {"start": v(-9.42, 62.38) * mm, "end": v(-9.42, 67.3) * mm});
            skLineSegment(sketch, "E302.0.2.1", {"start": v(-9.42, 67.3) * mm, "end": v(-4.5, 67.3) * mm});
            skLineSegment(sketch, "E302.0.2.2", {"start": v(-4.5, 67.3) * mm, "end": v(-9.42, 62.38) * mm});
            skLineSegment(sketch, "E302.0.2.3", {"start": v(-9.42, 53.19) * mm, "end": v(-9.42, 48.26) * mm});
            skLineSegment(sketch, "E302.0.2.4", {"start": v(-9.42, 53.19) * mm, "end": v(-4.5, 48.26) * mm});
            skLineSegment(sketch, "E302.0.2.5", {"start": v(-4.5, 48.26) * mm, "end": v(-9.42, 48.26) * mm});
            skLineSegment(sketch, "E303.0.1.0", {"start": v(23.75, 36.83) * mm, "end": v(33.6, 36.83) * mm});
            skLineSegment(sketch, "E303.0.1.1", {"start": v(36.3, 30.33) * mm, "end": v(41.23, 25.4) * mm});
            skLineSegment(sketch, "E303.0.1.2", {"start": v(153.3, 44.45) * mm, "end": v(158.22, 39.52) * mm});
            skLineSegment(sketch, "E303.0.1.3", {"start": v(28.68, 28.1) * mm, "end": v(33.6, 33.02) * mm});
            skLineSegment(sketch, "E303.0.1.4", {"start": v(77.1, 44.45) * mm, "end": v(86.95, 44.45) * mm});
            skLineSegment(sketch, "E303.0.1.5", {"start": v(46.61, 25.4) * mm, "end": v(56.47, 25.4) * mm});
            skLineSegment(sketch, "E303.0.1.6", {"start": v(120.12, 28.1) * mm, "end": v(125.05, 33.02) * mm});
            skLineSegment(sketch, "E303.0.1.7", {"start": v(31.37, 25.4) * mm, "end": v(36.3, 30.33) * mm});
            skLineSegment(sketch, "E303.0.1.8", {"start": v(107.57, 44.45) * mm, "end": v(117.43, 44.45) * mm});
            skLineSegment(sketch, "E303.0.1.9", {"start": v(21.06, 30.33) * mm, "end": v(25.99, 25.4) * mm});
            skLineSegment(sketch, "E303.0.1.10", {"start": v(150.6, 28.1) * mm, "end": v(155.53, 33.02) * mm});
            skLineSegment(sketch, "E303.0.1.11", {"start": v(92.33, 44.45) * mm, "end": v(97.26, 39.52) * mm});
            skLineSegment(sketch, "E303.0.1.12", {"start": v(135.36, 28.1) * mm, "end": v(140.29, 33.02) * mm});
            skLineSegment(sketch, "E303.0.1.13", {"start": v(61.85, 44.45) * mm, "end": v(71.7, 44.45) * mm});
            skLineSegment(sketch, "E303.0.1.14", {"start": v(43.92, 41.76) * mm, "end": v(48.85, 36.83) * mm});
            skLineSegment(sketch, "E303.0.1.15", {"start": v(89.64, 41.76) * mm, "end": v(84.71, 36.83) * mm});
            skLineSegment(sketch, "E303.0.1.16", {"start": v(-6.73, 36.83) * mm, "end": v(3.13, 36.83) * mm});
            skLineSegment(sketch, "E303.0.1.17", {"start": v(-6.73, 33.02) * mm, "end": v(3.13, 33.02) * mm});
            skLineSegment(sketch, "E303.0.1.18", {"start": v(16.13, 25.4) * mm, "end": v(25.99, 25.4) * mm});
            skLineSegment(sketch, "E303.0.1.19", {"start": v(5.82, 30.33) * mm, "end": v(10.75, 25.4) * mm});
            skLineSegment(sketch, "E303.0.1.20", {"start": v(104.88, 28.1) * mm, "end": v(109.8, 33.02) * mm});
            skLineSegment(sketch, "E303.0.1.21", {"start": v(16.13, 44.45) * mm, "end": v(25.99, 44.45) * mm});
            skLineSegment(sketch, "E303.0.1.22", {"start": v(104.88, 41.76) * mm, "end": v(99.95, 36.83) * mm});
            skLineSegment(sketch, "E303.0.1.23", {"start": v(150.6, 28.1) * mm, "end": v(145.67, 33.02) * mm});
            skLineSegment(sketch, "E303.0.1.24", {"start": v(46.61, 25.4) * mm, "end": v(51.54, 30.33) * mm});
            skLineSegment(sketch, "E303.0.1.25", {"start": v(28.68, 41.76) * mm, "end": v(23.75, 36.83) * mm});
            skLineSegment(sketch, "E303.0.1.26", {"start": v(43.92, 28.1) * mm, "end": v(48.85, 33.02) * mm});
            skLineSegment(sketch, "E303.0.1.27", {"start": v(115.2, 36.83) * mm, "end": v(125.05, 36.83) * mm});
            skLineSegment(sketch, "E303.0.1.28", {"start": v(127.74, 39.52) * mm, "end": v(132.67, 44.45) * mm});
            skLineSegment(sketch, "E303.0.1.29", {"start": v(89.64, 28.1) * mm, "end": v(84.71, 33.02) * mm});
            skLineSegment(sketch, "E303.0.1.30", {"start": v(120.12, 41.76) * mm, "end": v(125.05, 36.83) * mm});
            skLineSegment(sketch, "E303.0.1.31", {"start": v(31.37, 25.4) * mm, "end": v(41.23, 25.4) * mm});
            skLineSegment(sketch, "E303.0.1.32", {"start": v(61.85, 44.45) * mm, "end": v(66.78, 39.52) * mm});
            skLineSegment(sketch, "E303.0.1.33", {"start": v(130.43, 36.83) * mm, "end": v(140.29, 36.83) * mm});
            skLineSegment(sketch, "E303.0.1.34", {"start": v(43.92, 41.76) * mm, "end": v(39, 36.83) * mm});
            skLineSegment(sketch, "E303.0.1.35", {"start": v(16.13, 44.45) * mm, "end": v(21.06, 39.52) * mm});
            skLineSegment(sketch, "E303.0.1.36", {"start": v(59.16, 28.1) * mm, "end": v(54.23, 33.02) * mm});
            skLineSegment(sketch, "E303.0.1.37", {"start": v(46.61, 44.45) * mm, "end": v(56.47, 44.45) * mm});
            skLineSegment(sketch, "E303.0.1.38", {"start": v(74.4, 41.76) * mm, "end": v(69.47, 36.83) * mm});
            skLineSegment(sketch, "E303.0.1.39", {"start": v(39, 33.02) * mm, "end": v(48.85, 33.02) * mm});
            skLineSegment(sketch, "E303.0.1.40", {"start": v(84.71, 36.83) * mm, "end": v(94.57, 36.83) * mm});
            skLineSegment(sketch, "E303.0.1.41", {"start": v(150.6, 41.76) * mm, "end": v(155.53, 36.83) * mm});
            skLineSegment(sketch, "E303.0.1.42", {"start": v(130.43, 33.02) * mm, "end": v(140.29, 33.02) * mm});
            skLineSegment(sketch, "E303.0.1.43", {"start": v(104.88, 28.1) * mm, "end": v(99.95, 33.02) * mm});
            skLineSegment(sketch, "E303.0.1.44", {"start": v(122.81, 25.4) * mm, "end": v(132.67, 25.4) * mm});
            skLineSegment(sketch, "E303.0.1.45", {"start": v(92.33, 44.45) * mm, "end": v(102.19, 44.45) * mm});
            skLineSegment(sketch, "E303.0.1.46", {"start": v(97.26, 30.33) * mm, "end": v(102.19, 25.4) * mm});
            skLineSegment(sketch, "E303.0.1.47", {"start": v(69.47, 33.02) * mm, "end": v(79.33, 33.02) * mm});
            skLineSegment(sketch, "E303.0.1.48", {"start": v(135.36, 28.1) * mm, "end": v(130.43, 33.02) * mm});
            skLineSegment(sketch, "E303.0.1.49", {"start": v(138.05, 25.4) * mm, "end": v(147.9, 25.4) * mm});
            skLineSegment(sketch, "E303.0.1.50", {"start": v(150.6, 41.76) * mm, "end": v(145.67, 36.83) * mm});
            skLineSegment(sketch, "E303.0.1.51", {"start": v(0.9, 44.45) * mm, "end": v(5.82, 39.52) * mm});
            skLineSegment(sketch, "E303.0.1.52", {"start": v(138.05, 44.45) * mm, "end": v(142.98, 39.52) * mm});
            skLineSegment(sketch, "E303.0.1.53", {"start": v(120.12, 28.1) * mm, "end": v(115.2, 33.02) * mm});
            skLineSegment(sketch, "E303.0.1.54", {"start": v(54.23, 36.83) * mm, "end": v(64.09, 36.83) * mm});
            skLineSegment(sketch, "E303.0.1.55", {"start": v(74.4, 28.1) * mm, "end": v(79.33, 33.02) * mm});
            skLineSegment(sketch, "E303.0.1.56", {"start": v(99.95, 33.02) * mm, "end": v(109.8, 33.02) * mm});
            skLineSegment(sketch, "E303.0.1.57", {"start": v(142.98, 30.33) * mm, "end": v(147.9, 25.4) * mm});
            skLineSegment(sketch, "E303.0.1.58", {"start": v(43.92, 28.1) * mm, "end": v(39, 33.02) * mm});
            skLineSegment(sketch, "E303.0.1.59", {"start": v(92.33, 25.4) * mm, "end": v(102.19, 25.4) * mm});
            skLineSegment(sketch, "E303.0.1.60", {"start": v(97.26, 39.52) * mm, "end": v(102.19, 44.45) * mm});
            skLineSegment(sketch, "E303.0.1.61", {"start": v(107.57, 25.4) * mm, "end": v(117.43, 25.4) * mm});
            skLineSegment(sketch, "E303.0.1.62", {"start": v(115.2, 33.02) * mm, "end": v(125.05, 33.02) * mm});
            skLineSegment(sketch, "E303.0.1.63", {"start": v(138.05, 44.45) * mm, "end": v(147.9, 44.45) * mm});
            skLineSegment(sketch, "E303.0.1.64", {"start": v(28.68, 41.76) * mm, "end": v(33.6, 36.83) * mm});
            skLineSegment(sketch, "E303.0.1.65", {"start": v(122.81, 25.4) * mm, "end": v(127.74, 30.33) * mm});
            skLineSegment(sketch, "E303.0.1.66", {"start": v(77.1, 25.4) * mm, "end": v(82.02, 30.33) * mm});
            skLineSegment(sketch, "E303.0.1.67", {"start": v(145.67, 36.83) * mm, "end": v(155.53, 36.83) * mm});
            skLineSegment(sketch, "E303.0.1.68", {"start": v(66.78, 30.33) * mm, "end": v(71.7, 25.4) * mm});
            skLineSegment(sketch, "E303.0.1.69", {"start": v(77.1, 25.4) * mm, "end": v(86.95, 25.4) * mm});
            skLineSegment(sketch, "E303.0.1.70", {"start": v(107.57, 25.4) * mm, "end": v(112.5, 30.33) * mm});
            skLineSegment(sketch, "E303.0.1.71", {"start": v(122.81, 44.45) * mm, "end": v(127.74, 39.52) * mm});
            skLineSegment(sketch, "E303.0.1.72", {"start": v(120.12, 41.76) * mm, "end": v(115.2, 36.83) * mm});
            skLineSegment(sketch, "E303.0.1.73", {"start": v(104.88, 41.76) * mm, "end": v(109.8, 36.83) * mm});
            skLineSegment(sketch, "E303.0.1.74", {"start": v(59.16, 41.76) * mm, "end": v(64.09, 36.83) * mm});
            skLineSegment(sketch, "E303.0.1.75", {"start": v(0.9, 25.4) * mm, "end": v(10.75, 25.4) * mm});
            skLineSegment(sketch, "E303.0.1.76", {"start": v(135.36, 41.76) * mm, "end": v(130.43, 36.83) * mm});
            skLineSegment(sketch, "E303.0.1.77", {"start": v(51.54, 39.52) * mm, "end": v(56.47, 44.45) * mm});
            skLineSegment(sketch, "E303.0.1.78", {"start": v(61.85, 25.4) * mm, "end": v(71.7, 25.4) * mm});
            skLineSegment(sketch, "E303.0.1.79", {"start": v(153.3, 25.4) * mm, "end": v(158.22, 30.33) * mm});
            skLineSegment(sketch, "E303.0.1.80", {"start": v(77.1, 44.45) * mm, "end": v(82.02, 39.52) * mm});
            skLineSegment(sketch, "E303.0.1.81", {"start": v(-1.8, 28.1) * mm, "end": v(-6.73, 33.02) * mm});
            skLineSegment(sketch, "E303.0.1.82", {"start": v(0.9, 25.4) * mm, "end": v(5.82, 30.33) * mm});
            skLineSegment(sketch, "E303.0.1.83", {"start": v(107.57, 44.45) * mm, "end": v(112.5, 39.52) * mm});
            skLineSegment(sketch, "E303.0.1.84", {"start": v(31.37, 44.45) * mm, "end": v(36.3, 39.52) * mm});
            skLineSegment(sketch, "E303.0.1.85", {"start": v(145.67, 33.02) * mm, "end": v(155.53, 33.02) * mm});
            skLineSegment(sketch, "E303.0.1.86", {"start": v(99.95, 36.83) * mm, "end": v(109.8, 36.83) * mm});
            skLineSegment(sketch, "E303.0.1.87", {"start": v(69.47, 36.83) * mm, "end": v(79.33, 36.83) * mm});
            skLineSegment(sketch, "E303.0.1.88", {"start": v(13.44, 41.76) * mm, "end": v(18.37, 36.83) * mm});
            skLineSegment(sketch, "E303.0.1.89", {"start": v(51.54, 30.33) * mm, "end": v(56.47, 25.4) * mm});
            skLineSegment(sketch, "E303.0.1.90", {"start": v(0.9, 44.45) * mm, "end": v(10.75, 44.45) * mm});
            skLineSegment(sketch, "E303.0.1.91", {"start": v(127.74, 30.33) * mm, "end": v(132.67, 25.4) * mm});
            skLineSegment(sketch, "E303.0.1.92", {"start": v(61.85, 25.4) * mm, "end": v(66.78, 30.33) * mm});
            skLineSegment(sketch, "E303.0.1.93", {"start": v(89.64, 28.1) * mm, "end": v(94.57, 33.02) * mm});
            skLineSegment(sketch, "E303.0.1.94", {"start": v(142.98, 39.52) * mm, "end": v(147.9, 44.45) * mm});
            skLineSegment(sketch, "E303.0.1.95", {"start": v(16.13, 25.4) * mm, "end": v(21.06, 30.33) * mm});
            skLineSegment(sketch, "E303.0.1.96", {"start": v(-4.5, 44.45) * mm, "end": v(-9.42, 39.52) * mm});
            skLineSegment(sketch, "E303.0.1.97", {"start": v(31.37, 44.45) * mm, "end": v(41.23, 44.45) * mm});
            skLineSegment(sketch, "E303.0.1.98", {"start": v(23.75, 33.02) * mm, "end": v(33.6, 33.02) * mm});
            skLineSegment(sketch, "E303.0.1.99", {"start": v(112.5, 30.33) * mm, "end": v(117.43, 25.4) * mm});
            skLineSegment(sketch, "E303.0.1.100", {"start": v(13.44, 41.76) * mm, "end": v(8.51, 36.83) * mm});
            skLineSegment(sketch, "E303.0.1.101", {"start": v(8.51, 36.83) * mm, "end": v(18.37, 36.83) * mm});
            skLineSegment(sketch, "E303.0.1.102", {"start": v(-1.8, 28.1) * mm, "end": v(3.13, 33.02) * mm});
            skLineSegment(sketch, "E303.0.1.103", {"start": v(74.4, 41.76) * mm, "end": v(79.33, 36.83) * mm});
            skLineSegment(sketch, "E303.0.1.104", {"start": v(59.16, 28.1) * mm, "end": v(64.09, 33.02) * mm});
            skLineSegment(sketch, "E303.0.1.105", {"start": v(59.16, 41.76) * mm, "end": v(54.23, 36.83) * mm});
            skLineSegment(sketch, "E303.0.1.106", {"start": v(5.82, 39.52) * mm, "end": v(10.75, 44.45) * mm});
            skLineSegment(sketch, "E303.0.1.107", {"start": v(92.33, 25.4) * mm, "end": v(97.26, 30.33) * mm});
            skLineSegment(sketch, "E303.0.1.108", {"start": v(66.78, 39.52) * mm, "end": v(71.7, 44.45) * mm});
            skLineSegment(sketch, "E303.0.1.109", {"start": v(28.68, 28.1) * mm, "end": v(23.75, 33.02) * mm});
            skLineSegment(sketch, "E303.0.1.110", {"start": v(122.81, 44.45) * mm, "end": v(132.67, 44.45) * mm});
            skLineSegment(sketch, "E303.0.1.111", {"start": v(138.05, 25.4) * mm, "end": v(142.98, 30.33) * mm});
            skLineSegment(sketch, "E303.0.1.112", {"start": v(135.36, 41.76) * mm, "end": v(140.29, 36.83) * mm});
            skLineSegment(sketch, "E303.0.1.113", {"start": v(8.51, 33.02) * mm, "end": v(18.37, 33.02) * mm});
            skLineSegment(sketch, "E303.0.1.114", {"start": v(21.06, 39.52) * mm, "end": v(25.99, 44.45) * mm});
            skLineSegment(sketch, "E303.0.1.115", {"start": v(82.02, 30.33) * mm, "end": v(86.95, 25.4) * mm});
            skLineSegment(sketch, "E303.0.1.116", {"start": v(74.4, 28.1) * mm, "end": v(69.47, 33.02) * mm});
            skLineSegment(sketch, "E303.0.1.117", {"start": v(54.23, 33.02) * mm, "end": v(64.09, 33.02) * mm});
            skLineSegment(sketch, "E303.0.1.118", {"start": v(89.64, 41.76) * mm, "end": v(94.57, 36.83) * mm});
            skLineSegment(sketch, "E303.0.1.119", {"start": v(112.5, 39.52) * mm, "end": v(117.43, 44.45) * mm});
            skLineSegment(sketch, "E303.0.1.120", {"start": v(13.44, 28.1) * mm, "end": v(8.51, 33.02) * mm});
            skLineSegment(sketch, "E303.0.1.121", {"start": v(13.44, 28.1) * mm, "end": v(18.37, 33.02) * mm});
            skLineSegment(sketch, "E303.0.1.122", {"start": v(39, 36.83) * mm, "end": v(48.85, 36.83) * mm});
            skLineSegment(sketch, "E303.0.1.123", {"start": v(84.71, 33.02) * mm, "end": v(94.57, 33.02) * mm});
            skLineSegment(sketch, "E303.0.1.124", {"start": v(-1.8, 41.76) * mm, "end": v(3.13, 36.83) * mm});
            skLineSegment(sketch, "E303.0.1.125", {"start": v(-1.8, 41.76) * mm, "end": v(-6.73, 36.83) * mm});
            skLineSegment(sketch, "E303.0.1.126", {"start": v(82.02, 39.52) * mm, "end": v(86.95, 44.45) * mm});
            skLineSegment(sketch, "E303.0.1.127", {"start": v(46.61, 44.45) * mm, "end": v(51.54, 39.52) * mm});
            skLineSegment(sketch, "E303.0.1.128", {"start": v(36.3, 39.52) * mm, "end": v(41.23, 44.45) * mm});
            skLineSegment(sketch, "E303.0.1.129", {"start": v(-9.42, 30.33) * mm, "end": v(-4.5, 25.4) * mm});
            skLineSegment(sketch, "E303.0.1.130", {"start": v(-4.5, 25.4) * mm, "end": v(-9.42, 25.4) * mm});
            skLineSegment(sketch, "E303.0.1.131", {"start": v(158.22, 39.52) * mm, "end": v(158.22, 44.45) * mm});
            skLineSegment(sketch, "E303.0.1.132", {"start": v(158.22, 30.33) * mm, "end": v(158.22, 25.4) * mm});
            skLineSegment(sketch, "E303.0.1.133", {"start": v(153.3, 25.4) * mm, "end": v(158.22, 25.4) * mm});
            skLineSegment(sketch, "E303.0.1.134", {"start": v(-9.42, 30.33) * mm, "end": v(-9.42, 25.4) * mm});
            skLineSegment(sketch, "E303.0.1.135", {"start": v(153.3, 44.45) * mm, "end": v(158.22, 44.45) * mm});
            skLineSegment(sketch, "E303.0.1.136", {"start": v(-9.42, 44.45) * mm, "end": v(-4.5, 44.45) * mm});
            skLineSegment(sketch, "E303.0.1.137", {"start": v(-9.42, 39.52) * mm, "end": v(-9.42, 44.45) * mm});
            skLineSegment(sketch, "E303.0.2.0", {"start": v(23.75, 13.97) * mm, "end": v(33.6, 13.97) * mm});
            skLineSegment(sketch, "E303.0.2.1", {"start": v(36.3, 7.47) * mm, "end": v(41.23, 2.54) * mm});
            skLineSegment(sketch, "E303.0.2.2", {"start": v(153.3, 21.59) * mm, "end": v(158.22, 16.66) * mm});
            skLineSegment(sketch, "E303.0.2.3", {"start": v(28.68, 5.23) * mm, "end": v(33.6, 10.16) * mm});
            skLineSegment(sketch, "E303.0.2.4", {"start": v(77.1, 21.59) * mm, "end": v(86.95, 21.59) * mm});
            skLineSegment(sketch, "E303.0.2.5", {"start": v(46.61, 2.54) * mm, "end": v(56.47, 2.54) * mm});
            skLineSegment(sketch, "E303.0.2.6", {"start": v(120.12, 5.23) * mm, "end": v(125.05, 10.16) * mm});
            skLineSegment(sketch, "E303.0.2.7", {"start": v(31.37, 2.54) * mm, "end": v(36.3, 7.47) * mm});
            skLineSegment(sketch, "E303.0.2.8", {"start": v(107.57, 21.59) * mm, "end": v(117.43, 21.59) * mm});
            skLineSegment(sketch, "E303.0.2.9", {"start": v(21.06, 7.47) * mm, "end": v(25.99, 2.54) * mm});
            skLineSegment(sketch, "E303.0.2.11", {"start": v(92.33, 21.59) * mm, "end": v(97.26, 16.66) * mm});
            skLineSegment(sketch, "E303.0.2.12", {"start": v(135.36, 5.23) * mm, "end": v(140.29, 10.16) * mm});
            skLineSegment(sketch, "E303.0.2.13", {"start": v(61.85, 21.59) * mm, "end": v(71.7, 21.59) * mm});
            skLineSegment(sketch, "E303.0.2.14", {"start": v(43.92, 18.9) * mm, "end": v(48.85, 13.97) * mm});
            skLineSegment(sketch, "E303.0.2.15", {"start": v(89.64, 18.9) * mm, "end": v(84.71, 13.97) * mm});
            skLineSegment(sketch, "E303.0.2.16", {"start": v(-6.73, 13.97) * mm, "end": v(3.13, 13.97) * mm});
            skLineSegment(sketch, "E303.0.2.17", {"start": v(-6.73, 10.16) * mm, "end": v(-1.8, 10.16) * mm});
            skLineSegment(sketch, "E303.0.2.18", {"start": v(16.13, 2.54) * mm, "end": v(25.99, 2.54) * mm});
            skLineSegment(sketch, "E303.0.2.19", {"start": v(5.82, 7.47) * mm, "end": v(10.75, 2.54) * mm});
            skLineSegment(sketch, "E303.0.2.20", {"start": v(104.88, 5.23) * mm, "end": v(109.8, 10.16) * mm});
            skLineSegment(sketch, "E303.0.2.21", {"start": v(16.13, 21.59) * mm, "end": v(25.99, 21.59) * mm});
            skLineSegment(sketch, "E303.0.2.22", {"start": v(104.88, 18.9) * mm, "end": v(99.95, 13.97) * mm});
            skLineSegment(sketch, "E303.0.2.23", {"start": v(150.6, 5.23) * mm, "end": v(145.67, 10.16) * mm});
            skLineSegment(sketch, "E303.0.2.24", {"start": v(46.61, 2.54) * mm, "end": v(51.54, 7.47) * mm});
            skLineSegment(sketch, "E303.0.2.25", {"start": v(28.68, 18.9) * mm, "end": v(23.75, 13.97) * mm});
            skLineSegment(sketch, "E303.0.2.26", {"start": v(43.92, 5.23) * mm, "end": v(48.85, 10.16) * mm});
            skLineSegment(sketch, "E303.0.2.27", {"start": v(115.2, 13.97) * mm, "end": v(125.05, 13.97) * mm});
            skLineSegment(sketch, "E303.0.2.28", {"start": v(127.74, 16.66) * mm, "end": v(132.67, 21.59) * mm});
            skLineSegment(sketch, "E303.0.2.29", {"start": v(89.64, 5.23) * mm, "end": v(84.71, 10.16) * mm});
            skLineSegment(sketch, "E303.0.2.30", {"start": v(120.12, 18.9) * mm, "end": v(125.05, 13.97) * mm});
            skLineSegment(sketch, "E303.0.2.31", {"start": v(31.37, 2.54) * mm, "end": v(41.23, 2.54) * mm});
            skLineSegment(sketch, "E303.0.2.32", {"start": v(61.85, 21.59) * mm, "end": v(66.78, 16.66) * mm});
            skLineSegment(sketch, "E303.0.2.33", {"start": v(130.43, 13.97) * mm, "end": v(140.29, 13.97) * mm});
            skLineSegment(sketch, "E303.0.2.34", {"start": v(43.92, 18.9) * mm, "end": v(39, 13.97) * mm});
            skLineSegment(sketch, "E303.0.2.35", {"start": v(16.13, 21.59) * mm, "end": v(21.06, 16.66) * mm});
            skLineSegment(sketch, "E303.0.2.36", {"start": v(59.16, 5.23) * mm, "end": v(54.23, 10.16) * mm});
            skLineSegment(sketch, "E303.0.2.37", {"start": v(46.61, 21.59) * mm, "end": v(56.47, 21.59) * mm});
            skLineSegment(sketch, "E303.0.2.38", {"start": v(74.4, 18.9) * mm, "end": v(69.47, 13.97) * mm});
            skLineSegment(sketch, "E303.0.2.39", {"start": v(39, 10.16) * mm, "end": v(48.85, 10.16) * mm});
            skLineSegment(sketch, "E303.0.2.40", {"start": v(84.71, 13.97) * mm, "end": v(94.57, 13.97) * mm});
            skLineSegment(sketch, "E303.0.2.41", {"start": v(150.6, 18.9) * mm, "end": v(155.53, 13.97) * mm});
            skLineSegment(sketch, "E303.0.2.42", {"start": v(130.43, 10.16) * mm, "end": v(140.29, 10.16) * mm});
            skLineSegment(sketch, "E303.0.2.43", {"start": v(104.88, 5.23) * mm, "end": v(99.95, 10.16) * mm});
            skLineSegment(sketch, "E303.0.2.44", {"start": v(122.81, 2.54) * mm, "end": v(132.67, 2.54) * mm});
            skLineSegment(sketch, "E303.0.2.45", {"start": v(92.33, 21.59) * mm, "end": v(102.19, 21.59) * mm});
            skLineSegment(sketch, "E303.0.2.46", {"start": v(97.26, 7.47) * mm, "end": v(102.19, 2.54) * mm});
            skLineSegment(sketch, "E303.0.2.47", {"start": v(69.47, 10.16) * mm, "end": v(79.33, 10.16) * mm});
            skLineSegment(sketch, "E303.0.2.48", {"start": v(135.36, 5.23) * mm, "end": v(130.43, 10.16) * mm});
            skLineSegment(sketch, "E303.0.2.49", {"start": v(138.05, 2.54) * mm, "end": v(147.9, 2.54) * mm});
            skLineSegment(sketch, "E303.0.2.50", {"start": v(150.6, 18.9) * mm, "end": v(145.67, 13.97) * mm});
            skLineSegment(sketch, "E303.0.2.51", {"start": v(0.9, 21.59) * mm, "end": v(5.82, 16.66) * mm});
            skLineSegment(sketch, "E303.0.2.52", {"start": v(138.05, 21.59) * mm, "end": v(142.98, 16.66) * mm});
            skLineSegment(sketch, "E303.0.2.53", {"start": v(120.12, 5.23) * mm, "end": v(115.2, 10.16) * mm});
            skLineSegment(sketch, "E303.0.2.54", {"start": v(54.23, 13.97) * mm, "end": v(64.09, 13.97) * mm});
            skLineSegment(sketch, "E303.0.2.55", {"start": v(74.4, 5.23) * mm, "end": v(79.33, 10.16) * mm});
            skLineSegment(sketch, "E303.0.2.56", {"start": v(99.95, 10.16) * mm, "end": v(109.8, 10.16) * mm});
            skLineSegment(sketch, "E303.0.2.57", {"start": v(142.98, 7.47) * mm, "end": v(147.9, 2.54) * mm});
            skLineSegment(sketch, "E303.0.2.58", {"start": v(43.92, 5.23) * mm, "end": v(39, 10.16) * mm});
            skLineSegment(sketch, "E303.0.2.59", {"start": v(92.33, 2.54) * mm, "end": v(102.19, 2.54) * mm});
            skLineSegment(sketch, "E303.0.2.60", {"start": v(97.26, 16.66) * mm, "end": v(102.19, 21.59) * mm});
            skLineSegment(sketch, "E303.0.2.61", {"start": v(107.57, 2.54) * mm, "end": v(117.43, 2.54) * mm});
            skLineSegment(sketch, "E303.0.2.62", {"start": v(115.2, 10.16) * mm, "end": v(125.05, 10.16) * mm});
            skLineSegment(sketch, "E303.0.2.63", {"start": v(138.05, 21.59) * mm, "end": v(147.9, 21.59) * mm});
            skLineSegment(sketch, "E303.0.2.64", {"start": v(28.68, 18.9) * mm, "end": v(33.6, 13.97) * mm});
            skLineSegment(sketch, "E303.0.2.65", {"start": v(122.81, 2.54) * mm, "end": v(127.74, 7.47) * mm});
            skLineSegment(sketch, "E303.0.2.66", {"start": v(77.1, 2.54) * mm, "end": v(82.02, 7.47) * mm});
            skLineSegment(sketch, "E303.0.2.67", {"start": v(145.67, 13.97) * mm, "end": v(155.53, 13.97) * mm});
            skLineSegment(sketch, "E303.0.2.68", {"start": v(66.78, 7.47) * mm, "end": v(71.7, 2.54) * mm});
            skLineSegment(sketch, "E303.0.2.69", {"start": v(77.1, 2.54) * mm, "end": v(86.95, 2.54) * mm});
            skLineSegment(sketch, "E303.0.2.70", {"start": v(107.57, 2.54) * mm, "end": v(112.5, 7.47) * mm});
            skLineSegment(sketch, "E303.0.2.71", {"start": v(122.81, 21.59) * mm, "end": v(127.74, 16.66) * mm});
            skLineSegment(sketch, "E303.0.2.72", {"start": v(120.12, 18.9) * mm, "end": v(115.2, 13.97) * mm});
            skLineSegment(sketch, "E303.0.2.73", {"start": v(104.88, 18.9) * mm, "end": v(109.8, 13.97) * mm});
            skLineSegment(sketch, "E303.0.2.74", {"start": v(59.16, 18.9) * mm, "end": v(64.09, 13.97) * mm});
            skLineSegment(sketch, "E303.0.2.75", {"start": v(5.82, 2.54) * mm, "end": v(10.75, 2.54) * mm});
            skLineSegment(sketch, "E303.0.2.76", {"start": v(135.36, 18.9) * mm, "end": v(130.43, 13.97) * mm});
            skLineSegment(sketch, "E303.0.2.77", {"start": v(51.54, 16.66) * mm, "end": v(56.47, 21.59) * mm});
            skLineSegment(sketch, "E303.0.2.78", {"start": v(61.85, 2.54) * mm, "end": v(71.7, 2.54) * mm});
            skLineSegment(sketch, "E303.0.2.80", {"start": v(77.1, 21.59) * mm, "end": v(82.02, 16.66) * mm});
            skLineSegment(sketch, "E303.0.2.81", {"start": v(-1.8, 5.23) * mm, "end": v(-6.73, 10.16) * mm});
            skLineSegment(sketch, "E303.0.2.83", {"start": v(107.57, 21.59) * mm, "end": v(112.5, 16.66) * mm});
            skLineSegment(sketch, "E303.0.2.84", {"start": v(31.37, 21.59) * mm, "end": v(36.3, 16.66) * mm});
            skLineSegment(sketch, "E303.0.2.85", {"start": v(145.67, 10.16) * mm, "end": v(150.6, 10.16) * mm});
            skLineSegment(sketch, "E303.0.2.86", {"start": v(99.95, 13.97) * mm, "end": v(109.8, 13.97) * mm});
            skLineSegment(sketch, "E303.0.2.87", {"start": v(69.47, 13.97) * mm, "end": v(79.33, 13.97) * mm});
            skLineSegment(sketch, "E303.0.2.88", {"start": v(13.44, 18.9) * mm, "end": v(18.37, 13.97) * mm});
            skLineSegment(sketch, "E303.0.2.89", {"start": v(51.54, 7.47) * mm, "end": v(56.47, 2.54) * mm});
            skLineSegment(sketch, "E303.0.2.90", {"start": v(0.9, 21.59) * mm, "end": v(10.75, 21.59) * mm});
            skLineSegment(sketch, "E303.0.2.91", {"start": v(127.74, 7.47) * mm, "end": v(132.67, 2.54) * mm});
            skLineSegment(sketch, "E303.0.2.92", {"start": v(61.85, 2.54) * mm, "end": v(66.78, 7.47) * mm});
            skLineSegment(sketch, "E303.0.2.93", {"start": v(89.64, 5.23) * mm, "end": v(94.57, 10.16) * mm});
            skLineSegment(sketch, "E303.0.2.94", {"start": v(142.98, 16.66) * mm, "end": v(147.9, 21.59) * mm});
            skLineSegment(sketch, "E303.0.2.95", {"start": v(16.13, 2.54) * mm, "end": v(21.06, 7.47) * mm});
            skLineSegment(sketch, "E303.0.2.96", {"start": v(-4.5, 21.59) * mm, "end": v(-9.42, 16.66) * mm});
            skLineSegment(sketch, "E303.0.2.97", {"start": v(31.37, 21.59) * mm, "end": v(41.23, 21.59) * mm});
            skLineSegment(sketch, "E303.0.2.98", {"start": v(23.75, 10.16) * mm, "end": v(33.6, 10.16) * mm});
            skLineSegment(sketch, "E303.0.2.99", {"start": v(112.5, 7.47) * mm, "end": v(117.43, 2.54) * mm});
            skLineSegment(sketch, "E303.0.2.100", {"start": v(13.44, 18.9) * mm, "end": v(8.51, 13.97) * mm});
            skLineSegment(sketch, "E303.0.2.101", {"start": v(8.51, 13.97) * mm, "end": v(18.37, 13.97) * mm});
            skLineSegment(sketch, "E303.0.2.103", {"start": v(74.4, 18.9) * mm, "end": v(79.33, 13.97) * mm});
            skLineSegment(sketch, "E303.0.2.104", {"start": v(59.16, 5.23) * mm, "end": v(64.09, 10.16) * mm});
            skLineSegment(sketch, "E303.0.2.105", {"start": v(59.16, 18.9) * mm, "end": v(54.23, 13.97) * mm});
            skLineSegment(sketch, "E303.0.2.106", {"start": v(5.82, 16.66) * mm, "end": v(10.75, 21.59) * mm});
            skLineSegment(sketch, "E303.0.2.107", {"start": v(92.33, 2.54) * mm, "end": v(97.26, 7.47) * mm});
            skLineSegment(sketch, "E303.0.2.108", {"start": v(66.78, 16.66) * mm, "end": v(71.7, 21.59) * mm});
            skLineSegment(sketch, "E303.0.2.109", {"start": v(28.68, 5.23) * mm, "end": v(23.75, 10.16) * mm});
            skLineSegment(sketch, "E303.0.2.110", {"start": v(122.81, 21.59) * mm, "end": v(132.67, 21.59) * mm});
            skLineSegment(sketch, "E303.0.2.111", {"start": v(138.05, 2.54) * mm, "end": v(142.98, 7.47) * mm});
            skLineSegment(sketch, "E303.0.2.112", {"start": v(135.36, 18.9) * mm, "end": v(140.29, 13.97) * mm});
            skLineSegment(sketch, "E303.0.2.113", {"start": v(8.51, 10.16) * mm, "end": v(18.37, 10.16) * mm});
            skLineSegment(sketch, "E303.0.2.114", {"start": v(21.06, 16.66) * mm, "end": v(25.99, 21.59) * mm});
            skLineSegment(sketch, "E303.0.2.115", {"start": v(82.02, 7.47) * mm, "end": v(86.95, 2.54) * mm});
            skLineSegment(sketch, "E303.0.2.116", {"start": v(74.4, 5.23) * mm, "end": v(69.47, 10.16) * mm});
            skLineSegment(sketch, "E303.0.2.117", {"start": v(54.23, 10.16) * mm, "end": v(64.09, 10.16) * mm});
            skLineSegment(sketch, "E303.0.2.118", {"start": v(89.64, 18.9) * mm, "end": v(94.57, 13.97) * mm});
            skLineSegment(sketch, "E303.0.2.119", {"start": v(112.5, 16.66) * mm, "end": v(117.43, 21.59) * mm});
            skLineSegment(sketch, "E303.0.2.120", {"start": v(13.44, 5.23) * mm, "end": v(8.51, 10.16) * mm});
            skLineSegment(sketch, "E303.0.2.121", {"start": v(13.44, 5.23) * mm, "end": v(18.37, 10.16) * mm});
            skLineSegment(sketch, "E303.0.2.122", {"start": v(39, 13.97) * mm, "end": v(48.85, 13.97) * mm});
            skLineSegment(sketch, "E303.0.2.123", {"start": v(84.71, 10.16) * mm, "end": v(94.57, 10.16) * mm});
            skLineSegment(sketch, "E303.0.2.124", {"start": v(-1.8, 18.9) * mm, "end": v(3.13, 13.97) * mm});
            skLineSegment(sketch, "E303.0.2.125", {"start": v(-1.8, 18.9) * mm, "end": v(-6.73, 13.97) * mm});
            skLineSegment(sketch, "E303.0.2.126", {"start": v(82.02, 16.66) * mm, "end": v(86.95, 21.59) * mm});
            skLineSegment(sketch, "E303.0.2.127", {"start": v(46.61, 21.59) * mm, "end": v(51.54, 16.66) * mm});
            skLineSegment(sketch, "E303.0.2.128", {"start": v(36.3, 16.66) * mm, "end": v(41.23, 21.59) * mm});
            skLineSegment(sketch, "E303.0.2.129", {"start": v(-9.42, 7.47) * mm, "end": v(-4.5, 2.54) * mm});
            skLineSegment(sketch, "E303.0.2.130", {"start": v(-4.5, 2.54) * mm, "end": v(-9.42, 2.54) * mm});
            skLineSegment(sketch, "E303.0.2.131", {"start": v(158.22, 16.66) * mm, "end": v(158.22, 21.59) * mm});
            skLineSegment(sketch, "E303.0.2.134", {"start": v(-9.42, 7.47) * mm, "end": v(-9.42, 2.54) * mm});
            skLineSegment(sketch, "E303.0.2.135", {"start": v(153.3, 21.59) * mm, "end": v(158.22, 21.59) * mm});
            skLineSegment(sketch, "E303.0.2.136", {"start": v(-9.42, 21.59) * mm, "end": v(-4.5, 21.59) * mm});
            skLineSegment(sketch, "E303.0.2.137", {"start": v(-9.42, 16.66) * mm, "end": v(-9.42, 21.59) * mm});
            skLineSegment(sketch, "E303.direction1", {"start": v(-9.42, 48.26) * mm, "end": v(15.98, 48.26) * mm, "construction": true});
            skLineSegment(sketch, "E303.direction2", {"start": v(-9.42, 48.26) * mm, "end": v(-9.42, 25.4) * mm, "construction": true});
            skLineSegment(sketch, "E304", {"start": v(-1.8, 5.23) * mm, "end": v(-1.8, 10.16) * mm});
            skLineSegment(sketch, "E305", {"start": v(5.82, 7.47) * mm, "end": v(5.82, 2.54) * mm});
            skLineSegment(sketch, "E306", {"start": v(150.6, 5.23) * mm, "end": v(150.6, 10.16) * mm});
            skSolve(sketch);
        }
        {
            var Q0;
            Q0=qSketchRegion(id+"F32",true);
            extrude(context, id + "F33", {"entities" : qUnion([Q0]), "operationType" : NewBodyOperationType.REMOVE, "oppositeDirection" : true, "depth" : 2.54 * mm, "offsetDistance" : 25.4 * mm});
        }
        {
            var Q0;
            Q0=makeQuery(id+"F2.opExtrude","CAP_FACE",FACE,{"disambiguationData":[OSD([sQuery(id+"F1.wireOp",EDGE,"E8.0"),sQuery(id+"F1.wireOp",EDGE,"E8.1"),sQuery(id+"F1.wireOp",EDGE,"E8.2"),sQuery(id+"F1.wireOp",EDGE,"E8.3"),sQuery(id+"F1.wireOp",EDGE,"E9.0"),sQuery(id+"F1.wireOp",EDGE,"E9.1"),sQuery(id+"F1.wireOp",EDGE,"E9.2"),sQuery(id+"F1.wireOp",EDGE,"E9.3")])],"isStart":false});
            cPlane(context, id + "F34", {"entities" : qUnion([Q0]), "cplaneType" : CPlaneType.OFFSET, "offset" : 1.27 * mm, "oppositeDirection" : true, "width" : 152.4 * mm, "height" : 152.4 * mm});
        }
        {
            var Q0;
            Q0=makeQuery(id+"F6.boolean.opBoolean","MERGE",FACE,{"derivedFrom":[makeQuery(id+"F2.opExtrude","SWEPT_FACE",FACE,{"disambiguationData":[OSD([sQuery(id+"F1.wireOp",EDGE,"E9.0")])]}),makeQuery(id+"F6.opExtrude","SWEPT_FACE",FACE,{"disambiguationData":[OSD([sQuery(id+"F5.wireOp",EDGE,"E60.bottom")])]})]});
            var sketch = newSketch(context, id + "F35", { "sketchPlane" : qUnion([Q0])});
            skLineSegment(sketch, "E307.bottom", {"start": v(-171.9, -1.27) * mm, "end": v(14.6, -1.27) * mm});
            skLineSegment(sketch, "E307.top", {"start": v(-171.9, 23.16) * mm, "end": v(14.6, 23.16) * mm});
            skLineSegment(sketch, "E307.left", {"start": v(-171.9, -1.27) * mm, "end": v(-171.9, 23.16) * mm});
            skLineSegment(sketch, "E307.right", {"start": v(14.6, -1.27) * mm, "end": v(14.6, 23.16) * mm});
            skSolve(sketch);
        }
        {
            var Q0;
            Q0 = qSketchRegion(id + "F35", true);
            extrude(context, id + "F36", {"entities" : qUnion([Q0]), "operationType" : NewBodyOperationType.REMOVE, "endBound" : BoundingType.THROUGH_ALL, "oppositeDirection" : true, "depth" : 25.4 * mm, "offsetDistance" : 25.4 * mm});
        }
        {
            var Q0;
            Q0=makeQuery(id+"F6.boolean.opBoolean","MERGE",FACE,{"derivedFrom":[makeQuery(id+"F2.opExtrude","SWEPT_FACE",FACE,{"disambiguationData":[OSD([sQuery(id+"F1.wireOp",EDGE,"E9.0")])]}),makeQuery(id+"F6.opExtrude","SWEPT_FACE",FACE,{"disambiguationData":[OSD([sQuery(id+"F5.wireOp",EDGE,"E60.bottom")])]})]});
            var sketch = newSketch(context, id + "F37", { "sketchPlane" : qUnion([Q0])});
            skLineSegment(sketch, "E308.bottom", {"start": v(-166.9, 68.25) * mm, "end": v(-7.52, 68.25) * mm});
            skLineSegment(sketch, "E308.top", {"start": v(-166.9, 23.16) * mm, "end": v(-7.52, 23.16) * mm});
            skLineSegment(sketch, "E308.left", {"start": v(-166.9, 68.25) * mm, "end": v(-166.9, 23.16) * mm});
            skLineSegment(sketch, "E308.right", {"start": v(-7.52, 68.25) * mm, "end": v(-7.52, 23.16) * mm});
            skSolve(sketch);
        }
        {
            var Q0;
            Q0 = qSketchRegion(id + "F37", true);
            extrude(context, id + "F38", {"entities" : qUnion([Q0]), "operationType" : NewBodyOperationType.REMOVE, "oppositeDirection" : true, "depth" : 25.4 * mm, "offsetDistance" : 25.4 * mm});
        }
        {
            var Q0;
            Q0=makeQuery(id+"F2.opExtrude","CAP_FACE",FACE,{"disambiguationData":[OSD([sQuery(id+"F1.wireOp",EDGE,"E8.0"),sQuery(id+"F1.wireOp",EDGE,"E8.1"),sQuery(id+"F1.wireOp",EDGE,"E8.2"),sQuery(id+"F1.wireOp",EDGE,"E8.3"),sQuery(id+"F1.wireOp",EDGE,"E9.0"),sQuery(id+"F1.wireOp",EDGE,"E9.1"),sQuery(id+"F1.wireOp",EDGE,"E9.2"),sQuery(id+"F1.wireOp",EDGE,"E9.3")])],"isStart":false});
            var sketch = newSketch(context, id + "F39", { "sketchPlane" : qUnion([Q0])});
            skLineSegment(sketch, "E309.0", {"start": v(-12.7, 16.51) * mm, "end": v(170, 16.51) * mm});
            skLineSegment(sketch, "E310.0", {"start": v(-12.7, 16.51) * mm, "end": v(-12.7, -166.2) * mm});
            skLineSegment(sketch, "E311.0", {"start": v(-12.7, -166.2) * mm, "end": v(170, -166.2) * mm});
            skLineSegment(sketch, "E312.0", {"start": v(170, 16.51) * mm, "end": v(170, -166.2) * mm});
            skSolve(sketch);
        }
        {
            var Q0;
            Q0 = qSketchRegion(id + "F39", true);
            extrude(context, id + "F40", {"entities" : qUnion([Q0]), "operationType" : NewBodyOperationType.REMOVE, "endBound" : BoundingType.THROUGH_ALL, "oppositeDirection" : true, "depth" : 25.4 * mm, "offsetDistance" : 25.4 * mm});
        }
        {
            var Q0;
            Q0=makeQuery(id+"F2.opExtrude","CAP_FACE",FACE,{"disambiguationData":[OSD([sQuery(id+"F1.wireOp",EDGE,"E8.0"),sQuery(id+"F1.wireOp",EDGE,"E8.1"),sQuery(id+"F1.wireOp",EDGE,"E8.2"),sQuery(id+"F1.wireOp",EDGE,"E8.3"),sQuery(id+"F1.wireOp",EDGE,"E9.0"),sQuery(id+"F1.wireOp",EDGE,"E9.1"),sQuery(id+"F1.wireOp",EDGE,"E9.2"),sQuery(id+"F1.wireOp",EDGE,"E9.3")])],"isStart":false});
            var sketch = newSketch(context, id + "F41", { "sketchPlane" : qUnion([Q0])});
            skLineSegment(sketch, "E313.bottom", {"start": v(-12.7, 16.51) * mm, "end": v(-6.35, 16.51) * mm});
            skLineSegment(sketch, "E313.top", {"start": v(-12.7, 10.16) * mm, "end": v(-6.35, 10.16) * mm});
            skLineSegment(sketch, "E313.left", {"start": v(-12.7, 16.51) * mm, "end": v(-12.7, 10.16) * mm});
            skLineSegment(sketch, "E313.right", {"start": v(-6.35, 16.51) * mm, "end": v(-6.35, 10.16) * mm});
            skLineSegment(sketch, "E314.bottom", {"start": v(170, 16.51) * mm, "end": v(163.65, 16.51) * mm});
            skLineSegment(sketch, "E314.top", {"start": v(170, 10.16) * mm, "end": v(163.65, 10.16) * mm});
            skLineSegment(sketch, "E314.left", {"start": v(170, 16.51) * mm, "end": v(170, 10.16) * mm});
            skLineSegment(sketch, "E314.right", {"start": v(163.65, 16.51) * mm, "end": v(163.65, 10.16) * mm});
            skLineSegment(sketch, "E315.bottom", {"start": v(170, -166.2) * mm, "end": v(163.65, -166.2) * mm});
            skLineSegment(sketch, "E315.top", {"start": v(170, -159.84) * mm, "end": v(163.65, -159.84) * mm});
            skLineSegment(sketch, "E315.left", {"start": v(170, -166.2) * mm, "end": v(170, -159.84) * mm});
            skLineSegment(sketch, "E315.right", {"start": v(163.65, -166.2) * mm, "end": v(163.65, -159.84) * mm});
            skLineSegment(sketch, "E316.bottom", {"start": v(-12.7, -166.2) * mm, "end": v(-6.35, -166.2) * mm});
            skLineSegment(sketch, "E316.top", {"start": v(-12.7, -159.84) * mm, "end": v(-6.35, -159.84) * mm});
            skLineSegment(sketch, "E316.left", {"start": v(-12.7, -166.2) * mm, "end": v(-12.7, -159.84) * mm});
            skLineSegment(sketch, "E316.right", {"start": v(-6.35, -166.2) * mm, "end": v(-6.35, -159.84) * mm});
            skSolve(sketch);
        }
        {
            var Q0;
            Q0 = qSketchRegion(id + "F41", true);
            var Q1;
            Q1=qCreatedBy(makeId("Top.planeOp"),FACE);
            extrude(context, id + "F42", {"entities" : qUnion([Q0]), "operationType" : NewBodyOperationType.ADD, "endBound" : BoundingType.UP_TO_SURFACE, "oppositeDirection" : true, "depth" : 25.4 * mm, "endBoundEntityFace" : qUnion([Q1]), "offsetDistance" : 25.4 * mm});
        }
        {
            var Q0;
            Q0=qCreatedBy(id+"F34.planeOp",FACE);
            var sketch = newSketch(context, id + "F43", { "sketchPlane" : qUnion([Q0])});
            skLineSegment(sketch, "E317.bottom", {"start": v(-12.7, 16.51) * mm, "end": v(170, 16.51) * mm});
            skLineSegment(sketch, "E317.top", {"start": v(-12.7, -166.2) * mm, "end": v(170, -166.2) * mm});
            skLineSegment(sketch, "E317.left", {"start": v(-12.7, 16.51) * mm, "end": v(-12.7, -166.2) * mm});
            skLineSegment(sketch, "E317.right", {"start": v(170, 16.51) * mm, "end": v(170, -166.2) * mm});
            skCircle(sketch, "E318", {"center": v(104.14, -76.2) * mm, "radius": 50.8 * mm, "construction": true});
            skLineSegment(sketch, "E319", {"start": v(104.14, -76.2) * mm, "end": v(104.14, -25.4) * mm, "construction": true});
            skLineSegment(sketch, "E320", {"start": v(104.14, -76.2) * mm, "end": v(68.22, -40.28) * mm, "construction": true});
            skLineSegment(sketch, "E321", {"start": v(104.14, -76.2) * mm, "end": v(53.34, -76.2) * mm});
            skPoint(sketch, "E322.center", {"position": v(0, 0) * mm});
            skCircle(sketch, "E323", {"center": v(104.14, -76.2) * mm, "radius": 12.7 * mm, "construction": true});
            skLineSegment(sketch, "E324", {"start": v(104.14, -76.2) * mm, "end": v(99.28, -64.47) * mm, "construction": true});
            skLineSegment(sketch, "E325", {"start": v(99.28, -64.47) * mm, "end": v(99.28, -25.63) * mm});
            skLineSegment(sketch, "E326", {"start": v(71.82, -37) * mm, "end": v(99.28, -64.47) * mm});
            skArc(sketch, "E327", {"start": v(99.28, -25.63) * mm, "mid": v(84.7, -29.27) * mm, "end": v(71.82, -37) * mm});
            skLineSegment(sketch, "E328.1.0", {"start": v(92.4, -71.34) * mm, "end": v(64.95, -43.88) * mm});
            skLineSegment(sketch, "E328.1.1", {"start": v(53.57, -71.34) * mm, "end": v(92.4, -71.34) * mm});
            skArc(sketch, "E328.1.2", {"start": v(64.95, -43.88) * mm, "mid": v(57.2, -56.76) * mm, "end": v(53.57, -71.34) * mm});
            skLineSegment(sketch, "E328.2.0", {"start": v(92.4, -81.06) * mm, "end": v(53.57, -81.06) * mm});
            skLineSegment(sketch, "E328.2.1", {"start": v(64.95, -108.52) * mm, "end": v(92.4, -81.06) * mm});
            skArc(sketch, "E328.2.2", {"start": v(53.57, -81.06) * mm, "mid": v(57.2, -95.64) * mm, "end": v(64.95, -108.52) * mm});
            skLineSegment(sketch, "E328.3.0", {"start": v(99.28, -87.93) * mm, "end": v(71.82, -115.4) * mm});
            skLineSegment(sketch, "E328.3.1", {"start": v(99.28, -126.77) * mm, "end": v(99.28, -87.93) * mm});
            skArc(sketch, "E328.3.2", {"start": v(71.82, -115.4) * mm, "mid": v(84.7, -123.13) * mm, "end": v(99.28, -126.77) * mm});
            skLineSegment(sketch, "E328.4.0", {"start": v(109, -87.93) * mm, "end": v(109, -126.77) * mm});
            skLineSegment(sketch, "E328.4.1", {"start": v(136.46, -115.4) * mm, "end": v(109, -87.93) * mm});
            skArc(sketch, "E328.4.2", {"start": v(109, -126.77) * mm, "mid": v(123.58, -123.13) * mm, "end": v(136.46, -115.4) * mm});
            skLineSegment(sketch, "E328.5.0", {"start": v(115.87, -81.06) * mm, "end": v(143.33, -108.52) * mm});
            skLineSegment(sketch, "E328.5.1", {"start": v(154.7, -81.06) * mm, "end": v(115.87, -81.06) * mm});
            skArc(sketch, "E328.5.2", {"start": v(143.33, -108.52) * mm, "mid": v(151.07, -95.64) * mm, "end": v(154.7, -81.06) * mm});
            skLineSegment(sketch, "E328.6.0", {"start": v(115.87, -71.34) * mm, "end": v(154.7, -71.34) * mm});
            skLineSegment(sketch, "E328.6.1", {"start": v(143.33, -43.88) * mm, "end": v(115.87, -71.34) * mm});
            skArc(sketch, "E328.6.2", {"start": v(154.7, -71.34) * mm, "mid": v(151.07, -56.76) * mm, "end": v(143.33, -43.88) * mm});
            skLineSegment(sketch, "E328.7.0", {"start": v(109, -64.47) * mm, "end": v(136.46, -37) * mm});
            skLineSegment(sketch, "E328.7.1", {"start": v(109, -25.63) * mm, "end": v(109, -64.47) * mm});
            skArc(sketch, "E328.7.2", {"start": v(136.46, -37) * mm, "mid": v(123.58, -29.27) * mm, "end": v(109, -25.63) * mm});
            skSolve(sketch);
        }
        {
            var Q0;
            Q0 = qSketchRegion(id + "F43", true);
            var Q1;
            Q1=makeQuery(id+"F42.boolean.opBoolean","MERGE",FACE,{"derivedFrom":[makeQuery(id+"F2.opExtrude","CAP_FACE",FACE,{"disambiguationData":[OSD([sQuery(id+"F1.wireOp",EDGE,"E8.0"),sQuery(id+"F1.wireOp",EDGE,"E8.1"),sQuery(id+"F1.wireOp",EDGE,"E8.2"),sQuery(id+"F1.wireOp",EDGE,"E8.3"),sQuery(id+"F1.wireOp",EDGE,"E9.0"),sQuery(id+"F1.wireOp",EDGE,"E9.1"),sQuery(id+"F1.wireOp",EDGE,"E9.2"),sQuery(id+"F1.wireOp",EDGE,"E9.3")])],"isStart":false}),makeQuery(id+"F42.opExtrude","CAP_FACE",FACE,{"disambiguationData":[OSD([sQuery(id+"F41.wireOp",EDGE,"E313.bottom"),sQuery(id+"F41.wireOp",EDGE,"E313.top"),sQuery(id+"F41.wireOp",EDGE,"E313.left"),sQuery(id+"F41.wireOp",EDGE,"E313.right")])],"isStart":true}),makeQuery(id+"F42.opExtrude","CAP_FACE",FACE,{"disambiguationData":[OSD([sQuery(id+"F41.wireOp",EDGE,"E314.bottom"),sQuery(id+"F41.wireOp",EDGE,"E314.top"),sQuery(id+"F41.wireOp",EDGE,"E314.left"),sQuery(id+"F41.wireOp",EDGE,"E314.right")])],"isStart":true}),makeQuery(id+"F42.opExtrude","CAP_FACE",FACE,{"disambiguationData":[OSD([sQuery(id+"F41.wireOp",EDGE,"E315.bottom"),sQuery(id+"F41.wireOp",EDGE,"E315.top"),sQuery(id+"F41.wireOp",EDGE,"E315.left"),sQuery(id+"F41.wireOp",EDGE,"E315.right")])],"isStart":true}),makeQuery(id+"F42.opExtrude","CAP_FACE",FACE,{"disambiguationData":[OSD([sQuery(id+"F41.wireOp",EDGE,"E316.bottom"),sQuery(id+"F41.wireOp",EDGE,"E316.top"),sQuery(id+"F41.wireOp",EDGE,"E316.left"),sQuery(id+"F41.wireOp",EDGE,"E316.right")])],"isStart":true})]});
            extrude(context, id + "F44", {"entities" : qUnion([Q0]), "operationType" : NewBodyOperationType.ADD, "endBound" : BoundingType.UP_TO_SURFACE, "depth" : 25.4 * mm, "endBoundEntityFace" : qUnion([Q1]), "offsetDistance" : 25.4 * mm});
        }
        {
            var Q0;
            Q0=makeQuery(id+"F42.opExtrude","SWEPT_EDGE",EDGE,{"disambiguationData":[OSD([sQuery(id+"F41.wireOp",EDGE,"E316.top"),sQuery(id+"F41.wireOp",EDGE,"E316.right")])]});
            var Q1;
            Q1=makeQuery(id+"F42.opExtrude","SWEPT_EDGE",EDGE,{"disambiguationData":[OSD([sQuery(id+"F41.wireOp",EDGE,"E315.top"),sQuery(id+"F41.wireOp",EDGE,"E315.right")])]});
            var Q2;
            Q2=makeQuery(id+"F42.opExtrude","SWEPT_EDGE",EDGE,{"disambiguationData":[OSD([sQuery(id+"F41.wireOp",EDGE,"E314.top"),sQuery(id+"F41.wireOp",EDGE,"E314.right")])]});
            var Q3;
            Q3=makeQuery(id+"F42.opExtrude","SWEPT_EDGE",EDGE,{"disambiguationData":[OSD([sQuery(id+"F41.wireOp",EDGE,"E313.top"),sQuery(id+"F41.wireOp",EDGE,"E313.right")])]});
            fillet(context, id + "F45", {"entities" : qUnion([Q0, Q1, Q2, Q3]), "radius" : 5.08 * mm, "tangentPropagation" : true, "allowEdgeOverflow" : false});
        }
    });
